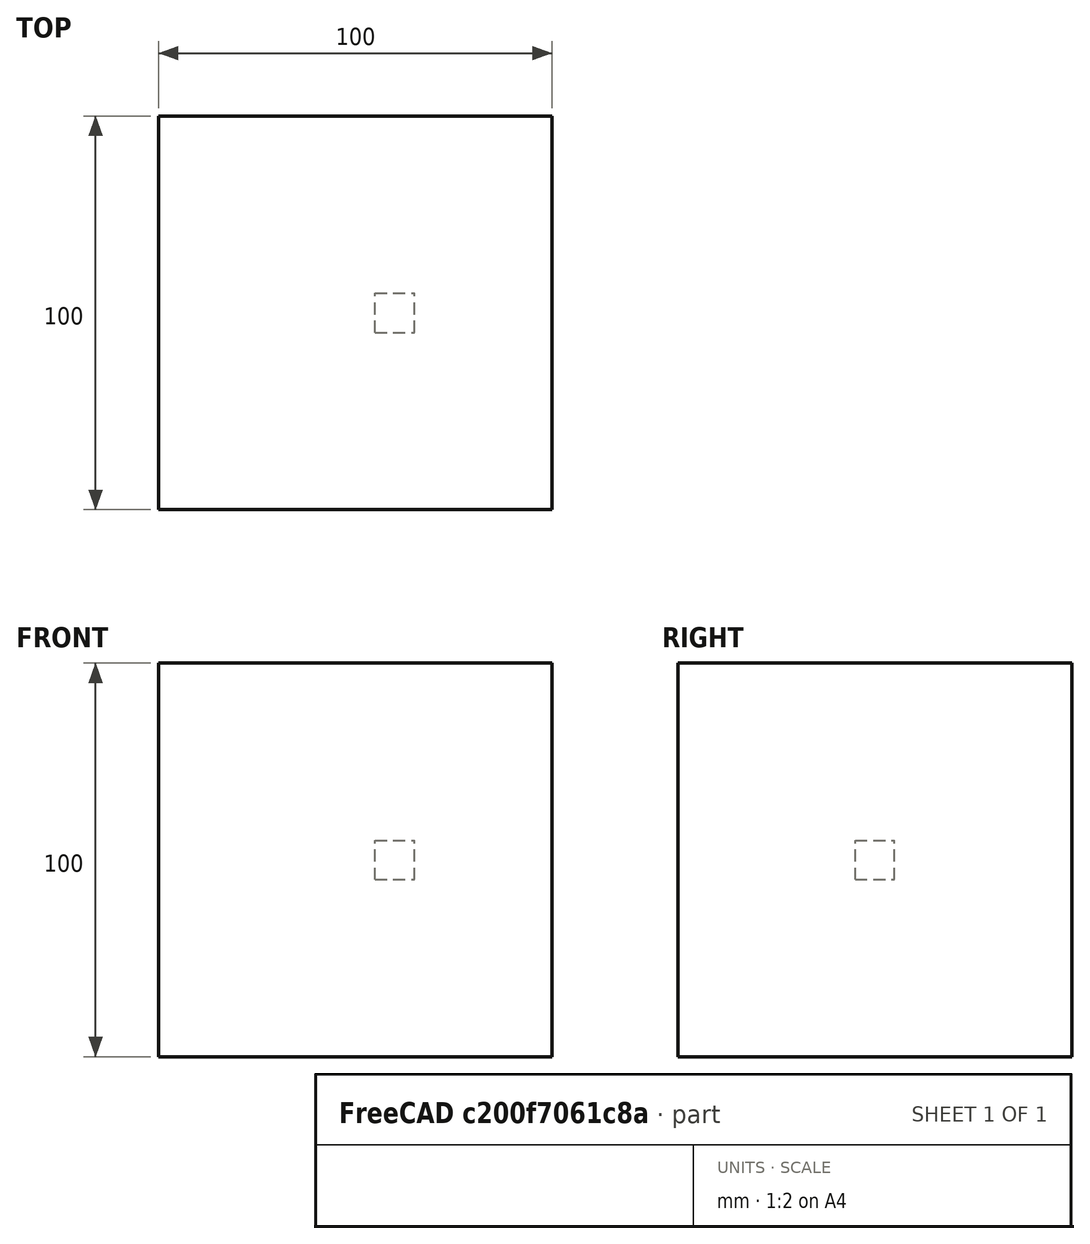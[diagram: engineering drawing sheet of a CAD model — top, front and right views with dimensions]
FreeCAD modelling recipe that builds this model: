
FCSTD DOCUMENT  (FreeCAD 0.20RUnknown)
Label: orthoArray-1
License: All rights reserved
objects: App::DocumentObjectGroupPython×1251, Part::FeaturePython×3, App::Part×3
note: 2 computed .brp shape members not serialized (recipe doc carries the construction recipe); baked Part::Feature solids carry a one-line shape summary decoded from their .brp

FEATURE [App::DocumentObjectGroupPython] HALFPI  # scripted group (container) (typed FeaturePython)
  name = HALFPI
  value = pi/2.
FEATURE [App::DocumentObjectGroupPython] PI  # scripted group (container) (typed FeaturePython)
  name = PI
  value = 1.*pi
FEATURE [App::DocumentObjectGroupPython] TWOPI  # scripted group (container) (typed FeaturePython)
  name = TWOPI
  value = 2.*pi
FEATURE [App::DocumentObjectGroupPython] Constants  # scripted group (container) (typed FeaturePython)
  Group = -> [HALFPI,PI,TWOPI]
FEATURE [App::DocumentObjectGroupPython] Variables  # scripted group (container) (typed FeaturePython)
FEATURE [App::DocumentObjectGroupPython] Quantities  # scripted group (container) (typed FeaturePython)
FEATURE [App::DocumentObjectGroupPython] Isotopes  # scripted group (container) (typed FeaturePython)
FEATURE [App::DocumentObjectGroupPython] Elements  # scripted group (container) (typed FeaturePython)
FEATURE [App::DocumentObjectGroupPython] Matrix  # scripted group (container) (typed FeaturePython)
FEATURE [App::DocumentObjectGroupPython] Surfaces  # scripted group (container) (typed FeaturePython)
FEATURE [App::DocumentObjectGroupPython] Opticals  # scripted group (container) (typed FeaturePython)
  Group = -> [Matrix,Surfaces]
FEATURE [App::DocumentObjectGroupPython] G4Isotopes  # scripted group (container) (typed FeaturePython)
FEATURE [App::DocumentObjectGroupPython] H_element  # scripted group (container) (typed FeaturePython)
  Z = 1
  atom_value = 1.008
  formula = H
  name = H_element
FEATURE [App::DocumentObjectGroupPython] He_element  # scripted group (container) (typed FeaturePython)
  Z = 2
  atom_value = 4.0026
  formula = He
  name = He_element
FEATURE [App::DocumentObjectGroupPython] Li_element  # scripted group (container) (typed FeaturePython)
  Z = 3
  atom_value = 6.94
  formula = Li
  name = Li_element
FEATURE [App::DocumentObjectGroupPython] Be_element  # scripted group (container) (typed FeaturePython)
  Z = 4
  atom_value = 9.01218
  formula = Be
  name = Be_element
FEATURE [App::DocumentObjectGroupPython] B_element  # scripted group (container) (typed FeaturePython)
  Z = 5
  atom_value = 10.81
  formula = B
  name = B_element
FEATURE [App::DocumentObjectGroupPython] C_element  # scripted group (container) (typed FeaturePython)
  Z = 6
  atom_value = 12.011
  formula = C
  name = C_element
FEATURE [App::DocumentObjectGroupPython] N_element  # scripted group (container) (typed FeaturePython)
  Z = 7
  atom_value = 14.007
  formula = N
  name = N_element
FEATURE [App::DocumentObjectGroupPython] O_element  # scripted group (container) (typed FeaturePython)
  Z = 8
  atom_value = 15.999
  formula = O
  name = O_element
FEATURE [App::DocumentObjectGroupPython] F_element  # scripted group (container) (typed FeaturePython)
  Z = 9
  atom_value = 18.9984
  formula = F
  name = F_element
FEATURE [App::DocumentObjectGroupPython] Ne_element  # scripted group (container) (typed FeaturePython)
  Z = 10
  atom_value = 20.1797
  formula = Ne
  name = Ne_element
FEATURE [App::DocumentObjectGroupPython] Na_element  # scripted group (container) (typed FeaturePython)
  Z = 11
  atom_value = 22.9898
  formula = Na
  name = Na_element
FEATURE [App::DocumentObjectGroupPython] Mg_element  # scripted group (container) (typed FeaturePython)
  Z = 12
  atom_value = 24.305
  formula = Mg
  name = Mg_element
FEATURE [App::DocumentObjectGroupPython] Al_element  # scripted group (container) (typed FeaturePython)
  Z = 13
  atom_value = 26.9815
  formula = Al
  name = Al_element
FEATURE [App::DocumentObjectGroupPython] Si_element  # scripted group (container) (typed FeaturePython)
  Z = 14
  atom_value = 28.085
  formula = Si
  name = Si_element
FEATURE [App::DocumentObjectGroupPython] P_element  # scripted group (container) (typed FeaturePython)
  Z = 15
  atom_value = 30.9738
  formula = P
  name = P_element
FEATURE [App::DocumentObjectGroupPython] S_element  # scripted group (container) (typed FeaturePython)
  Z = 16
  atom_value = 32.06
  formula = S
  name = S_element
FEATURE [App::DocumentObjectGroupPython] Cl_element  # scripted group (container) (typed FeaturePython)
  Z = 17
  atom_value = 35.45
  formula = Cl
  name = Cl_element
FEATURE [App::DocumentObjectGroupPython] Ar_element  # scripted group (container) (typed FeaturePython)
  Z = 18
  atom_value = 39.95
  formula = Ar
  name = Ar_element
FEATURE [App::DocumentObjectGroupPython] K_element  # scripted group (container) (typed FeaturePython)
  Z = 19
  atom_value = 39.0983
  formula = K
  name = K_element
FEATURE [App::DocumentObjectGroupPython] Ca_element  # scripted group (container) (typed FeaturePython)
  Z = 20
  atom_value = 40.078
  formula = Ca
  name = Ca_element
FEATURE [App::DocumentObjectGroupPython] Sc_element  # scripted group (container) (typed FeaturePython)
  Z = 21
  atom_value = 44.9559
  formula = Sc
  name = Sc_element
FEATURE [App::DocumentObjectGroupPython] Ti_element  # scripted group (container) (typed FeaturePython)
  Z = 22
  atom_value = 47.867
  formula = Ti
  name = Ti_element
FEATURE [App::DocumentObjectGroupPython] V_element  # scripted group (container) (typed FeaturePython)
  Z = 23
  atom_value = 50.9415
  formula = V
  name = V_element
FEATURE [App::DocumentObjectGroupPython] Cr_element  # scripted group (container) (typed FeaturePython)
  Z = 24
  atom_value = 51.9961
  formula = Cr
  name = Cr_element
FEATURE [App::DocumentObjectGroupPython] Mn_element  # scripted group (container) (typed FeaturePython)
  Z = 25
  atom_value = 54.938
  formula = Mn
  name = Mn_element
FEATURE [App::DocumentObjectGroupPython] Fe_element  # scripted group (container) (typed FeaturePython)
  Z = 26
  atom_value = 55.845
  formula = Fe
  name = Fe_element
FEATURE [App::DocumentObjectGroupPython] Co_element  # scripted group (container) (typed FeaturePython)
  Z = 27
  atom_value = 58.9332
  formula = Co
  name = Co_element
FEATURE [App::DocumentObjectGroupPython] Ni_element  # scripted group (container) (typed FeaturePython)
  Z = 28
  atom_value = 58.6934
  formula = Ni
  name = Ni_element
FEATURE [App::DocumentObjectGroupPython] Cu_element  # scripted group (container) (typed FeaturePython)
  Z = 29
  atom_value = 63.546
  formula = Cu
  name = Cu_element
FEATURE [App::DocumentObjectGroupPython] Zn_element  # scripted group (container) (typed FeaturePython)
  Z = 30
  atom_value = 65.38
  formula = Zn
  name = Zn_element
FEATURE [App::DocumentObjectGroupPython] Ga_element  # scripted group (container) (typed FeaturePython)
  Z = 31
  atom_value = 69.723
  formula = Ga
  name = Ga_element
FEATURE [App::DocumentObjectGroupPython] Ge_element  # scripted group (container) (typed FeaturePython)
  Z = 32
  atom_value = 72.63
  formula = Ge
  name = Ge_element
FEATURE [App::DocumentObjectGroupPython] As_element  # scripted group (container) (typed FeaturePython)
  Z = 33
  atom_value = 74.9216
  formula = As
  name = As_element
FEATURE [App::DocumentObjectGroupPython] Se_element  # scripted group (container) (typed FeaturePython)
  Z = 34
  atom_value = 78.971
  formula = Se
  name = Se_element
FEATURE [App::DocumentObjectGroupPython] Br_element  # scripted group (container) (typed FeaturePython)
  Z = 35
  atom_value = 79.904
  formula = Br
  name = Br_element
FEATURE [App::DocumentObjectGroupPython] Kr_element  # scripted group (container) (typed FeaturePython)
  Z = 36
  atom_value = 83.798
  formula = Kr
  name = Kr_element
FEATURE [App::DocumentObjectGroupPython] Rb_element  # scripted group (container) (typed FeaturePython)
  Z = 37
  atom_value = 85.4678
  formula = Rb
  name = Rb_element
FEATURE [App::DocumentObjectGroupPython] Sr_element  # scripted group (container) (typed FeaturePython)
  Z = 38
  atom_value = 87.62
  formula = Sr
  name = Sr_element
FEATURE [App::DocumentObjectGroupPython] Y_element  # scripted group (container) (typed FeaturePython)
  Z = 39
  atom_value = 88.9058
  formula = Y
  name = Y_element
FEATURE [App::DocumentObjectGroupPython] Zr_element  # scripted group (container) (typed FeaturePython)
  Z = 40
  atom_value = 91.224
  formula = Zr
  name = Zr_element
FEATURE [App::DocumentObjectGroupPython] Nb_element  # scripted group (container) (typed FeaturePython)
  Z = 41
  atom_value = 92.9064
  formula = Nb
  name = Nb_element
FEATURE [App::DocumentObjectGroupPython] Mo_element  # scripted group (container) (typed FeaturePython)
  Z = 42
  atom_value = 95.95
  formula = Mo
  name = Mo_element
FEATURE [App::DocumentObjectGroupPython] Tc_element  # scripted group (container) (typed FeaturePython)
  Z = 43
  atom_value = 97
  formula = Tc
  name = Tc_element
FEATURE [App::DocumentObjectGroupPython] Ru_element  # scripted group (container) (typed FeaturePython)
  Z = 44
  atom_value = 101.07
  formula = Ru
  name = Ru_element
FEATURE [App::DocumentObjectGroupPython] Rh_element  # scripted group (container) (typed FeaturePython)
  Z = 45
  atom_value = 102.905
  formula = Rh
  name = Rh_element
FEATURE [App::DocumentObjectGroupPython] Pd_element  # scripted group (container) (typed FeaturePython)
  Z = 46
  atom_value = 106.42
  formula = Pd
  name = Pd_element
FEATURE [App::DocumentObjectGroupPython] Ag_element  # scripted group (container) (typed FeaturePython)
  Z = 47
  atom_value = 107.868
  formula = Ag
  name = Ag_element
FEATURE [App::DocumentObjectGroupPython] Cd_element  # scripted group (container) (typed FeaturePython)
  Z = 48
  atom_value = 112.414
  formula = Cd
  name = Cd_element
FEATURE [App::DocumentObjectGroupPython] In_element  # scripted group (container) (typed FeaturePython)
  Z = 49
  atom_value = 114.818
  formula = In
  name = In_element
FEATURE [App::DocumentObjectGroupPython] Sn_element  # scripted group (container) (typed FeaturePython)
  Z = 50
  atom_value = 118.71
  formula = Sn
  name = Sn_element
FEATURE [App::DocumentObjectGroupPython] Sb_element  # scripted group (container) (typed FeaturePython)
  Z = 51
  atom_value = 121.76
  formula = Sb
  name = Sb_element
FEATURE [App::DocumentObjectGroupPython] Te_element  # scripted group (container) (typed FeaturePython)
  Z = 52
  atom_value = 127.6
  formula = Te
  name = Te_element
FEATURE [App::DocumentObjectGroupPython] I_element  # scripted group (container) (typed FeaturePython)
  Z = 53
  atom_value = 126.904
  formula = I
  name = I_element
FEATURE [App::DocumentObjectGroupPython] Xe_element  # scripted group (container) (typed FeaturePython)
  Z = 54
  atom_value = 131.293
  formula = Xe
  name = Xe_element
FEATURE [App::DocumentObjectGroupPython] Cs_element  # scripted group (container) (typed FeaturePython)
  Z = 55
  atom_value = 132.905
  formula = Cs
  name = Cs_element
FEATURE [App::DocumentObjectGroupPython] Ba_element  # scripted group (container) (typed FeaturePython)
  Z = 56
  atom_value = 137.327
  formula = Ba
  name = Ba_element
FEATURE [App::DocumentObjectGroupPython] La_element  # scripted group (container) (typed FeaturePython)
  Z = 57
  atom_value = 138.905
  formula = La
  name = La_element
FEATURE [App::DocumentObjectGroupPython] Ce_element  # scripted group (container) (typed FeaturePython)
  Z = 58
  atom_value = 140.116
  formula = Ce
  name = Ce_element
FEATURE [App::DocumentObjectGroupPython] Pr_element  # scripted group (container) (typed FeaturePython)
  Z = 59
  atom_value = 140.908
  formula = Pr
  name = Pr_element
FEATURE [App::DocumentObjectGroupPython] Nd_element  # scripted group (container) (typed FeaturePython)
  Z = 60
  atom_value = 144.242
  formula = Nd
  name = Nd_element
FEATURE [App::DocumentObjectGroupPython] Pm_element  # scripted group (container) (typed FeaturePython)
  Z = 61
  atom_value = 145
  formula = Pm
  name = Pm_element
FEATURE [App::DocumentObjectGroupPython] Sm_element  # scripted group (container) (typed FeaturePython)
  Z = 62
  atom_value = 150.36
  formula = Sm
  name = Sm_element
FEATURE [App::DocumentObjectGroupPython] Eu_element  # scripted group (container) (typed FeaturePython)
  Z = 63
  atom_value = 151.964
  formula = Eu
  name = Eu_element
FEATURE [App::DocumentObjectGroupPython] Gd_element  # scripted group (container) (typed FeaturePython)
  Z = 64
  atom_value = 157.25
  formula = Gd
  name = Gd_element
FEATURE [App::DocumentObjectGroupPython] Tb_element  # scripted group (container) (typed FeaturePython)
  Z = 65
  atom_value = 158.925
  formula = Tb
  name = Tb_element
FEATURE [App::DocumentObjectGroupPython] Dy_element  # scripted group (container) (typed FeaturePython)
  Z = 66
  atom_value = 162.5
  formula = Dy
  name = Dy_element
FEATURE [App::DocumentObjectGroupPython] Ho_element  # scripted group (container) (typed FeaturePython)
  Z = 67
  atom_value = 164.93
  formula = Ho
  name = Ho_element
FEATURE [App::DocumentObjectGroupPython] Er_element  # scripted group (container) (typed FeaturePython)
  Z = 68
  atom_value = 167.259
  formula = Er
  name = Er_element
FEATURE [App::DocumentObjectGroupPython] Tm_element  # scripted group (container) (typed FeaturePython)
  Z = 69
  atom_value = 168.934
  formula = Tm
  name = Tm_element
FEATURE [App::DocumentObjectGroupPython] Yb_element  # scripted group (container) (typed FeaturePython)
  Z = 70
  atom_value = 173.045
  formula = Yb
  name = Yb_element
FEATURE [App::DocumentObjectGroupPython] Lu_element  # scripted group (container) (typed FeaturePython)
  Z = 71
  atom_value = 174.967
  formula = Lu
  name = Lu_element
FEATURE [App::DocumentObjectGroupPython] Hf_element  # scripted group (container) (typed FeaturePython)
  Z = 72
  atom_value = 178.49
  formula = Hf
  name = Hf_element
FEATURE [App::DocumentObjectGroupPython] Ta_element  # scripted group (container) (typed FeaturePython)
  Z = 73
  atom_value = 180.948
  formula = Ta
  name = Ta_element
FEATURE [App::DocumentObjectGroupPython] W_element  # scripted group (container) (typed FeaturePython)
  Z = 74
  atom_value = 183.84
  formula = W
  name = W_element
FEATURE [App::DocumentObjectGroupPython] Re_element  # scripted group (container) (typed FeaturePython)
  Z = 75
  atom_value = 186.207
  formula = Re
  name = Re_element
FEATURE [App::DocumentObjectGroupPython] Os_element  # scripted group (container) (typed FeaturePython)
  Z = 76
  atom_value = 190.23
  formula = Os
  name = Os_element
FEATURE [App::DocumentObjectGroupPython] Ir_element  # scripted group (container) (typed FeaturePython)
  Z = 77
  atom_value = 192.217
  formula = Ir
  name = Ir_element
FEATURE [App::DocumentObjectGroupPython] Pt_element  # scripted group (container) (typed FeaturePython)
  Z = 78
  atom_value = 195.084
  formula = Pt
  name = Pt_element
FEATURE [App::DocumentObjectGroupPython] Au_element  # scripted group (container) (typed FeaturePython)
  Z = 79
  atom_value = 196.967
  formula = Au
  name = Au_element
FEATURE [App::DocumentObjectGroupPython] Hg_element  # scripted group (container) (typed FeaturePython)
  Z = 80
  atom_value = 200.592
  formula = Hg
  name = Hg_element
FEATURE [App::DocumentObjectGroupPython] Tl_element  # scripted group (container) (typed FeaturePython)
  Z = 81
  atom_value = 204.38
  formula = Tl
  name = Tl_element
FEATURE [App::DocumentObjectGroupPython] Pb_element  # scripted group (container) (typed FeaturePython)
  Z = 82
  atom_value = 207.2
  formula = Pb
  name = Pb_element
FEATURE [App::DocumentObjectGroupPython] Bi_element  # scripted group (container) (typed FeaturePython)
  Z = 83
  atom_value = 208.98
  formula = Bi
  name = Bi_element
FEATURE [App::DocumentObjectGroupPython] Po_element  # scripted group (container) (typed FeaturePython)
  Z = 84
  atom_value = 209
  formula = Po
  name = Po_element
FEATURE [App::DocumentObjectGroupPython] At_element  # scripted group (container) (typed FeaturePython)
  Z = 85
  atom_value = 210
  formula = At
  name = At_element
FEATURE [App::DocumentObjectGroupPython] Rn_element  # scripted group (container) (typed FeaturePython)
  Z = 86
  atom_value = 222
  formula = Rn
  name = Rn_element
FEATURE [App::DocumentObjectGroupPython] Fr_element  # scripted group (container) (typed FeaturePython)
  Z = 87
  atom_value = 223
  formula = Fr
  name = Fr_element
FEATURE [App::DocumentObjectGroupPython] Ra_element  # scripted group (container) (typed FeaturePython)
  Z = 88
  atom_value = 226
  formula = Ra
  name = Ra_element
FEATURE [App::DocumentObjectGroupPython] Ac_element  # scripted group (container) (typed FeaturePython)
  Z = 89
  atom_value = 227
  formula = Ac
  name = Ac_element
FEATURE [App::DocumentObjectGroupPython] Th_element  # scripted group (container) (typed FeaturePython)
  Z = 90
  atom_value = 232.038
  formula = Th
  name = Th_element
FEATURE [App::DocumentObjectGroupPython] Pa_element  # scripted group (container) (typed FeaturePython)
  Z = 91
  atom_value = 231.036
  formula = Pa
  name = Pa_element
FEATURE [App::DocumentObjectGroupPython] U_element  # scripted group (container) (typed FeaturePython)
  Z = 92
  atom_value = 238.029
  formula = U
  name = U_element
FEATURE [App::DocumentObjectGroupPython] Np_element  # scripted group (container) (typed FeaturePython)
  Z = 93
  atom_value = 237
  formula = Np
  name = Np_element
FEATURE [App::DocumentObjectGroupPython] Pu_element  # scripted group (container) (typed FeaturePython)
  Z = 94
  atom_value = 244
  formula = Pu
  name = Pu_element
FEATURE [App::DocumentObjectGroupPython] Am_element  # scripted group (container) (typed FeaturePython)
  Z = 95
  atom_value = 243
  formula = Am
  name = Am_element
FEATURE [App::DocumentObjectGroupPython] Cm_element  # scripted group (container) (typed FeaturePython)
  Z = 96
  atom_value = 247
  formula = Cm
  name = Cm_element
FEATURE [App::DocumentObjectGroupPython] Bk_element  # scripted group (container) (typed FeaturePython)
  Z = 97
  atom_value = 247
  formula = Bk
  name = Bk_element
FEATURE [App::DocumentObjectGroupPython] Cf_element  # scripted group (container) (typed FeaturePython)
  Z = 98
  atom_value = 251
  formula = Cf
  name = Cf_element
FEATURE [App::DocumentObjectGroupPython] G4Elements  # scripted group (container) (typed FeaturePython)
  Group = -> [H_element,He_element,Li_element,Be_element,B_element,C_element,N_element,O_element,F_element,Ne_element,Na_element,Mg_element,Al_element,Si_element,P_element,S_element,Cl_element,Ar_element,K_element,Ca_element,Sc_element,Ti_element,V_element,Cr_element,Mn_element,Fe_element,Co_element,Ni_element,Cu_element,Zn_element,Ga_element,Ge_element,As_element,Se_element,Br_element,Kr_element,Rb_element,+61 more]
FEATURE [App::DocumentObjectGroupPython] H_element001  label="H_element : 0.101"  # scripted group (container) (typed FeaturePython)
  n = 0.101327
FEATURE [App::DocumentObjectGroupPython] C_element001  label="C_element : 0.775"  # scripted group (container) (typed FeaturePython)
  n = 0.7755
FEATURE [App::DocumentObjectGroupPython] N_element001  label="N_element : 0.035"  # scripted group (container) (typed FeaturePython)
  n = 0.035057
FEATURE [App::DocumentObjectGroupPython] O_element001  label="O_element : 0.052"  # scripted group (container) (typed FeaturePython)
  n = 0.0523159
FEATURE [App::DocumentObjectGroupPython] F_element001  label="F_element : 0.017"  # scripted group (container) (typed FeaturePython)
  n = 0.017422
FEATURE [App::DocumentObjectGroupPython] Ca_element001  label="Ca_element : 0.018"  # scripted group (container) (typed FeaturePython)
  n = 0.018378
FEATURE [App::DocumentObjectGroupPython] G4_A_150_TISSUE  label="G4_A-150_TISSUE"  # scripted group (container) (typed FeaturePython)
  Dunit = g/cm3
  Dvalue = 1.127
  Group = -> [H_element001,C_element001,N_element001,O_element001,F_element001,Ca_element001]
  conduct = 2
  density = 1
  expand = 3
  formula = G4_A-150_TISSUE
  name = G4_A-150_TISSUE
  specific = 4
FEATURE [App::DocumentObjectGroupPython] C_element002  label="C_element : 3"  # scripted group (container) (typed FeaturePython)
  n = 3
  ref = C_element
FEATURE [App::DocumentObjectGroupPython] H_element002  label="H_element : 6"  # scripted group (container) (typed FeaturePython)
  n = 6
  ref = H_element
FEATURE [App::DocumentObjectGroupPython] O_element002  label="O_element : 1"  # scripted group (container) (typed FeaturePython)
  n = 1
  ref = O_element
FEATURE [App::DocumentObjectGroupPython] G4_ACETONE  # scripted group (container) (typed FeaturePython)
  Dunit = g/cm3
  Dvalue = 0.7899
  Group = -> [C_element002,H_element002,O_element002]
  conduct = 2
  density = 1
  expand = 3
  formula = G4_ACETONE
  name = G4_ACETONE
  specific = 4
FEATURE [App::DocumentObjectGroupPython] C_element003  label="C_element : 2"  # scripted group (container) (typed FeaturePython)
  n = 2
  ref = C_element
FEATURE [App::DocumentObjectGroupPython] H_element003  label="H_element : 2"  # scripted group (container) (typed FeaturePython)
  n = 2
  ref = H_element
FEATURE [App::DocumentObjectGroupPython] G4_ACETYLENE  # scripted group (container) (typed FeaturePython)
  Dunit = g/cm3
  Dvalue = 0.0010967
  Group = -> [C_element003,H_element003]
  conduct = 2
  density = 1
  expand = 3
  formula = G4_ACETYLENE
  name = G4_ACETYLENE
  specific = 4
FEATURE [App::DocumentObjectGroupPython] C_element004  label="C_element : 5"  # scripted group (container) (typed FeaturePython)
  n = 5
  ref = C_element
FEATURE [App::DocumentObjectGroupPython] H_element004  label="H_element : 5"  # scripted group (container) (typed FeaturePython)
  n = 5
  ref = H_element
FEATURE [App::DocumentObjectGroupPython] N_element002  label="N_element : 5"  # scripted group (container) (typed FeaturePython)
  n = 5
  ref = N_element
FEATURE [App::DocumentObjectGroupPython] G4_ADENINE  # scripted group (container) (typed FeaturePython)
  Dunit = g/cm3
  Dvalue = 1.6
  Group = -> [C_element004,H_element004,N_element002]
  conduct = 2
  density = 1
  expand = 3
  formula = G4_ADENINE
  name = G4_ADENINE
  specific = 4
FEATURE [App::DocumentObjectGroupPython] H_element005  label="H_element : 0.114"  # scripted group (container) (typed FeaturePython)
  n = 0.114
FEATURE [App::DocumentObjectGroupPython] C_element005  label="C_element : 0.598"  # scripted group (container) (typed FeaturePython)
  n = 0.598
FEATURE [App::DocumentObjectGroupPython] N_element003  label="N_element : 0.007"  # scripted group (container) (typed FeaturePython)
  n = 0.007
FEATURE [App::DocumentObjectGroupPython] O_element003  label="O_element : 0.278"  # scripted group (container) (typed FeaturePython)
  n = 0.278
FEATURE [App::DocumentObjectGroupPython] Na_element001  label="Na_element : 0.001"  # scripted group (container) (typed FeaturePython)
  n = 0.001
FEATURE [App::DocumentObjectGroupPython] S_element001  label="S_element : 0.001"  # scripted group (container) (typed FeaturePython)
  n = 0.001
FEATURE [App::DocumentObjectGroupPython] Cl_element001  label="Cl_element : 0.001"  # scripted group (container) (typed FeaturePython)
  n = 0.001
FEATURE [App::DocumentObjectGroupPython] G4_ADIPOSE_TISSUE_ICRP  # scripted group (container) (typed FeaturePython)
  Dunit = g/cm3
  Dvalue = 0.95
  Group = -> [H_element005,C_element005,N_element003,O_element003,Na_element001,S_element001,Cl_element001]
  conduct = 2
  density = 1
  expand = 3
  formula = G4_ADIPOSE_TISSUE_ICRP
  name = G4_ADIPOSE_TISSUE_ICRP
  specific = 4
FEATURE [App::DocumentObjectGroupPython] C_element006  label="C_element : 0.000"  # scripted group (container) (typed FeaturePython)
  n = 0.000124
FEATURE [App::DocumentObjectGroupPython] N_element004  label="N_element : 0.755"  # scripted group (container) (typed FeaturePython)
  n = 0.755268
FEATURE [App::DocumentObjectGroupPython] O_element004  label="O_element : 0.232"  # scripted group (container) (typed FeaturePython)
  n = 0.231781
FEATURE [App::DocumentObjectGroupPython] Ar_element001  label="Ar_element : 0.013"  # scripted group (container) (typed FeaturePython)
  n = 0.012827
FEATURE [App::DocumentObjectGroupPython] G4_AIR  # scripted group (container) (typed FeaturePython)
  Dunit = g/cm3
  Dvalue = 0.00120479
  Group = -> [C_element006,N_element004,O_element004,Ar_element001]
  conduct = 2
  density = 1
  expand = 3
  formula = G4_AIR
  name = G4_AIR
  specific = 4
FEATURE [App::DocumentObjectGroupPython] C_element007  label="C_element : 006"  # scripted group (container) (typed FeaturePython)
  n = 3
  ref = C_element
FEATURE [App::DocumentObjectGroupPython] H_element006  label="H_element : 7"  # scripted group (container) (typed FeaturePython)
  n = 7
  ref = H_element
FEATURE [App::DocumentObjectGroupPython] N_element005  label="N_element : 1"  # scripted group (container) (typed FeaturePython)
  n = 1
  ref = N_element
FEATURE [App::DocumentObjectGroupPython] O_element005  label="O_element : 2"  # scripted group (container) (typed FeaturePython)
  n = 2
  ref = O_element
FEATURE [App::DocumentObjectGroupPython] G4_ALANINE  # scripted group (container) (typed FeaturePython)
  Dunit = g/cm3
  Dvalue = 1.42
  Group = -> [C_element007,H_element006,N_element005,O_element005]
  conduct = 2
  density = 1
  expand = 3
  formula = G4_ALANINE
  name = G4_ALANINE
  specific = 4
FEATURE [App::DocumentObjectGroupPython] Al_element001  label="Al_element : 2"  # scripted group (container) (typed FeaturePython)
  n = 2
  ref = Al_element
FEATURE [App::DocumentObjectGroupPython] O_element006  label="O_element : 3"  # scripted group (container) (typed FeaturePython)
  n = 3
  ref = O_element
FEATURE [App::DocumentObjectGroupPython] G4_ALUMINUM_OXIDE  # scripted group (container) (typed FeaturePython)
  Dunit = g/cm3
  Dvalue = 3.97
  Group = -> [Al_element001,O_element006]
  conduct = 2
  density = 1
  expand = 3
  formula = G4_ALUMINUM_OXIDE
  name = G4_ALUMINUM_OXIDE
  specific = 4
FEATURE [App::DocumentObjectGroupPython] H_element007  label="H_element : 0.106"  # scripted group (container) (typed FeaturePython)
  n = 0.10593
FEATURE [App::DocumentObjectGroupPython] C_element008  label="C_element : 0.789"  # scripted group (container) (typed FeaturePython)
  n = 0.788974
FEATURE [App::DocumentObjectGroupPython] O_element007  label="O_element : 0.105"  # scripted group (container) (typed FeaturePython)
  n = 0.105096
FEATURE [App::DocumentObjectGroupPython] G4_AMBER  # scripted group (container) (typed FeaturePython)
  Dunit = g/cm3
  Dvalue = 1.1
  Group = -> [H_element007,C_element008,O_element007]
  conduct = 2
  density = 1
  expand = 3
  formula = G4_AMBER
  name = G4_AMBER
  specific = 4
FEATURE [App::DocumentObjectGroupPython] N_element006  label="N_element : 006"  # scripted group (container) (typed FeaturePython)
  n = 1
  ref = N_element
FEATURE [App::DocumentObjectGroupPython] H_element008  label="H_element : 3"  # scripted group (container) (typed FeaturePython)
  n = 3
  ref = H_element
FEATURE [App::DocumentObjectGroupPython] G4_AMMONIA  # scripted group (container) (typed FeaturePython)
  Dunit = g/cm3
  Dvalue = 0.000826019
  Group = -> [N_element006,H_element008]
  conduct = 2
  density = 1
  expand = 3
  formula = G4_AMMONIA
  name = G4_AMMONIA
  specific = 4
FEATURE [App::DocumentObjectGroupPython] C_element009  label="C_element : 6"  # scripted group (container) (typed FeaturePython)
  n = 6
  ref = C_element
FEATURE [App::DocumentObjectGroupPython] H_element009  label="H_element : 008"  # scripted group (container) (typed FeaturePython)
  n = 7
  ref = H_element
FEATURE [App::DocumentObjectGroupPython] N_element007  label="N_element : 007"  # scripted group (container) (typed FeaturePython)
  n = 1
  ref = N_element
FEATURE [App::DocumentObjectGroupPython] G4_ANILINE  # scripted group (container) (typed FeaturePython)
  Dunit = g/cm3
  Dvalue = 1.0235
  Group = -> [C_element009,H_element009,N_element007]
  conduct = 2
  density = 1
  expand = 3
  formula = G4_ANILINE
  name = G4_ANILINE
  specific = 4
FEATURE [App::DocumentObjectGroupPython] C_element010  label="C_element : 14"  # scripted group (container) (typed FeaturePython)
  n = 14
  ref = C_element
FEATURE [App::DocumentObjectGroupPython] H_element010  label="H_element : 10"  # scripted group (container) (typed FeaturePython)
  n = 10
  ref = H_element
FEATURE [App::DocumentObjectGroupPython] G4_ANTHRACENE  # scripted group (container) (typed FeaturePython)
  Dunit = g/cm3
  Dvalue = 1.283
  Group = -> [C_element010,H_element010]
  conduct = 2
  density = 1
  expand = 3
  formula = G4_ANTHRACENE
  name = G4_ANTHRACENE
  specific = 4
FEATURE [App::DocumentObjectGroupPython] H_element011  label="H_element : 0.065"  # scripted group (container) (typed FeaturePython)
  n = 0.0654709
FEATURE [App::DocumentObjectGroupPython] C_element011  label="C_element : 0.537"  # scripted group (container) (typed FeaturePython)
  n = 0.536944
FEATURE [App::DocumentObjectGroupPython] N_element008  label="N_element : 0.021"  # scripted group (container) (typed FeaturePython)
  n = 0.0215
FEATURE [App::DocumentObjectGroupPython] O_element008  label="O_element : 0.032"  # scripted group (container) (typed FeaturePython)
  n = 0.032085
FEATURE [App::DocumentObjectGroupPython] F_element002  label="F_element : 0.167"  # scripted group (container) (typed FeaturePython)
  n = 0.167411
FEATURE [App::DocumentObjectGroupPython] Ca_element002  label="Ca_element : 0.177"  # scripted group (container) (typed FeaturePython)
  n = 0.176589
FEATURE [App::DocumentObjectGroupPython] G4_B_100_BONE  label="G4_B-100_BONE"  # scripted group (container) (typed FeaturePython)
  Dunit = g/cm3
  Dvalue = 1.45
  Group = -> [H_element011,C_element011,N_element008,O_element008,F_element002,Ca_element002]
  conduct = 2
  density = 1
  expand = 3
  formula = G4_B-100_BONE
  name = G4_B-100_BONE
  specific = 4
FEATURE [App::DocumentObjectGroupPython] H_element012  label="H_element : 0.057"  # scripted group (container) (typed FeaturePython)
  n = 0.057441
FEATURE [App::DocumentObjectGroupPython] C_element012  label="C_element : 0.790"  # scripted group (container) (typed FeaturePython)
  n = 0.774591
FEATURE [App::DocumentObjectGroupPython] O_element009  label="O_element : 0.168"  # scripted group (container) (typed FeaturePython)
  n = 0.167968
FEATURE [App::DocumentObjectGroupPython] G4_BAKELITE  # scripted group (container) (typed FeaturePython)
  Dunit = g/cm3
  Dvalue = 1.25
  Group = -> [H_element012,C_element012,O_element009]
  conduct = 2
  density = 1
  expand = 3
  formula = G4_BAKELITE
  name = G4_BAKELITE
  specific = 4
FEATURE [App::DocumentObjectGroupPython] Ba_element001  label="Ba_element : 1"  # scripted group (container) (typed FeaturePython)
  n = 1
  ref = Ba_element
FEATURE [App::DocumentObjectGroupPython] F_element003  label="F_element : 2"  # scripted group (container) (typed FeaturePython)
  n = 2
  ref = F_element
FEATURE [App::DocumentObjectGroupPython] G4_BARIUM_FLUORIDE  # scripted group (container) (typed FeaturePython)
  Dunit = g/cm3
  Dvalue = 4.89
  Group = -> [Ba_element001,F_element003]
  conduct = 2
  density = 1
  expand = 3
  formula = G4_BARIUM_FLUORIDE
  name = G4_BARIUM_FLUORIDE
  specific = 4
FEATURE [App::DocumentObjectGroupPython] Ba_element002  label="Ba_element : 002"  # scripted group (container) (typed FeaturePython)
  n = 1
  ref = Ba_element
FEATURE [App::DocumentObjectGroupPython] S_element002  label="S_element : 1"  # scripted group (container) (typed FeaturePython)
  n = 1
  ref = S_element
FEATURE [App::DocumentObjectGroupPython] O_element010  label="O_element : 4"  # scripted group (container) (typed FeaturePython)
  n = 4
  ref = O_element
FEATURE [App::DocumentObjectGroupPython] G4_BARIUM_SULFATE  # scripted group (container) (typed FeaturePython)
  Dunit = g/cm3
  Dvalue = 4.5
  Group = -> [Ba_element002,S_element002,O_element010]
  conduct = 2
  density = 1
  expand = 3
  formula = G4_BARIUM_SULFATE
  name = G4_BARIUM_SULFATE
  specific = 4
FEATURE [App::DocumentObjectGroupPython] C_element013  label="C_element : 007"  # scripted group (container) (typed FeaturePython)
  n = 6
  ref = C_element
FEATURE [App::DocumentObjectGroupPython] H_element013  label="H_element : 009"  # scripted group (container) (typed FeaturePython)
  n = 6
  ref = H_element
FEATURE [App::DocumentObjectGroupPython] G4_BENZENE  # scripted group (container) (typed FeaturePython)
  Dunit = g/cm3
  Dvalue = 0.87865
  Group = -> [C_element013,H_element013]
  conduct = 2
  density = 1
  expand = 3
  formula = G4_BENZENE
  name = G4_BENZENE
  specific = 4
FEATURE [App::DocumentObjectGroupPython] Be_element001  label="Be_element : 1"  # scripted group (container) (typed FeaturePython)
  n = 1
  ref = Be_element
FEATURE [App::DocumentObjectGroupPython] O_element011  label="O_element : 005"  # scripted group (container) (typed FeaturePython)
  n = 1
  ref = O_element
FEATURE [App::DocumentObjectGroupPython] G4_BERYLLIUM_OXIDE  # scripted group (container) (typed FeaturePython)
  Dunit = g/cm3
  Dvalue = 3.01
  Group = -> [Be_element001,O_element011]
  conduct = 2
  density = 1
  expand = 3
  formula = G4_BERYLLIUM_OXIDE
  name = G4_BERYLLIUM_OXIDE
  specific = 4
FEATURE [App::DocumentObjectGroupPython] Bi_element001  label="Bi_element : 4"  # scripted group (container) (typed FeaturePython)
  n = 4
  ref = Bi_element
FEATURE [App::DocumentObjectGroupPython] Ge_element001  label="Ge_element : 3"  # scripted group (container) (typed FeaturePython)
  n = 3
  ref = Ge_element
FEATURE [App::DocumentObjectGroupPython] O_element012  label="O_element : 12"  # scripted group (container) (typed FeaturePython)
  n = 12
  ref = O_element
FEATURE [App::DocumentObjectGroupPython] G4_BGO  # scripted group (container) (typed FeaturePython)
  Dunit = g/cm3
  Dvalue = 7.13
  Group = -> [Bi_element001,Ge_element001,O_element012]
  conduct = 2
  density = 1
  expand = 3
  formula = G4_BGO
  name = G4_BGO
  specific = 4
FEATURE [App::DocumentObjectGroupPython] H_element014  label="H_element : 0.102"  # scripted group (container) (typed FeaturePython)
  n = 0.102
FEATURE [App::DocumentObjectGroupPython] C_element014  label="C_element : 0.110"  # scripted group (container) (typed FeaturePython)
  n = 0.11
FEATURE [App::DocumentObjectGroupPython] N_element009  label="N_element : 0.033"  # scripted group (container) (typed FeaturePython)
  n = 0.033
FEATURE [App::DocumentObjectGroupPython] O_element013  label="O_element : 0.745"  # scripted group (container) (typed FeaturePython)
  n = 0.745
FEATURE [App::DocumentObjectGroupPython] Na_element002  label="Na_element : 0.002"  # scripted group (container) (typed FeaturePython)
  n = 0.001
FEATURE [App::DocumentObjectGroupPython] P_element001  label="P_element : 0.001"  # scripted group (container) (typed FeaturePython)
  n = 0.001
FEATURE [App::DocumentObjectGroupPython] S_element003  label="S_element : 0.002"  # scripted group (container) (typed FeaturePython)
  n = 0.002
FEATURE [App::DocumentObjectGroupPython] Cl_element002  label="Cl_element : 0.003"  # scripted group (container) (typed FeaturePython)
  n = 0.003
FEATURE [App::DocumentObjectGroupPython] K_element001  label="K_element : 0.002"  # scripted group (container) (typed FeaturePython)
  n = 0.002
FEATURE [App::DocumentObjectGroupPython] Fe_element001  label="Fe_element : 0.001"  # scripted group (container) (typed FeaturePython)
  n = 0.001
FEATURE [App::DocumentObjectGroupPython] G4_BLOOD_ICRP  # scripted group (container) (typed FeaturePython)
  Dunit = g/cm3
  Dvalue = 1.06
  Group = -> [H_element014,C_element014,N_element009,O_element013,Na_element002,P_element001,S_element003,Cl_element002,K_element001,Fe_element001]
  conduct = 2
  density = 1
  expand = 3
  formula = G4_BLOOD_ICRP
  name = G4_BLOOD_ICRP
  specific = 4
FEATURE [App::DocumentObjectGroupPython] H_element015  label="H_element : 0.064"  # scripted group (container) (typed FeaturePython)
  n = 0.064
FEATURE [App::DocumentObjectGroupPython] C_element015  label="C_element : 0.278"  # scripted group (container) (typed FeaturePython)
  n = 0.278
FEATURE [App::DocumentObjectGroupPython] N_element010  label="N_element : 0.027"  # scripted group (container) (typed FeaturePython)
  n = 0.027
FEATURE [App::DocumentObjectGroupPython] O_element014  label="O_element : 0.410"  # scripted group (container) (typed FeaturePython)
  n = 0.41
FEATURE [App::DocumentObjectGroupPython] Mg_element001  label="Mg_element : 0.002"  # scripted group (container) (typed FeaturePython)
  n = 0.002
FEATURE [App::DocumentObjectGroupPython] P_element002  label="P_element : 0.070"  # scripted group (container) (typed FeaturePython)
  n = 0.07
FEATURE [App::DocumentObjectGroupPython] S_element004  label="S_element : 0.003"  # scripted group (container) (typed FeaturePython)
  n = 0.002
FEATURE [App::DocumentObjectGroupPython] Ca_element003  label="Ca_element : 0.147"  # scripted group (container) (typed FeaturePython)
  n = 0.147
FEATURE [App::DocumentObjectGroupPython] G4_BONE_COMPACT_ICRU  # scripted group (container) (typed FeaturePython)
  Dunit = g/cm3
  Dvalue = 1.85
  Group = -> [H_element015,C_element015,N_element010,O_element014,Mg_element001,P_element002,S_element004,Ca_element003]
  conduct = 2
  density = 1
  expand = 3
  formula = G4_BONE_COMPACT_ICRU
  name = G4_BONE_COMPACT_ICRU
  specific = 4
FEATURE [App::DocumentObjectGroupPython] H_element016  label="H_element : 0.034"  # scripted group (container) (typed FeaturePython)
  n = 0.034
FEATURE [App::DocumentObjectGroupPython] C_element016  label="C_element : 0.155"  # scripted group (container) (typed FeaturePython)
  n = 0.155
FEATURE [App::DocumentObjectGroupPython] N_element011  label="N_element : 0.042"  # scripted group (container) (typed FeaturePython)
  n = 0.042
FEATURE [App::DocumentObjectGroupPython] O_element015  label="O_element : 0.435"  # scripted group (container) (typed FeaturePython)
  n = 0.435
FEATURE [App::DocumentObjectGroupPython] Na_element003  label="Na_element : 0.003"  # scripted group (container) (typed FeaturePython)
  n = 0.001
FEATURE [App::DocumentObjectGroupPython] Mg_element002  label="Mg_element : 0.003"  # scripted group (container) (typed FeaturePython)
  n = 0.002
FEATURE [App::DocumentObjectGroupPython] P_element003  label="P_element : 0.103"  # scripted group (container) (typed FeaturePython)
  n = 0.103
FEATURE [App::DocumentObjectGroupPython] S_element005  label="S_element : 0.004"  # scripted group (container) (typed FeaturePython)
  n = 0.003
FEATURE [App::DocumentObjectGroupPython] Ca_element004  label="Ca_element : 0.225"  # scripted group (container) (typed FeaturePython)
  n = 0.225
FEATURE [App::DocumentObjectGroupPython] G4_BONE_CORTICAL_ICRP  # scripted group (container) (typed FeaturePython)
  Dunit = g/cm3
  Dvalue = 1.92
  Group = -> [H_element016,C_element016,N_element011,O_element015,Na_element003,Mg_element002,P_element003,S_element005,Ca_element004]
  conduct = 2
  density = 1
  expand = 3
  formula = G4_BONE_CORTICAL_ICRP
  name = G4_BONE_CORTICAL_ICRP
  specific = 4
FEATURE [App::DocumentObjectGroupPython] B_element001  label="B_element : 4"  # scripted group (container) (typed FeaturePython)
  n = 4
  ref = B_element
FEATURE [App::DocumentObjectGroupPython] C_element017  label="C_element : 1"  # scripted group (container) (typed FeaturePython)
  n = 1
  ref = C_element
FEATURE [App::DocumentObjectGroupPython] G4_BORON_CARBIDE  # scripted group (container) (typed FeaturePython)
  Dunit = g/cm3
  Dvalue = 2.52
  Group = -> [B_element001,C_element017]
  conduct = 2
  density = 1
  expand = 3
  formula = G4_BORON_CARBIDE
  name = G4_BORON_CARBIDE
  specific = 4
FEATURE [App::DocumentObjectGroupPython] B_element002  label="B_element : 2"  # scripted group (container) (typed FeaturePython)
  n = 2
  ref = B_element
FEATURE [App::DocumentObjectGroupPython] O_element016  label="O_element : 006"  # scripted group (container) (typed FeaturePython)
  n = 3
  ref = O_element
FEATURE [App::DocumentObjectGroupPython] G4_BORON_OXIDE  # scripted group (container) (typed FeaturePython)
  Dunit = g/cm3
  Dvalue = 1.812
  Group = -> [B_element002,O_element016]
  conduct = 2
  density = 1
  expand = 3
  formula = G4_BORON_OXIDE
  name = G4_BORON_OXIDE
  specific = 4
FEATURE [App::DocumentObjectGroupPython] H_element017  label="H_element : 0.107"  # scripted group (container) (typed FeaturePython)
  n = 0.107
FEATURE [App::DocumentObjectGroupPython] C_element018  label="C_element : 0.145"  # scripted group (container) (typed FeaturePython)
  n = 0.145
FEATURE [App::DocumentObjectGroupPython] N_element012  label="N_element : 0.022"  # scripted group (container) (typed FeaturePython)
  n = 0.022
FEATURE [App::DocumentObjectGroupPython] O_element017  label="O_element : 0.712"  # scripted group (container) (typed FeaturePython)
  n = 0.712
FEATURE [App::DocumentObjectGroupPython] Na_element004  label="Na_element : 0.004"  # scripted group (container) (typed FeaturePython)
  n = 0.002
FEATURE [App::DocumentObjectGroupPython] P_element004  label="P_element : 0.004"  # scripted group (container) (typed FeaturePython)
  n = 0.004
FEATURE [App::DocumentObjectGroupPython] S_element006  label="S_element : 0.005"  # scripted group (container) (typed FeaturePython)
  n = 0.002
FEATURE [App::DocumentObjectGroupPython] Cl_element003  label="Cl_element : 0.004"  # scripted group (container) (typed FeaturePython)
  n = 0.003
FEATURE [App::DocumentObjectGroupPython] K_element002  label="K_element : 0.003"  # scripted group (container) (typed FeaturePython)
  n = 0.003
FEATURE [App::DocumentObjectGroupPython] G4_BRAIN_ICRP  # scripted group (container) (typed FeaturePython)
  Dunit = g/cm3
  Dvalue = 1.04
  Group = -> [H_element017,C_element018,N_element012,O_element017,Na_element004,P_element004,S_element006,Cl_element003,K_element002]
  conduct = 2
  density = 1
  expand = 3
  formula = G4_BRAIN_ICRP
  name = G4_BRAIN_ICRP
  specific = 4
FEATURE [App::DocumentObjectGroupPython] C_element019  label="C_element : 4"  # scripted group (container) (typed FeaturePython)
  n = 4
  ref = C_element
FEATURE [App::DocumentObjectGroupPython] H_element018  label="H_element : 010"  # scripted group (container) (typed FeaturePython)
  n = 10
  ref = H_element
FEATURE [App::DocumentObjectGroupPython] G4_BUTANE  # scripted group (container) (typed FeaturePython)
  Dunit = g/cm3
  Dvalue = 0.00249343
  Group = -> [C_element019,H_element018]
  conduct = 2
  density = 1
  expand = 3
  formula = G4_BUTANE
  name = G4_BUTANE
  specific = 4
FEATURE [App::DocumentObjectGroupPython] C_element020  label="C_element : 008"  # scripted group (container) (typed FeaturePython)
  n = 4
  ref = C_element
FEATURE [App::DocumentObjectGroupPython] H_element019  label="H_element : 011"  # scripted group (container) (typed FeaturePython)
  n = 10
  ref = H_element
FEATURE [App::DocumentObjectGroupPython] O_element018  label="O_element : 007"  # scripted group (container) (typed FeaturePython)
  n = 1
  ref = O_element
FEATURE [App::DocumentObjectGroupPython] G4_N_BUTYL_ALCOHOL  label="G4_N-BUTYL_ALCOHOL"  # scripted group (container) (typed FeaturePython)
  Dunit = g/cm3
  Dvalue = 0.8098
  Group = -> [C_element020,H_element019,O_element018]
  conduct = 2
  density = 1
  expand = 3
  formula = G4_N-BUTYL_ALCOHOL
  name = G4_N-BUTYL_ALCOHOL
  specific = 4
FEATURE [App::DocumentObjectGroupPython] H_element020  label="H_element : 0.025"  # scripted group (container) (typed FeaturePython)
  n = 0.02468
FEATURE [App::DocumentObjectGroupPython] C_element021  label="C_element : 0.502"  # scripted group (container) (typed FeaturePython)
  n = 0.501611
FEATURE [App::DocumentObjectGroupPython] O_element019  label="O_element : 0.005"  # scripted group (container) (typed FeaturePython)
  n = 0.004527
FEATURE [App::DocumentObjectGroupPython] F_element004  label="F_element : 0.465"  # scripted group (container) (typed FeaturePython)
  n = 0.465209
FEATURE [App::DocumentObjectGroupPython] Si_element001  label="Si_element : 0.004"  # scripted group (container) (typed FeaturePython)
  n = 0.003973
FEATURE [App::DocumentObjectGroupPython] G4_C_552  label="G4_C-552"  # scripted group (container) (typed FeaturePython)
  Dunit = g/cm3
  Dvalue = 1.76
  Group = -> [H_element020,C_element021,O_element019,F_element004,Si_element001]
  conduct = 2
  density = 1
  expand = 3
  formula = G4_C-552
  name = G4_C-552
  specific = 4
FEATURE [App::DocumentObjectGroupPython] Cd_element001  label="Cd_element : 1"  # scripted group (container) (typed FeaturePython)
  n = 1
  ref = Cd_element
FEATURE [App::DocumentObjectGroupPython] Te_element001  label="Te_element : 1"  # scripted group (container) (typed FeaturePython)
  n = 1
  ref = Te_element
FEATURE [App::DocumentObjectGroupPython] G4_CADMIUM_TELLURIDE  # scripted group (container) (typed FeaturePython)
  Dunit = g/cm3
  Dvalue = 6.2
  Group = -> [Cd_element001,Te_element001]
  conduct = 2
  density = 1
  expand = 3
  formula = G4_CADMIUM_TELLURIDE
  name = G4_CADMIUM_TELLURIDE
  specific = 4
FEATURE [App::DocumentObjectGroupPython] Cd_element002  label="Cd_element : 002"  # scripted group (container) (typed FeaturePython)
  n = 1
  ref = Cd_element
FEATURE [App::DocumentObjectGroupPython] W_element001  label="W_element : 1"  # scripted group (container) (typed FeaturePython)
  n = 1
  ref = W_element
FEATURE [App::DocumentObjectGroupPython] O_element020  label="O_element : 008"  # scripted group (container) (typed FeaturePython)
  n = 4
  ref = O_element
FEATURE [App::DocumentObjectGroupPython] G4_CADMIUM_TUNGSTATE  # scripted group (container) (typed FeaturePython)
  Dunit = g/cm3
  Dvalue = 7.9
  Group = -> [Cd_element002,W_element001,O_element020]
  conduct = 2
  density = 1
  expand = 3
  formula = G4_CADMIUM_TUNGSTATE
  name = G4_CADMIUM_TUNGSTATE
  specific = 4
FEATURE [App::DocumentObjectGroupPython] Ca_element005  label="Ca_element : 1"  # scripted group (container) (typed FeaturePython)
  n = 1
  ref = Ca_element
FEATURE [App::DocumentObjectGroupPython] C_element022  label="C_element : 009"  # scripted group (container) (typed FeaturePython)
  n = 1
  ref = C_element
FEATURE [App::DocumentObjectGroupPython] O_element021  label="O_element : 009"  # scripted group (container) (typed FeaturePython)
  n = 3
  ref = O_element
FEATURE [App::DocumentObjectGroupPython] G4_CALCIUM_CARBONATE  # scripted group (container) (typed FeaturePython)
  Dunit = g/cm3
  Dvalue = 2.8
  Group = -> [Ca_element005,C_element022,O_element021]
  conduct = 2
  density = 1
  expand = 3
  formula = G4_CALCIUM_CARBONATE
  name = G4_CALCIUM_CARBONATE
  specific = 4
FEATURE [App::DocumentObjectGroupPython] Ca_element006  label="Ca_element : 002"  # scripted group (container) (typed FeaturePython)
  n = 1
  ref = Ca_element
FEATURE [App::DocumentObjectGroupPython] F_element005  label="F_element : 003"  # scripted group (container) (typed FeaturePython)
  n = 2
  ref = F_element
FEATURE [App::DocumentObjectGroupPython] G4_CALCIUM_FLUORIDE  # scripted group (container) (typed FeaturePython)
  Dunit = g/cm3
  Dvalue = 3.18
  Group = -> [Ca_element006,F_element005]
  conduct = 2
  density = 1
  expand = 3
  formula = G4_CALCIUM_FLUORIDE
  name = G4_CALCIUM_FLUORIDE
  specific = 4
FEATURE [App::DocumentObjectGroupPython] Ca_element007  label="Ca_element : 003"  # scripted group (container) (typed FeaturePython)
  n = 1
  ref = Ca_element
FEATURE [App::DocumentObjectGroupPython] O_element022  label="O_element : 010"  # scripted group (container) (typed FeaturePython)
  n = 1
  ref = O_element
FEATURE [App::DocumentObjectGroupPython] G4_CALCIUM_OXIDE  # scripted group (container) (typed FeaturePython)
  Dunit = g/cm3
  Dvalue = 3.3
  Group = -> [Ca_element007,O_element022]
  conduct = 2
  density = 1
  expand = 3
  formula = G4_CALCIUM_OXIDE
  name = G4_CALCIUM_OXIDE
  specific = 4
FEATURE [App::DocumentObjectGroupPython] Ca_element008  label="Ca_element : 004"  # scripted group (container) (typed FeaturePython)
  n = 1
  ref = Ca_element
FEATURE [App::DocumentObjectGroupPython] S_element007  label="S_element : 002"  # scripted group (container) (typed FeaturePython)
  n = 1
  ref = S_element
FEATURE [App::DocumentObjectGroupPython] O_element023  label="O_element : 011"  # scripted group (container) (typed FeaturePython)
  n = 4
  ref = O_element
FEATURE [App::DocumentObjectGroupPython] G4_CALCIUM_SULFATE  # scripted group (container) (typed FeaturePython)
  Dunit = g/cm3
  Dvalue = 2.96
  Group = -> [Ca_element008,S_element007,O_element023]
  conduct = 2
  density = 1
  expand = 3
  formula = G4_CALCIUM_SULFATE
  name = G4_CALCIUM_SULFATE
  specific = 4
FEATURE [App::DocumentObjectGroupPython] Ca_element009  label="Ca_element : 005"  # scripted group (container) (typed FeaturePython)
  n = 1
  ref = Ca_element
FEATURE [App::DocumentObjectGroupPython] W_element002  label="W_element : 002"  # scripted group (container) (typed FeaturePython)
  n = 1
  ref = W_element
FEATURE [App::DocumentObjectGroupPython] O_element024  label="O_element : 012"  # scripted group (container) (typed FeaturePython)
  n = 4
  ref = O_element
FEATURE [App::DocumentObjectGroupPython] G4_CALCIUM_TUNGSTATE  # scripted group (container) (typed FeaturePython)
  Dunit = g/cm3
  Dvalue = 6.062
  Group = -> [Ca_element009,W_element002,O_element024]
  conduct = 2
  density = 1
  expand = 3
  formula = G4_CALCIUM_TUNGSTATE
  name = G4_CALCIUM_TUNGSTATE
  specific = 4
FEATURE [App::DocumentObjectGroupPython] C_element023  label="C_element : 010"  # scripted group (container) (typed FeaturePython)
  n = 1
  ref = C_element
FEATURE [App::DocumentObjectGroupPython] O_element025  label="O_element : 013"  # scripted group (container) (typed FeaturePython)
  n = 2
  ref = O_element
FEATURE [App::DocumentObjectGroupPython] G4_CARBON_DIOXIDE  # scripted group (container) (typed FeaturePython)
  Dunit = g/cm3
  Dvalue = 0.00184212
  Group = -> [C_element023,O_element025]
  conduct = 2
  density = 1
  expand = 3
  formula = G4_CARBON_DIOXIDE
  name = G4_CARBON_DIOXIDE
  specific = 4
FEATURE [App::DocumentObjectGroupPython] C_element024  label="C_element : 011"  # scripted group (container) (typed FeaturePython)
  n = 1
  ref = C_element
FEATURE [App::DocumentObjectGroupPython] Cl_element004  label="Cl_element : 4"  # scripted group (container) (typed FeaturePython)
  n = 4
  ref = Cl_element
FEATURE [App::DocumentObjectGroupPython] G4_CARBON_TETRACHLORIDE  # scripted group (container) (typed FeaturePython)
  Dunit = g/cm3
  Dvalue = 1.594
  Group = -> [C_element024,Cl_element004]
  conduct = 2
  density = 1
  expand = 3
  formula = G4_CARBON_TETRACHLORIDE
  name = G4_CARBON_TETRACHLORIDE
  specific = 4
FEATURE [App::DocumentObjectGroupPython] C_element025  label="C_element : 012"  # scripted group (container) (typed FeaturePython)
  n = 6
  ref = C_element
FEATURE [App::DocumentObjectGroupPython] H_element021  label="H_element : 012"  # scripted group (container) (typed FeaturePython)
  n = 10
  ref = H_element
FEATURE [App::DocumentObjectGroupPython] O_element026  label="O_element : 5"  # scripted group (container) (typed FeaturePython)
  n = 5
  ref = O_element
FEATURE [App::DocumentObjectGroupPython] G4_CELLULOSE_CELLOPHANE  # scripted group (container) (typed FeaturePython)
  Dunit = g/cm3
  Dvalue = 1.42
  Group = -> [C_element025,H_element021,O_element026]
  conduct = 2
  density = 1
  expand = 3
  formula = G4_CELLULOSE_CELLOPHANE
  name = G4_CELLULOSE_CELLOPHANE
  specific = 4
FEATURE [App::DocumentObjectGroupPython] H_element022  label="H_element : 0.067"  # scripted group (container) (typed FeaturePython)
  n = 0.067125
FEATURE [App::DocumentObjectGroupPython] C_element026  label="C_element : 0.545"  # scripted group (container) (typed FeaturePython)
  n = 0.545403
FEATURE [App::DocumentObjectGroupPython] O_element027  label="O_element : 0.387"  # scripted group (container) (typed FeaturePython)
  n = 0.387472
FEATURE [App::DocumentObjectGroupPython] G4_CELLULOSE_BUTYRATE  # scripted group (container) (typed FeaturePython)
  Dunit = g/cm3
  Dvalue = 1.2
  Group = -> [H_element022,C_element026,O_element027]
  conduct = 2
  density = 1
  expand = 3
  formula = G4_CELLULOSE_BUTYRATE
  name = G4_CELLULOSE_BUTYRATE
  specific = 4
FEATURE [App::DocumentObjectGroupPython] H_element023  label="H_element : 0.029"  # scripted group (container) (typed FeaturePython)
  n = 0.029216
FEATURE [App::DocumentObjectGroupPython] C_element027  label="C_element : 0.271"  # scripted group (container) (typed FeaturePython)
  n = 0.271296
FEATURE [App::DocumentObjectGroupPython] N_element013  label="N_element : 0.121"  # scripted group (container) (typed FeaturePython)
  n = 0.121276
FEATURE [App::DocumentObjectGroupPython] O_element028  label="O_element : 0.578"  # scripted group (container) (typed FeaturePython)
  n = 0.578212
FEATURE [App::DocumentObjectGroupPython] G4_CELLULOSE_NITRATE  # scripted group (container) (typed FeaturePython)
  Dunit = g/cm3
  Dvalue = 1.49
  Group = -> [H_element023,C_element027,N_element013,O_element028]
  conduct = 2
  density = 1
  expand = 3
  formula = G4_CELLULOSE_NITRATE
  name = G4_CELLULOSE_NITRATE
  specific = 4
FEATURE [App::DocumentObjectGroupPython] H_element024  label="H_element : 0.108"  # scripted group (container) (typed FeaturePython)
  n = 0.107596
FEATURE [App::DocumentObjectGroupPython] N_element014  label="N_element : 0.001"  # scripted group (container) (typed FeaturePython)
  n = 0.0008
FEATURE [App::DocumentObjectGroupPython] O_element029  label="O_element : 0.875"  # scripted group (container) (typed FeaturePython)
  n = 0.874976
FEATURE [App::DocumentObjectGroupPython] S_element008  label="S_element : 0.015"  # scripted group (container) (typed FeaturePython)
  n = 0.014627
FEATURE [App::DocumentObjectGroupPython] Ce_element001  label="Ce_element : 0.002"  # scripted group (container) (typed FeaturePython)
  n = 0.002001
FEATURE [App::DocumentObjectGroupPython] G4_CERIC_SULFATE  # scripted group (container) (typed FeaturePython)
  Dunit = g/cm3
  Dvalue = 1.03
  Group = -> [H_element024,N_element014,O_element029,S_element008,Ce_element001]
  conduct = 2
  density = 1
  expand = 3
  formula = G4_CERIC_SULFATE
  name = G4_CERIC_SULFATE
  specific = 4
FEATURE [App::DocumentObjectGroupPython] Cs_element001  label="Cs_element : 1"  # scripted group (container) (typed FeaturePython)
  n = 1
  ref = Cs_element
FEATURE [App::DocumentObjectGroupPython] F_element006  label="F_element : 1"  # scripted group (container) (typed FeaturePython)
  n = 1
  ref = F_element
FEATURE [App::DocumentObjectGroupPython] G4_CESIUM_FLUORIDE  # scripted group (container) (typed FeaturePython)
  Dunit = g/cm3
  Dvalue = 4.115
  Group = -> [Cs_element001,F_element006]
  conduct = 2
  density = 1
  expand = 3
  formula = G4_CESIUM_FLUORIDE
  name = G4_CESIUM_FLUORIDE
  specific = 4
FEATURE [App::DocumentObjectGroupPython] Cs_element002  label="Cs_element : 002"  # scripted group (container) (typed FeaturePython)
  n = 1
  ref = Cs_element
FEATURE [App::DocumentObjectGroupPython] I_element001  label="I_element : 1"  # scripted group (container) (typed FeaturePython)
  n = 1
  ref = I_element
FEATURE [App::DocumentObjectGroupPython] G4_CESIUM_IODIDE  # scripted group (container) (typed FeaturePython)
  Dunit = g/cm3
  Dvalue = 4.51
  Group = -> [Cs_element002,I_element001]
  conduct = 2
  density = 1
  expand = 3
  formula = G4_CESIUM_IODIDE
  name = G4_CESIUM_IODIDE
  specific = 4
FEATURE [App::DocumentObjectGroupPython] C_element028  label="C_element : 013"  # scripted group (container) (typed FeaturePython)
  n = 6
  ref = C_element
FEATURE [App::DocumentObjectGroupPython] H_element025  label="H_element : 013"  # scripted group (container) (typed FeaturePython)
  n = 5
  ref = H_element
FEATURE [App::DocumentObjectGroupPython] Cl_element005  label="Cl_element : 1"  # scripted group (container) (typed FeaturePython)
  n = 1
  ref = Cl_element
FEATURE [App::DocumentObjectGroupPython] G4_CHLOROBENZENE  # scripted group (container) (typed FeaturePython)
  Dunit = g/cm3
  Dvalue = 1.1058
  Group = -> [C_element028,H_element025,Cl_element005]
  conduct = 2
  density = 1
  expand = 3
  formula = G4_CHLOROBENZENE
  name = G4_CHLOROBENZENE
  specific = 4
FEATURE [App::DocumentObjectGroupPython] C_element029  label="C_element : 014"  # scripted group (container) (typed FeaturePython)
  n = 1
  ref = C_element
FEATURE [App::DocumentObjectGroupPython] H_element026  label="H_element : 1"  # scripted group (container) (typed FeaturePython)
  n = 1
  ref = H_element
FEATURE [App::DocumentObjectGroupPython] Cl_element006  label="Cl_element : 3"  # scripted group (container) (typed FeaturePython)
  n = 3
  ref = Cl_element
FEATURE [App::DocumentObjectGroupPython] G4_CHLOROFORM  # scripted group (container) (typed FeaturePython)
  Dunit = g/cm3
  Dvalue = 1.4832
  Group = -> [C_element029,H_element026,Cl_element006]
  conduct = 2
  density = 1
  expand = 3
  formula = G4_CHLOROFORM
  name = G4_CHLOROFORM
  specific = 4
FEATURE [App::DocumentObjectGroupPython] H_element027  label="H_element : 0.010"  # scripted group (container) (typed FeaturePython)
  n = 0.01
FEATURE [App::DocumentObjectGroupPython] C_element030  label="C_element : 0.001"  # scripted group (container) (typed FeaturePython)
  n = 0.001
FEATURE [App::DocumentObjectGroupPython] O_element030  label="O_element : 0.529"  # scripted group (container) (typed FeaturePython)
  n = 0.529107
FEATURE [App::DocumentObjectGroupPython] Na_element005  label="Na_element : 0.016"  # scripted group (container) (typed FeaturePython)
  n = 0.016
FEATURE [App::DocumentObjectGroupPython] Mg_element003  label="Mg_element : 0.004"  # scripted group (container) (typed FeaturePython)
  n = 0.002
FEATURE [App::DocumentObjectGroupPython] Al_element002  label="Al_element : 0.034"  # scripted group (container) (typed FeaturePython)
  n = 0.033872
FEATURE [App::DocumentObjectGroupPython] Si_element002  label="Si_element : 0.337"  # scripted group (container) (typed FeaturePython)
  n = 0.337021
FEATURE [App::DocumentObjectGroupPython] K_element003  label="K_element : 0.013"  # scripted group (container) (typed FeaturePython)
  n = 0.013
FEATURE [App::DocumentObjectGroupPython] Ca_element010  label="Ca_element : 0.044"  # scripted group (container) (typed FeaturePython)
  n = 0.044
FEATURE [App::DocumentObjectGroupPython] Fe_element002  label="Fe_element : 0.014"  # scripted group (container) (typed FeaturePython)
  n = 0.014
FEATURE [App::DocumentObjectGroupPython] G4_CONCRETE  # scripted group (container) (typed FeaturePython)
  Dunit = g/cm3
  Dvalue = 2.3
  Group = -> [H_element027,C_element030,O_element030,Na_element005,Mg_element003,Al_element002,Si_element002,K_element003,Ca_element010,Fe_element002]
  conduct = 2
  density = 1
  expand = 3
  formula = G4_CONCRETE
  name = G4_CONCRETE
  specific = 4
FEATURE [App::DocumentObjectGroupPython] C_element031  label="C_element : 015"  # scripted group (container) (typed FeaturePython)
  n = 6
  ref = C_element
FEATURE [App::DocumentObjectGroupPython] H_element028  label="H_element : 12"  # scripted group (container) (typed FeaturePython)
  n = 12
  ref = H_element
FEATURE [App::DocumentObjectGroupPython] G4_CYCLOHEXANE  # scripted group (container) (typed FeaturePython)
  Dunit = g/cm3
  Dvalue = 0.779
  Group = -> [C_element031,H_element028]
  conduct = 2
  density = 1
  expand = 3
  formula = G4_CYCLOHEXANE
  name = G4_CYCLOHEXANE
  specific = 4
FEATURE [App::DocumentObjectGroupPython] C_element032  label="C_element : 016"  # scripted group (container) (typed FeaturePython)
  n = 6
  ref = C_element
FEATURE [App::DocumentObjectGroupPython] H_element029  label="H_element : 4"  # scripted group (container) (typed FeaturePython)
  n = 4
  ref = H_element
FEATURE [App::DocumentObjectGroupPython] Cl_element007  label="Cl_element : 2"  # scripted group (container) (typed FeaturePython)
  n = 2
  ref = Cl_element
FEATURE [App::DocumentObjectGroupPython] G4_1_2_DICHLOROBENZENE  label="G4_1.2-DICHLOROBENZENE"  # scripted group (container) (typed FeaturePython)
  Dunit = g/cm3
  Dvalue = 1.3048
  Group = -> [C_element032,H_element029,Cl_element007]
  conduct = 2
  density = 1
  expand = 3
  formula = G4_1.2-DICHLOROBENZENE
  name = G4_1.2-DICHLOROBENZENE
  specific = 4
FEATURE [App::DocumentObjectGroupPython] C_element033  label="C_element : 017"  # scripted group (container) (typed FeaturePython)
  n = 4
  ref = C_element
FEATURE [App::DocumentObjectGroupPython] H_element030  label="H_element : 8"  # scripted group (container) (typed FeaturePython)
  n = 8
  ref = H_element
FEATURE [App::DocumentObjectGroupPython] O_element031  label="O_element : 014"  # scripted group (container) (typed FeaturePython)
  n = 1
  ref = O_element
FEATURE [App::DocumentObjectGroupPython] Cl_element008  label="Cl_element : 005"  # scripted group (container) (typed FeaturePython)
  n = 2
  ref = Cl_element
FEATURE [App::DocumentObjectGroupPython] G4_DICHLORODIETHYL_ETHER  # scripted group (container) (typed FeaturePython)
  Dunit = g/cm3
  Dvalue = 1.2199
  Group = -> [C_element033,H_element030,O_element031,Cl_element008]
  conduct = 2
  density = 1
  expand = 3
  formula = G4_DICHLORODIETHYL_ETHER
  name = G4_DICHLORODIETHYL_ETHER
  specific = 4
FEATURE [App::DocumentObjectGroupPython] C_element034  label="C_element : 018"  # scripted group (container) (typed FeaturePython)
  n = 2
  ref = C_element
FEATURE [App::DocumentObjectGroupPython] H_element031  label="H_element : 014"  # scripted group (container) (typed FeaturePython)
  n = 4
  ref = H_element
FEATURE [App::DocumentObjectGroupPython] Cl_element009  label="Cl_element : 006"  # scripted group (container) (typed FeaturePython)
  n = 2
  ref = Cl_element
FEATURE [App::DocumentObjectGroupPython] G4_1_2_DICHLOROETHANE  label="G4_1.2-DICHLOROETHANE"  # scripted group (container) (typed FeaturePython)
  Dunit = g/cm3
  Dvalue = 1.2351
  Group = -> [C_element034,H_element031,Cl_element009]
  conduct = 2
  density = 1
  expand = 3
  formula = G4_1.2-DICHLOROETHANE
  name = G4_1.2-DICHLOROETHANE
  specific = 4
FEATURE [App::DocumentObjectGroupPython] C_element035  label="C_element : 019"  # scripted group (container) (typed FeaturePython)
  n = 4
  ref = C_element
FEATURE [App::DocumentObjectGroupPython] H_element032  label="H_element : 015"  # scripted group (container) (typed FeaturePython)
  n = 10
  ref = H_element
FEATURE [App::DocumentObjectGroupPython] O_element032  label="O_element : 015"  # scripted group (container) (typed FeaturePython)
  n = 1
  ref = O_element
FEATURE [App::DocumentObjectGroupPython] G4_DIETHYL_ETHER  # scripted group (container) (typed FeaturePython)
  Dunit = g/cm3
  Dvalue = 0.71378
  Group = -> [C_element035,H_element032,O_element032]
  conduct = 2
  density = 1
  expand = 3
  formula = G4_DIETHYL_ETHER
  name = G4_DIETHYL_ETHER
  specific = 4
FEATURE [App::DocumentObjectGroupPython] C_element036  label="C_element : 020"  # scripted group (container) (typed FeaturePython)
  n = 3
  ref = C_element
FEATURE [App::DocumentObjectGroupPython] H_element033  label="H_element : 016"  # scripted group (container) (typed FeaturePython)
  n = 7
  ref = H_element
FEATURE [App::DocumentObjectGroupPython] N_element015  label="N_element : 008"  # scripted group (container) (typed FeaturePython)
  n = 1
  ref = N_element
FEATURE [App::DocumentObjectGroupPython] O_element033  label="O_element : 016"  # scripted group (container) (typed FeaturePython)
  n = 1
  ref = O_element
FEATURE [App::DocumentObjectGroupPython] G4_N_N_DIMETHYL_FORMAMIDE  label="G4_N.N-DIMETHYL_FORMAMIDE"  # scripted group (container) (typed FeaturePython)
  Dunit = g/cm3
  Dvalue = 0.9487
  Group = -> [C_element036,H_element033,N_element015,O_element033]
  conduct = 2
  density = 1
  expand = 3
  formula = G4_N.N-DIMETHYL_FORMAMIDE
  name = G4_N.N-DIMETHYL_FORMAMIDE
  specific = 4
FEATURE [App::DocumentObjectGroupPython] C_element037  label="C_element : 021"  # scripted group (container) (typed FeaturePython)
  n = 2
  ref = C_element
FEATURE [App::DocumentObjectGroupPython] H_element034  label="H_element : 017"  # scripted group (container) (typed FeaturePython)
  n = 6
  ref = H_element
FEATURE [App::DocumentObjectGroupPython] O_element034  label="O_element : 017"  # scripted group (container) (typed FeaturePython)
  n = 1
  ref = O_element
FEATURE [App::DocumentObjectGroupPython] S_element009  label="S_element : 003"  # scripted group (container) (typed FeaturePython)
  n = 1
  ref = S_element
FEATURE [App::DocumentObjectGroupPython] G4_DIMETHYL_SULFOXIDE  # scripted group (container) (typed FeaturePython)
  Dunit = g/cm3
  Dvalue = 1.1014
  Group = -> [C_element037,H_element034,O_element034,S_element009]
  conduct = 2
  density = 1
  expand = 3
  formula = G4_DIMETHYL_SULFOXIDE
  name = G4_DIMETHYL_SULFOXIDE
  specific = 4
FEATURE [App::DocumentObjectGroupPython] C_element038  label="C_element : 022"  # scripted group (container) (typed FeaturePython)
  n = 2
  ref = C_element
FEATURE [App::DocumentObjectGroupPython] H_element035  label="H_element : 018"  # scripted group (container) (typed FeaturePython)
  n = 6
  ref = H_element
FEATURE [App::DocumentObjectGroupPython] G4_ETHANE  # scripted group (container) (typed FeaturePython)
  Dunit = g/cm3
  Dvalue = 0.00125324
  Group = -> [C_element038,H_element035]
  conduct = 2
  density = 1
  expand = 3
  formula = G4_ETHANE
  name = G4_ETHANE
  specific = 4
FEATURE [App::DocumentObjectGroupPython] C_element039  label="C_element : 023"  # scripted group (container) (typed FeaturePython)
  n = 2
  ref = C_element
FEATURE [App::DocumentObjectGroupPython] H_element036  label="H_element : 019"  # scripted group (container) (typed FeaturePython)
  n = 6
  ref = H_element
FEATURE [App::DocumentObjectGroupPython] O_element035  label="O_element : 018"  # scripted group (container) (typed FeaturePython)
  n = 1
  ref = O_element
FEATURE [App::DocumentObjectGroupPython] G4_ETHYL_ALCOHOL  # scripted group (container) (typed FeaturePython)
  Dunit = g/cm3
  Dvalue = 0.7893
  Group = -> [C_element039,H_element036,O_element035]
  conduct = 2
  density = 1
  expand = 3
  formula = G4_ETHYL_ALCOHOL
  name = G4_ETHYL_ALCOHOL
  specific = 4
FEATURE [App::DocumentObjectGroupPython] H_element037  label="H_element : 0.090"  # scripted group (container) (typed FeaturePython)
  n = 0.090027
FEATURE [App::DocumentObjectGroupPython] C_element040  label="C_element : 0.585"  # scripted group (container) (typed FeaturePython)
  n = 0.585182
FEATURE [App::DocumentObjectGroupPython] O_element036  label="O_element : 0.325"  # scripted group (container) (typed FeaturePython)
  n = 0.324791
FEATURE [App::DocumentObjectGroupPython] G4_ETHYL_CELLULOSE  # scripted group (container) (typed FeaturePython)
  Dunit = g/cm3
  Dvalue = 1.13
  Group = -> [H_element037,C_element040,O_element036]
  conduct = 2
  density = 1
  expand = 3
  formula = G4_ETHYL_CELLULOSE
  name = G4_ETHYL_CELLULOSE
  specific = 4
FEATURE [App::DocumentObjectGroupPython] C_element041  label="C_element : 024"  # scripted group (container) (typed FeaturePython)
  n = 2
  ref = C_element
FEATURE [App::DocumentObjectGroupPython] H_element038  label="H_element : 020"  # scripted group (container) (typed FeaturePython)
  n = 4
  ref = H_element
FEATURE [App::DocumentObjectGroupPython] G4_ETHYLENE  # scripted group (container) (typed FeaturePython)
  Dunit = g/cm3
  Dvalue = 0.00117497
  Group = -> [C_element041,H_element038]
  conduct = 2
  density = 1
  expand = 3
  formula = G4_ETHYLENE
  name = G4_ETHYLENE
  specific = 4
FEATURE [App::DocumentObjectGroupPython] H_element039  label="H_element : 0.096"  # scripted group (container) (typed FeaturePython)
  n = 0.096
FEATURE [App::DocumentObjectGroupPython] C_element042  label="C_element : 0.195"  # scripted group (container) (typed FeaturePython)
  n = 0.195
FEATURE [App::DocumentObjectGroupPython] N_element016  label="N_element : 0.057"  # scripted group (container) (typed FeaturePython)
  n = 0.057
FEATURE [App::DocumentObjectGroupPython] O_element037  label="O_element : 0.646"  # scripted group (container) (typed FeaturePython)
  n = 0.646
FEATURE [App::DocumentObjectGroupPython] Na_element006  label="Na_element : 0.017"  # scripted group (container) (typed FeaturePython)
  n = 0.001
FEATURE [App::DocumentObjectGroupPython] P_element005  label="P_element : 0.104"  # scripted group (container) (typed FeaturePython)
  n = 0.001
FEATURE [App::DocumentObjectGroupPython] S_element010  label="S_element : 0.016"  # scripted group (container) (typed FeaturePython)
  n = 0.003
FEATURE [App::DocumentObjectGroupPython] Cl_element010  label="Cl_element : 0.005"  # scripted group (container) (typed FeaturePython)
  n = 0.001
FEATURE [App::DocumentObjectGroupPython] G4_EYE_LENS_ICRP  # scripted group (container) (typed FeaturePython)
  Dunit = g/cm3
  Dvalue = 1.07
  Group = -> [H_element039,C_element042,N_element016,O_element037,Na_element006,P_element005,S_element010,Cl_element010]
  conduct = 2
  density = 1
  expand = 3
  formula = G4_EYE_LENS_ICRP
  name = G4_EYE_LENS_ICRP
  specific = 4
FEATURE [App::DocumentObjectGroupPython] Fe_element003  label="Fe_element : 2"  # scripted group (container) (typed FeaturePython)
  n = 2
  ref = Fe_element
FEATURE [App::DocumentObjectGroupPython] O_element038  label="O_element : 019"  # scripted group (container) (typed FeaturePython)
  n = 3
  ref = O_element
FEATURE [App::DocumentObjectGroupPython] G4_FERRIC_OXIDE  # scripted group (container) (typed FeaturePython)
  Dunit = g/cm3
  Dvalue = 5.2
  Group = -> [Fe_element003,O_element038]
  conduct = 2
  density = 1
  expand = 3
  formula = G4_FERRIC_OXIDE
  name = G4_FERRIC_OXIDE
  specific = 4
FEATURE [App::DocumentObjectGroupPython] Fe_element004  label="Fe_element : 1"  # scripted group (container) (typed FeaturePython)
  n = 1
  ref = Fe_element
FEATURE [App::DocumentObjectGroupPython] B_element003  label="B_element : 1"  # scripted group (container) (typed FeaturePython)
  n = 1
  ref = B_element
FEATURE [App::DocumentObjectGroupPython] G4_FERROBORIDE  # scripted group (container) (typed FeaturePython)
  Dunit = g/cm3
  Dvalue = 7.15
  Group = -> [Fe_element004,B_element003]
  conduct = 2
  density = 1
  expand = 3
  formula = G4_FERROBORIDE
  name = G4_FERROBORIDE
  specific = 4
FEATURE [App::DocumentObjectGroupPython] Fe_element005  label="Fe_element : 003"  # scripted group (container) (typed FeaturePython)
  n = 1
  ref = Fe_element
FEATURE [App::DocumentObjectGroupPython] O_element039  label="O_element : 020"  # scripted group (container) (typed FeaturePython)
  n = 1
  ref = O_element
FEATURE [App::DocumentObjectGroupPython] G4_FERROUS_OXIDE  # scripted group (container) (typed FeaturePython)
  Dunit = g/cm3
  Dvalue = 5.7
  Group = -> [Fe_element005,O_element039]
  conduct = 2
  density = 1
  expand = 3
  formula = G4_FERROUS_OXIDE
  name = G4_FERROUS_OXIDE
  specific = 4
FEATURE [App::DocumentObjectGroupPython] H_element040  label="H_element : 0.115"  # scripted group (container) (typed FeaturePython)
  n = 0.108259
FEATURE [App::DocumentObjectGroupPython] N_element017  label="N_element : 0.000"  # scripted group (container) (typed FeaturePython)
  n = 2.7e-05
FEATURE [App::DocumentObjectGroupPython] O_element040  label="O_element : 0.879"  # scripted group (container) (typed FeaturePython)
  n = 0.878636
FEATURE [App::DocumentObjectGroupPython] Na_element007  label="Na_element : 0.000"  # scripted group (container) (typed FeaturePython)
  n = 2.2e-05
FEATURE [App::DocumentObjectGroupPython] S_element011  label="S_element : 0.013"  # scripted group (container) (typed FeaturePython)
  n = 0.012968
FEATURE [App::DocumentObjectGroupPython] Cl_element011  label="Cl_element : 0.000"  # scripted group (container) (typed FeaturePython)
  n = 3.4e-05
FEATURE [App::DocumentObjectGroupPython] Fe_element006  label="Fe_element : 0.000"  # scripted group (container) (typed FeaturePython)
  n = 5.4e-05
FEATURE [App::DocumentObjectGroupPython] G4_FERROUS_SULFATE  # scripted group (container) (typed FeaturePython)
  Dunit = g/cm3
  Dvalue = 1.024
  Group = -> [H_element040,N_element017,O_element040,Na_element007,S_element011,Cl_element011,Fe_element006]
  conduct = 2
  density = 1
  expand = 3
  formula = G4_FERROUS_SULFATE
  name = G4_FERROUS_SULFATE
  specific = 4
FEATURE [App::DocumentObjectGroupPython] C_element043  label="C_element : 0.099"  # scripted group (container) (typed FeaturePython)
  n = 0.099335
FEATURE [App::DocumentObjectGroupPython] F_element007  label="F_element : 0.314"  # scripted group (container) (typed FeaturePython)
  n = 0.314247
FEATURE [App::DocumentObjectGroupPython] Cl_element012  label="Cl_element : 0.586"  # scripted group (container) (typed FeaturePython)
  n = 0.586418
FEATURE [App::DocumentObjectGroupPython] G4_FREON_12  label="G4_FREON-12"  # scripted group (container) (typed FeaturePython)
  Dunit = g/cm3
  Dvalue = 1.12
  Group = -> [C_element043,F_element007,Cl_element012]
  conduct = 2
  density = 1
  expand = 3
  formula = G4_FREON-12
  name = G4_FREON-12
  specific = 4
FEATURE [App::DocumentObjectGroupPython] C_element044  label="C_element : 0.057"  # scripted group (container) (typed FeaturePython)
  n = 0.057245
FEATURE [App::DocumentObjectGroupPython] F_element008  label="F_element : 0.181"  # scripted group (container) (typed FeaturePython)
  n = 0.181096
FEATURE [App::DocumentObjectGroupPython] Br_element001  label="Br_element : 0.762"  # scripted group (container) (typed FeaturePython)
  n = 0.761659
FEATURE [App::DocumentObjectGroupPython] G4_FREON_12B2  label="G4_FREON-12B2"  # scripted group (container) (typed FeaturePython)
  Dunit = g/cm3
  Dvalue = 1.8
  Group = -> [C_element044,F_element008,Br_element001]
  conduct = 2
  density = 1
  expand = 3
  formula = G4_FREON-12B2
  name = G4_FREON-12B2
  specific = 4
FEATURE [App::DocumentObjectGroupPython] C_element045  label="C_element : 0.115"  # scripted group (container) (typed FeaturePython)
  n = 0.114983
FEATURE [App::DocumentObjectGroupPython] F_element009  label="F_element : 0.546"  # scripted group (container) (typed FeaturePython)
  n = 0.545621
FEATURE [App::DocumentObjectGroupPython] Cl_element013  label="Cl_element : 0.339"  # scripted group (container) (typed FeaturePython)
  n = 0.339396
FEATURE [App::DocumentObjectGroupPython] G4_FREON_13  label="G4_FREON-13"  # scripted group (container) (typed FeaturePython)
  Dunit = g/cm3
  Dvalue = 0.95
  Group = -> [C_element045,F_element009,Cl_element013]
  conduct = 2
  density = 1
  expand = 3
  formula = G4_FREON-13
  name = G4_FREON-13
  specific = 4
FEATURE [App::DocumentObjectGroupPython] C_element046  label="C_element : 025"  # scripted group (container) (typed FeaturePython)
  n = 1
  ref = C_element
FEATURE [App::DocumentObjectGroupPython] F_element010  label="F_element : 3"  # scripted group (container) (typed FeaturePython)
  n = 3
  ref = F_element
FEATURE [App::DocumentObjectGroupPython] Br_element002  label="Br_element : 1"  # scripted group (container) (typed FeaturePython)
  n = 1
  ref = Br_element
FEATURE [App::DocumentObjectGroupPython] G4_FREON_13B1  label="G4_FREON-13B1"  # scripted group (container) (typed FeaturePython)
  Dunit = g/cm3
  Dvalue = 1.5
  Group = -> [C_element046,F_element010,Br_element002]
  conduct = 2
  density = 1
  expand = 3
  formula = G4_FREON-13B1
  name = G4_FREON-13B1
  specific = 4
FEATURE [App::DocumentObjectGroupPython] C_element047  label="C_element : 0.061"  # scripted group (container) (typed FeaturePython)
  n = 0.061309
FEATURE [App::DocumentObjectGroupPython] F_element011  label="F_element : 0.291"  # scripted group (container) (typed FeaturePython)
  n = 0.290924
FEATURE [App::DocumentObjectGroupPython] I_element002  label="I_element : 0.648"  # scripted group (container) (typed FeaturePython)
  n = 0.647767
FEATURE [App::DocumentObjectGroupPython] G4_FREON_13I1  label="G4_FREON-13I1"  # scripted group (container) (typed FeaturePython)
  Dunit = g/cm3
  Dvalue = 1.8
  Group = -> [C_element047,F_element011,I_element002]
  conduct = 2
  density = 1
  expand = 3
  formula = G4_FREON-13I1
  name = G4_FREON-13I1
  specific = 4
FEATURE [App::DocumentObjectGroupPython] Gd_element001  label="Gd_element : 2"  # scripted group (container) (typed FeaturePython)
  n = 2
  ref = Gd_element
FEATURE [App::DocumentObjectGroupPython] O_element041  label="O_element : 021"  # scripted group (container) (typed FeaturePython)
  n = 2
  ref = O_element
FEATURE [App::DocumentObjectGroupPython] S_element012  label="S_element : 004"  # scripted group (container) (typed FeaturePython)
  n = 1
  ref = S_element
FEATURE [App::DocumentObjectGroupPython] G4_GADOLINIUM_OXYSULFIDE  # scripted group (container) (typed FeaturePython)
  Dunit = g/cm3
  Dvalue = 7.44
  Group = -> [Gd_element001,O_element041,S_element012]
  conduct = 2
  density = 1
  expand = 3
  formula = G4_GADOLINIUM_OXYSULFIDE
  name = G4_GADOLINIUM_OXYSULFIDE
  specific = 4
FEATURE [App::DocumentObjectGroupPython] Ga_element001  label="Ga_element : 1"  # scripted group (container) (typed FeaturePython)
  n = 1
  ref = Ga_element
FEATURE [App::DocumentObjectGroupPython] As_element001  label="As_element : 1"  # scripted group (container) (typed FeaturePython)
  n = 1
  ref = As_element
FEATURE [App::DocumentObjectGroupPython] G4_GALLIUM_ARSENIDE  # scripted group (container) (typed FeaturePython)
  Dunit = g/cm3
  Dvalue = 5.31
  Group = -> [Ga_element001,As_element001]
  conduct = 2
  density = 1
  expand = 3
  formula = G4_GALLIUM_ARSENIDE
  name = G4_GALLIUM_ARSENIDE
  specific = 4
FEATURE [App::DocumentObjectGroupPython] H_element041  label="H_element : 0.081"  # scripted group (container) (typed FeaturePython)
  n = 0.08118
FEATURE [App::DocumentObjectGroupPython] C_element048  label="C_element : 0.416"  # scripted group (container) (typed FeaturePython)
  n = 0.41606
FEATURE [App::DocumentObjectGroupPython] N_element018  label="N_element : 0.111"  # scripted group (container) (typed FeaturePython)
  n = 0.11124
FEATURE [App::DocumentObjectGroupPython] O_element042  label="O_element : 0.381"  # scripted group (container) (typed FeaturePython)
  n = 0.38064
FEATURE [App::DocumentObjectGroupPython] S_element013  label="S_element : 0.011"  # scripted group (container) (typed FeaturePython)
  n = 0.01088
FEATURE [App::DocumentObjectGroupPython] G4_GEL_PHOTO_EMULSION  # scripted group (container) (typed FeaturePython)
  Dunit = g/cm3
  Dvalue = 1.2914
  Group = -> [H_element041,C_element048,N_element018,O_element042,S_element013]
  conduct = 2
  density = 1
  expand = 3
  formula = G4_GEL_PHOTO_EMULSION
  name = G4_GEL_PHOTO_EMULSION
  specific = 4
FEATURE [App::DocumentObjectGroupPython] B_element004  label="B_element : 0.040"  # scripted group (container) (typed FeaturePython)
  n = 0.0400639
FEATURE [App::DocumentObjectGroupPython] O_element043  label="O_element : 0.540"  # scripted group (container) (typed FeaturePython)
  n = 0.539561
FEATURE [App::DocumentObjectGroupPython] Na_element008  label="Na_element : 0.028"  # scripted group (container) (typed FeaturePython)
  n = 0.0281909
FEATURE [App::DocumentObjectGroupPython] Al_element003  label="Al_element : 0.012"  # scripted group (container) (typed FeaturePython)
  n = 0.011644
FEATURE [App::DocumentObjectGroupPython] Si_element003  label="Si_element : 0.377"  # scripted group (container) (typed FeaturePython)
  n = 0.377219
FEATURE [App::DocumentObjectGroupPython] K_element004  label="K_element : 0.014"  # scripted group (container) (typed FeaturePython)
  n = 0.00332099
FEATURE [App::DocumentObjectGroupPython] G4_Pyrex_Glass  # scripted group (container) (typed FeaturePython)
  Dunit = g/cm3
  Dvalue = 2.23
  Group = -> [B_element004,O_element043,Na_element008,Al_element003,Si_element003,K_element004]
  conduct = 2
  density = 1
  expand = 3
  formula = G4_Pyrex_Glass
  name = G4_Pyrex_Glass
  specific = 4
FEATURE [App::DocumentObjectGroupPython] O_element044  label="O_element : 0.156"  # scripted group (container) (typed FeaturePython)
  n = 0.156453
FEATURE [App::DocumentObjectGroupPython] Si_element004  label="Si_element : 0.081"  # scripted group (container) (typed FeaturePython)
  n = 0.080866
FEATURE [App::DocumentObjectGroupPython] Ti_element001  label="Ti_element : 0.008"  # scripted group (container) (typed FeaturePython)
  n = 0.008092
FEATURE [App::DocumentObjectGroupPython] As_element002  label="As_element : 0.003"  # scripted group (container) (typed FeaturePython)
  n = 0.002651
FEATURE [App::DocumentObjectGroupPython] Pb_element001  label="Pb_element : 0.752"  # scripted group (container) (typed FeaturePython)
  n = 0.751938
FEATURE [App::DocumentObjectGroupPython] G4_GLASS_LEAD  # scripted group (container) (typed FeaturePython)
  Dunit = g/cm3
  Dvalue = 6.22
  Group = -> [O_element044,Si_element004,Ti_element001,As_element002,Pb_element001]
  conduct = 2
  density = 1
  expand = 3
  formula = G4_GLASS_LEAD
  name = G4_GLASS_LEAD
  specific = 4
FEATURE [App::DocumentObjectGroupPython] O_element045  label="O_element : 0.460"  # scripted group (container) (typed FeaturePython)
  n = 0.4598
FEATURE [App::DocumentObjectGroupPython] Na_element009  label="Na_element : 0.096"  # scripted group (container) (typed FeaturePython)
  n = 0.0964411
FEATURE [App::DocumentObjectGroupPython] Si_element005  label="Si_element : 0.378"  # scripted group (container) (typed FeaturePython)
  n = 0.336553
FEATURE [App::DocumentObjectGroupPython] Ca_element011  label="Ca_element : 0.107"  # scripted group (container) (typed FeaturePython)
  n = 0.107205
FEATURE [App::DocumentObjectGroupPython] G4_GLASS_PLATE  # scripted group (container) (typed FeaturePython)
  Dunit = g/cm3
  Dvalue = 2.4
  Group = -> [O_element045,Na_element009,Si_element005,Ca_element011]
  conduct = 2
  density = 1
  expand = 3
  formula = G4_GLASS_PLATE
  name = G4_GLASS_PLATE
  specific = 4
FEATURE [App::DocumentObjectGroupPython] C_element049  label="C_element : 026"  # scripted group (container) (typed FeaturePython)
  n = 5
  ref = C_element
FEATURE [App::DocumentObjectGroupPython] H_element042  label="H_element : 021"  # scripted group (container) (typed FeaturePython)
  n = 10
  ref = H_element
FEATURE [App::DocumentObjectGroupPython] N_element019  label="N_element : 2"  # scripted group (container) (typed FeaturePython)
  n = 2
  ref = N_element
FEATURE [App::DocumentObjectGroupPython] O_element046  label="O_element : 022"  # scripted group (container) (typed FeaturePython)
  n = 3
  ref = O_element
FEATURE [App::DocumentObjectGroupPython] G4_GLUTAMINE  # scripted group (container) (typed FeaturePython)
  Dunit = g/cm3
  Dvalue = 1.46
  Group = -> [C_element049,H_element042,N_element019,O_element046]
  conduct = 2
  density = 1
  expand = 3
  formula = G4_GLUTAMINE
  name = G4_GLUTAMINE
  specific = 4
FEATURE [App::DocumentObjectGroupPython] C_element050  label="C_element : 027"  # scripted group (container) (typed FeaturePython)
  n = 3
  ref = C_element
FEATURE [App::DocumentObjectGroupPython] H_element043  label="H_element : 022"  # scripted group (container) (typed FeaturePython)
  n = 8
  ref = H_element
FEATURE [App::DocumentObjectGroupPython] O_element047  label="O_element : 023"  # scripted group (container) (typed FeaturePython)
  n = 3
  ref = O_element
FEATURE [App::DocumentObjectGroupPython] G4_GLYCEROL  # scripted group (container) (typed FeaturePython)
  Dunit = g/cm3
  Dvalue = 1.2613
  Group = -> [C_element050,H_element043,O_element047]
  conduct = 2
  density = 1
  expand = 3
  formula = G4_GLYCEROL
  name = G4_GLYCEROL
  specific = 4
FEATURE [App::DocumentObjectGroupPython] C_element051  label="C_element : 028"  # scripted group (container) (typed FeaturePython)
  n = 5
  ref = C_element
FEATURE [App::DocumentObjectGroupPython] H_element044  label="H_element : 023"  # scripted group (container) (typed FeaturePython)
  n = 5
  ref = H_element
FEATURE [App::DocumentObjectGroupPython] N_element020  label="N_element : 009"  # scripted group (container) (typed FeaturePython)
  n = 5
  ref = N_element
FEATURE [App::DocumentObjectGroupPython] O_element048  label="O_element : 024"  # scripted group (container) (typed FeaturePython)
  n = 1
  ref = O_element
FEATURE [App::DocumentObjectGroupPython] G4_GUANINE  # scripted group (container) (typed FeaturePython)
  Dunit = g/cm3
  Dvalue = 2.2
  Group = -> [C_element051,H_element044,N_element020,O_element048]
  conduct = 2
  density = 1
  expand = 3
  formula = G4_GUANINE
  name = G4_GUANINE
  specific = 4
FEATURE [App::DocumentObjectGroupPython] Ca_element012  label="Ca_element : 006"  # scripted group (container) (typed FeaturePython)
  n = 1
  ref = Ca_element
FEATURE [App::DocumentObjectGroupPython] S_element014  label="S_element : 005"  # scripted group (container) (typed FeaturePython)
  n = 1
  ref = S_element
FEATURE [App::DocumentObjectGroupPython] O_element049  label="O_element : 6"  # scripted group (container) (typed FeaturePython)
  n = 6
  ref = O_element
FEATURE [App::DocumentObjectGroupPython] H_element045  label="H_element : 024"  # scripted group (container) (typed FeaturePython)
  n = 4
  ref = H_element
FEATURE [App::DocumentObjectGroupPython] G4_GYPSUM  # scripted group (container) (typed FeaturePython)
  Dunit = g/cm3
  Dvalue = 2.32
  Group = -> [Ca_element012,S_element014,O_element049,H_element045]
  conduct = 2
  density = 1
  expand = 3
  formula = G4_GYPSUM
  name = G4_GYPSUM
  specific = 4
FEATURE [App::DocumentObjectGroupPython] C_element052  label="C_element : 7"  # scripted group (container) (typed FeaturePython)
  n = 7
  ref = C_element
FEATURE [App::DocumentObjectGroupPython] H_element046  label="H_element : 16"  # scripted group (container) (typed FeaturePython)
  n = 16
  ref = H_element
FEATURE [App::DocumentObjectGroupPython] G4_N_HEPTANE  label="G4_N-HEPTANE"  # scripted group (container) (typed FeaturePython)
  Dunit = g/cm3
  Dvalue = 0.68376
  Group = -> [C_element052,H_element046]
  conduct = 2
  density = 1
  expand = 3
  formula = G4_N-HEPTANE
  name = G4_N-HEPTANE
  specific = 4
FEATURE [App::DocumentObjectGroupPython] C_element053  label="C_element : 029"  # scripted group (container) (typed FeaturePython)
  n = 6
  ref = C_element
FEATURE [App::DocumentObjectGroupPython] H_element047  label="H_element : 14"  # scripted group (container) (typed FeaturePython)
  n = 14
  ref = H_element
FEATURE [App::DocumentObjectGroupPython] G4_N_HEXANE  label="G4_N-HEXANE"  # scripted group (container) (typed FeaturePython)
  Dunit = g/cm3
  Dvalue = 0.6603
  Group = -> [C_element053,H_element047]
  conduct = 2
  density = 1
  expand = 3
  formula = G4_N-HEXANE
  name = G4_N-HEXANE
  specific = 4
FEATURE [App::DocumentObjectGroupPython] C_element054  label="C_element : 22"  # scripted group (container) (typed FeaturePython)
  n = 22
  ref = C_element
FEATURE [App::DocumentObjectGroupPython] H_element048  label="H_element : 025"  # scripted group (container) (typed FeaturePython)
  n = 10
  ref = H_element
FEATURE [App::DocumentObjectGroupPython] N_element021  label="N_element : 010"  # scripted group (container) (typed FeaturePython)
  n = 2
  ref = N_element
FEATURE [App::DocumentObjectGroupPython] O_element050  label="O_element : 025"  # scripted group (container) (typed FeaturePython)
  n = 5
  ref = O_element
FEATURE [App::DocumentObjectGroupPython] G4_KAPTON  # scripted group (container) (typed FeaturePython)
  Dunit = g/cm3
  Dvalue = 1.42
  Group = -> [C_element054,H_element048,N_element021,O_element050]
  conduct = 2
  density = 1
  expand = 3
  formula = G4_KAPTON
  name = G4_KAPTON
  specific = 4
FEATURE [App::DocumentObjectGroupPython] La_element001  label="La_element : 1"  # scripted group (container) (typed FeaturePython)
  n = 1
  ref = La_element
FEATURE [App::DocumentObjectGroupPython] Br_element003  label="Br_element : 002"  # scripted group (container) (typed FeaturePython)
  n = 1
  ref = Br_element
FEATURE [App::DocumentObjectGroupPython] O_element051  label="O_element : 026"  # scripted group (container) (typed FeaturePython)
  n = 1
  ref = O_element
FEATURE [App::DocumentObjectGroupPython] G4_LANTHANUM_OXYBROMIDE  # scripted group (container) (typed FeaturePython)
  Dunit = g/cm3
  Dvalue = 6.28
  Group = -> [La_element001,Br_element003,O_element051]
  conduct = 2
  density = 1
  expand = 3
  formula = G4_LANTHANUM_OXYBROMIDE
  name = G4_LANTHANUM_OXYBROMIDE
  specific = 4
FEATURE [App::DocumentObjectGroupPython] La_element002  label="La_element : 2"  # scripted group (container) (typed FeaturePython)
  n = 2
  ref = La_element
FEATURE [App::DocumentObjectGroupPython] O_element052  label="O_element : 027"  # scripted group (container) (typed FeaturePython)
  n = 2
  ref = O_element
FEATURE [App::DocumentObjectGroupPython] S_element015  label="S_element : 006"  # scripted group (container) (typed FeaturePython)
  n = 1
  ref = S_element
FEATURE [App::DocumentObjectGroupPython] G4_LANTHANUM_OXYSULFIDE  # scripted group (container) (typed FeaturePython)
  Dunit = g/cm3
  Dvalue = 5.86
  Group = -> [La_element002,O_element052,S_element015]
  conduct = 2
  density = 1
  expand = 3
  formula = G4_LANTHANUM_OXYSULFIDE
  name = G4_LANTHANUM_OXYSULFIDE
  specific = 4
FEATURE [App::DocumentObjectGroupPython] O_element053  label="O_element : 0.072"  # scripted group (container) (typed FeaturePython)
  n = 0.071682
FEATURE [App::DocumentObjectGroupPython] Pb_element002  label="Pb_element : 0.928"  # scripted group (container) (typed FeaturePython)
  n = 0.928318
FEATURE [App::DocumentObjectGroupPython] G4_LEAD_OXIDE  # scripted group (container) (typed FeaturePython)
  Dunit = g/cm3
  Dvalue = 9.53
  Group = -> [O_element053,Pb_element002]
  conduct = 2
  density = 1
  expand = 3
  formula = G4_LEAD_OXIDE
  name = G4_LEAD_OXIDE
  specific = 4
FEATURE [App::DocumentObjectGroupPython] Li_element001  label="Li_element : 1"  # scripted group (container) (typed FeaturePython)
  n = 1
  ref = Li_element
FEATURE [App::DocumentObjectGroupPython] N_element022  label="N_element : 011"  # scripted group (container) (typed FeaturePython)
  n = 1
  ref = N_element
FEATURE [App::DocumentObjectGroupPython] H_element049  label="H_element : 026"  # scripted group (container) (typed FeaturePython)
  n = 2
  ref = H_element
FEATURE [App::DocumentObjectGroupPython] G4_LITHIUM_AMIDE  # scripted group (container) (typed FeaturePython)
  Dunit = g/cm3
  Dvalue = 1.178
  Group = -> [Li_element001,N_element022,H_element049]
  conduct = 2
  density = 1
  expand = 3
  formula = G4_LITHIUM_AMIDE
  name = G4_LITHIUM_AMIDE
  specific = 4
FEATURE [App::DocumentObjectGroupPython] Li_element002  label="Li_element : 2"  # scripted group (container) (typed FeaturePython)
  n = 2
  ref = Li_element
FEATURE [App::DocumentObjectGroupPython] C_element055  label="C_element : 030"  # scripted group (container) (typed FeaturePython)
  n = 1
  ref = C_element
FEATURE [App::DocumentObjectGroupPython] O_element054  label="O_element : 028"  # scripted group (container) (typed FeaturePython)
  n = 3
  ref = O_element
FEATURE [App::DocumentObjectGroupPython] G4_LITHIUM_CARBONATE  # scripted group (container) (typed FeaturePython)
  Dunit = g/cm3
  Dvalue = 2.11
  Group = -> [Li_element002,C_element055,O_element054]
  conduct = 2
  density = 1
  expand = 3
  formula = G4_LITHIUM_CARBONATE
  name = G4_LITHIUM_CARBONATE
  specific = 4
FEATURE [App::DocumentObjectGroupPython] Li_element003  label="Li_element : 003"  # scripted group (container) (typed FeaturePython)
  n = 1
  ref = Li_element
FEATURE [App::DocumentObjectGroupPython] F_element012  label="F_element : 004"  # scripted group (container) (typed FeaturePython)
  n = 1
  ref = F_element
FEATURE [App::DocumentObjectGroupPython] G4_LITHIUM_FLUORIDE  # scripted group (container) (typed FeaturePython)
  Dunit = g/cm3
  Dvalue = 2.635
  Group = -> [Li_element003,F_element012]
  conduct = 2
  density = 1
  expand = 3
  formula = G4_LITHIUM_FLUORIDE
  name = G4_LITHIUM_FLUORIDE
  specific = 4
FEATURE [App::DocumentObjectGroupPython] Li_element004  label="Li_element : 004"  # scripted group (container) (typed FeaturePython)
  n = 1
  ref = Li_element
FEATURE [App::DocumentObjectGroupPython] H_element050  label="H_element : 027"  # scripted group (container) (typed FeaturePython)
  n = 1
  ref = H_element
FEATURE [App::DocumentObjectGroupPython] G4_LITHIUM_HYDRIDE  # scripted group (container) (typed FeaturePython)
  Dunit = g/cm3
  Dvalue = 0.82
  Group = -> [Li_element004,H_element050]
  conduct = 2
  density = 1
  expand = 3
  formula = G4_LITHIUM_HYDRIDE
  name = G4_LITHIUM_HYDRIDE
  specific = 4
FEATURE [App::DocumentObjectGroupPython] Li_element005  label="Li_element : 005"  # scripted group (container) (typed FeaturePython)
  n = 1
  ref = Li_element
FEATURE [App::DocumentObjectGroupPython] I_element003  label="I_element : 002"  # scripted group (container) (typed FeaturePython)
  n = 1
  ref = I_element
FEATURE [App::DocumentObjectGroupPython] G4_LITHIUM_IODIDE  # scripted group (container) (typed FeaturePython)
  Dunit = g/cm3
  Dvalue = 3.494
  Group = -> [Li_element005,I_element003]
  conduct = 2
  density = 1
  expand = 3
  formula = G4_LITHIUM_IODIDE
  name = G4_LITHIUM_IODIDE
  specific = 4
FEATURE [App::DocumentObjectGroupPython] Li_element006  label="Li_element : 006"  # scripted group (container) (typed FeaturePython)
  n = 2
  ref = Li_element
FEATURE [App::DocumentObjectGroupPython] O_element055  label="O_element : 029"  # scripted group (container) (typed FeaturePython)
  n = 1
  ref = O_element
FEATURE [App::DocumentObjectGroupPython] G4_LITHIUM_OXIDE  # scripted group (container) (typed FeaturePython)
  Dunit = g/cm3
  Dvalue = 2.013
  Group = -> [Li_element006,O_element055]
  conduct = 2
  density = 1
  expand = 3
  formula = G4_LITHIUM_OXIDE
  name = G4_LITHIUM_OXIDE
  specific = 4
FEATURE [App::DocumentObjectGroupPython] Li_element007  label="Li_element : 007"  # scripted group (container) (typed FeaturePython)
  n = 2
  ref = Li_element
FEATURE [App::DocumentObjectGroupPython] B_element005  label="B_element : 005"  # scripted group (container) (typed FeaturePython)
  n = 4
  ref = B_element
FEATURE [App::DocumentObjectGroupPython] O_element056  label="O_element : 7"  # scripted group (container) (typed FeaturePython)
  n = 7
  ref = O_element
FEATURE [App::DocumentObjectGroupPython] G4_LITHIUM_TETRABORATE  # scripted group (container) (typed FeaturePython)
  Dunit = g/cm3
  Dvalue = 2.44
  Group = -> [Li_element007,B_element005,O_element056]
  conduct = 2
  density = 1
  expand = 3
  formula = G4_LITHIUM_TETRABORATE
  name = G4_LITHIUM_TETRABORATE
  specific = 4
FEATURE [App::DocumentObjectGroupPython] H_element051  label="H_element : 0.105"  # scripted group (container) (typed FeaturePython)
  n = 0.105
FEATURE [App::DocumentObjectGroupPython] C_element056  label="C_element : 0.083"  # scripted group (container) (typed FeaturePython)
  n = 0.083
FEATURE [App::DocumentObjectGroupPython] N_element023  label="N_element : 0.023"  # scripted group (container) (typed FeaturePython)
  n = 0.023
FEATURE [App::DocumentObjectGroupPython] O_element057  label="O_element : 0.779"  # scripted group (container) (typed FeaturePython)
  n = 0.779
FEATURE [App::DocumentObjectGroupPython] Na_element010  label="Na_element : 0.097"  # scripted group (container) (typed FeaturePython)
  n = 0.002
FEATURE [App::DocumentObjectGroupPython] P_element006  label="P_element : 0.105"  # scripted group (container) (typed FeaturePython)
  n = 0.001
FEATURE [App::DocumentObjectGroupPython] S_element016  label="S_element : 0.017"  # scripted group (container) (typed FeaturePython)
  n = 0.002
FEATURE [App::DocumentObjectGroupPython] Cl_element014  label="Cl_element : 0.587"  # scripted group (container) (typed FeaturePython)
  n = 0.003
FEATURE [App::DocumentObjectGroupPython] K_element005  label="K_element : 0.015"  # scripted group (container) (typed FeaturePython)
  n = 0.002
FEATURE [App::DocumentObjectGroupPython] G4_LUNG_ICRP  # scripted group (container) (typed FeaturePython)
  Dunit = g/cm3
  Dvalue = 1.04
  Group = -> [H_element051,C_element056,N_element023,O_element057,Na_element010,P_element006,S_element016,Cl_element014,K_element005]
  conduct = 2
  density = 1
  expand = 3
  formula = G4_LUNG_ICRP
  name = G4_LUNG_ICRP
  specific = 4
FEATURE [App::DocumentObjectGroupPython] H_element052  label="H_element : 0.116"  # scripted group (container) (typed FeaturePython)
  n = 0.114318
FEATURE [App::DocumentObjectGroupPython] C_element057  label="C_element : 0.656"  # scripted group (container) (typed FeaturePython)
  n = 0.655824
FEATURE [App::DocumentObjectGroupPython] O_element058  label="O_element : 0.092"  # scripted group (container) (typed FeaturePython)
  n = 0.0921831
FEATURE [App::DocumentObjectGroupPython] Mg_element004  label="Mg_element : 0.135"  # scripted group (container) (typed FeaturePython)
  n = 0.134792
FEATURE [App::DocumentObjectGroupPython] Ca_element013  label="Ca_element : 0.003"  # scripted group (container) (typed FeaturePython)
  n = 0.002883
FEATURE [App::DocumentObjectGroupPython] G4_M3_WAX  # scripted group (container) (typed FeaturePython)
  Dunit = g/cm3
  Dvalue = 1.05
  Group = -> [H_element052,C_element057,O_element058,Mg_element004,Ca_element013]
  conduct = 2
  density = 1
  expand = 3
  formula = G4_M3_WAX
  name = G4_M3_WAX
  specific = 4
FEATURE [App::DocumentObjectGroupPython] Mg_element005  label="Mg_element : 1"  # scripted group (container) (typed FeaturePython)
  n = 1
  ref = Mg_element
FEATURE [App::DocumentObjectGroupPython] C_element058  label="C_element : 031"  # scripted group (container) (typed FeaturePython)
  n = 1
  ref = C_element
FEATURE [App::DocumentObjectGroupPython] O_element059  label="O_element : 030"  # scripted group (container) (typed FeaturePython)
  n = 3
  ref = O_element
FEATURE [App::DocumentObjectGroupPython] G4_MAGNESIUM_CARBONATE  # scripted group (container) (typed FeaturePython)
  Dunit = g/cm3
  Dvalue = 2.958
  Group = -> [Mg_element005,C_element058,O_element059]
  conduct = 2
  density = 1
  expand = 3
  formula = G4_MAGNESIUM_CARBONATE
  name = G4_MAGNESIUM_CARBONATE
  specific = 4
FEATURE [App::DocumentObjectGroupPython] Mg_element006  label="Mg_element : 002"  # scripted group (container) (typed FeaturePython)
  n = 1
  ref = Mg_element
FEATURE [App::DocumentObjectGroupPython] F_element013  label="F_element : 005"  # scripted group (container) (typed FeaturePython)
  n = 2
  ref = F_element
FEATURE [App::DocumentObjectGroupPython] G4_MAGNESIUM_FLUORIDE  # scripted group (container) (typed FeaturePython)
  Dunit = g/cm3
  Dvalue = 3
  Group = -> [Mg_element006,F_element013]
  conduct = 2
  density = 1
  expand = 3
  formula = G4_MAGNESIUM_FLUORIDE
  name = G4_MAGNESIUM_FLUORIDE
  specific = 4
FEATURE [App::DocumentObjectGroupPython] Mg_element007  label="Mg_element : 003"  # scripted group (container) (typed FeaturePython)
  n = 1
  ref = Mg_element
FEATURE [App::DocumentObjectGroupPython] O_element060  label="O_element : 031"  # scripted group (container) (typed FeaturePython)
  n = 1
  ref = O_element
FEATURE [App::DocumentObjectGroupPython] G4_MAGNESIUM_OXIDE  # scripted group (container) (typed FeaturePython)
  Dunit = g/cm3
  Dvalue = 3.58
  Group = -> [Mg_element007,O_element060]
  conduct = 2
  density = 1
  expand = 3
  formula = G4_MAGNESIUM_OXIDE
  name = G4_MAGNESIUM_OXIDE
  specific = 4
FEATURE [App::DocumentObjectGroupPython] Mg_element008  label="Mg_element : 004"  # scripted group (container) (typed FeaturePython)
  n = 1
  ref = Mg_element
FEATURE [App::DocumentObjectGroupPython] B_element006  label="B_element : 006"  # scripted group (container) (typed FeaturePython)
  n = 4
  ref = B_element
FEATURE [App::DocumentObjectGroupPython] O_element061  label="O_element : 032"  # scripted group (container) (typed FeaturePython)
  n = 7
  ref = O_element
FEATURE [App::DocumentObjectGroupPython] G4_MAGNESIUM_TETRABORATE  # scripted group (container) (typed FeaturePython)
  Dunit = g/cm3
  Dvalue = 2.53
  Group = -> [Mg_element008,B_element006,O_element061]
  conduct = 2
  density = 1
  expand = 3
  formula = G4_MAGNESIUM_TETRABORATE
  name = G4_MAGNESIUM_TETRABORATE
  specific = 4
FEATURE [App::DocumentObjectGroupPython] Hg_element001  label="Hg_element : 1"  # scripted group (container) (typed FeaturePython)
  n = 1
  ref = Hg_element
FEATURE [App::DocumentObjectGroupPython] I_element004  label="I_element : 2"  # scripted group (container) (typed FeaturePython)
  n = 2
  ref = I_element
FEATURE [App::DocumentObjectGroupPython] G4_MERCURIC_IODIDE  # scripted group (container) (typed FeaturePython)
  Dunit = g/cm3
  Dvalue = 6.36
  Group = -> [Hg_element001,I_element004]
  conduct = 2
  density = 1
  expand = 3
  formula = G4_MERCURIC_IODIDE
  name = G4_MERCURIC_IODIDE
  specific = 4
FEATURE [App::DocumentObjectGroupPython] C_element059  label="C_element : 032"  # scripted group (container) (typed FeaturePython)
  n = 1
  ref = C_element
FEATURE [App::DocumentObjectGroupPython] H_element053  label="H_element : 028"  # scripted group (container) (typed FeaturePython)
  n = 4
  ref = H_element
FEATURE [App::DocumentObjectGroupPython] G4_METHANE  # scripted group (container) (typed FeaturePython)
  Dunit = g/cm3
  Dvalue = 0.000667151
  Group = -> [C_element059,H_element053]
  conduct = 2
  density = 1
  expand = 3
  formula = G4_METHANE
  name = G4_METHANE
  specific = 4
FEATURE [App::DocumentObjectGroupPython] C_element060  label="C_element : 033"  # scripted group (container) (typed FeaturePython)
  n = 1
  ref = C_element
FEATURE [App::DocumentObjectGroupPython] H_element054  label="H_element : 029"  # scripted group (container) (typed FeaturePython)
  n = 4
  ref = H_element
FEATURE [App::DocumentObjectGroupPython] O_element062  label="O_element : 033"  # scripted group (container) (typed FeaturePython)
  n = 1
  ref = O_element
FEATURE [App::DocumentObjectGroupPython] G4_METHANOL  # scripted group (container) (typed FeaturePython)
  Dunit = g/cm3
  Dvalue = 0.7914
  Group = -> [C_element060,H_element054,O_element062]
  conduct = 2
  density = 1
  expand = 3
  formula = G4_METHANOL
  name = G4_METHANOL
  specific = 4
FEATURE [App::DocumentObjectGroupPython] H_element055  label="H_element : 0.134"  # scripted group (container) (typed FeaturePython)
  n = 0.13404
FEATURE [App::DocumentObjectGroupPython] C_element061  label="C_element : 0.778"  # scripted group (container) (typed FeaturePython)
  n = 0.77796
FEATURE [App::DocumentObjectGroupPython] O_element063  label="O_element : 0.035"  # scripted group (container) (typed FeaturePython)
  n = 0.03502
FEATURE [App::DocumentObjectGroupPython] Mg_element009  label="Mg_element : 0.039"  # scripted group (container) (typed FeaturePython)
  n = 0.038594
FEATURE [App::DocumentObjectGroupPython] Ti_element002  label="Ti_element : 0.014"  # scripted group (container) (typed FeaturePython)
  n = 0.014386
FEATURE [App::DocumentObjectGroupPython] G4_MIX_D_WAX  # scripted group (container) (typed FeaturePython)
  Dunit = g/cm3
  Dvalue = 0.99
  Group = -> [H_element055,C_element061,O_element063,Mg_element009,Ti_element002]
  conduct = 2
  density = 1
  expand = 3
  formula = G4_MIX_D_WAX
  name = G4_MIX_D_WAX
  specific = 4
FEATURE [App::DocumentObjectGroupPython] H_element056  label="H_element : 0.135"  # scripted group (container) (typed FeaturePython)
  n = 0.081192
FEATURE [App::DocumentObjectGroupPython] C_element062  label="C_element : 0.583"  # scripted group (container) (typed FeaturePython)
  n = 0.583442
FEATURE [App::DocumentObjectGroupPython] N_element024  label="N_element : 0.018"  # scripted group (container) (typed FeaturePython)
  n = 0.017798
FEATURE [App::DocumentObjectGroupPython] O_element064  label="O_element : 0.186"  # scripted group (container) (typed FeaturePython)
  n = 0.186381
FEATURE [App::DocumentObjectGroupPython] Mg_element010  label="Mg_element : 0.130"  # scripted group (container) (typed FeaturePython)
  n = 0.130287
FEATURE [App::DocumentObjectGroupPython] Cl_element015  label="Cl_element : 0.588"  # scripted group (container) (typed FeaturePython)
  n = 0.0009
FEATURE [App::DocumentObjectGroupPython] G4_MS20_TISSUE  # scripted group (container) (typed FeaturePython)
  Dunit = g/cm3
  Dvalue = 1
  Group = -> [H_element056,C_element062,N_element024,O_element064,Mg_element010,Cl_element015]
  conduct = 2
  density = 1
  expand = 3
  formula = G4_MS20_TISSUE
  name = G4_MS20_TISSUE
  specific = 4
FEATURE [App::DocumentObjectGroupPython] H_element057  label="H_element : 0.136"  # scripted group (container) (typed FeaturePython)
  n = 0.102
FEATURE [App::DocumentObjectGroupPython] C_element063  label="C_element : 0.143"  # scripted group (container) (typed FeaturePython)
  n = 0.143
FEATURE [App::DocumentObjectGroupPython] N_element025  label="N_element : 0.034"  # scripted group (container) (typed FeaturePython)
  n = 0.034
FEATURE [App::DocumentObjectGroupPython] O_element065  label="O_element : 0.710"  # scripted group (container) (typed FeaturePython)
  n = 0.71
FEATURE [App::DocumentObjectGroupPython] Na_element011  label="Na_element : 0.098"  # scripted group (container) (typed FeaturePython)
  n = 0.001
FEATURE [App::DocumentObjectGroupPython] P_element007  label="P_element : 0.002"  # scripted group (container) (typed FeaturePython)
  n = 0.002
FEATURE [App::DocumentObjectGroupPython] S_element017  label="S_element : 0.018"  # scripted group (container) (typed FeaturePython)
  n = 0.003
FEATURE [App::DocumentObjectGroupPython] Cl_element016  label="Cl_element : 0.589"  # scripted group (container) (typed FeaturePython)
  n = 0.001
FEATURE [App::DocumentObjectGroupPython] K_element006  label="K_element : 0.004"  # scripted group (container) (typed FeaturePython)
  n = 0.004
FEATURE [App::DocumentObjectGroupPython] G4_MUSCLE_SKELETAL_ICRP  # scripted group (container) (typed FeaturePython)
  Dunit = g/cm3
  Dvalue = 1.05
  Group = -> [H_element057,C_element063,N_element025,O_element065,Na_element011,P_element007,S_element017,Cl_element016,K_element006]
  conduct = 2
  density = 1
  expand = 3
  formula = G4_MUSCLE_SKELETAL_ICRP
  name = G4_MUSCLE_SKELETAL_ICRP
  specific = 4
FEATURE [App::DocumentObjectGroupPython] H_element058  label="H_element : 0.137"  # scripted group (container) (typed FeaturePython)
  n = 0.102102
FEATURE [App::DocumentObjectGroupPython] C_element064  label="C_element : 0.123"  # scripted group (container) (typed FeaturePython)
  n = 0.123123
FEATURE [App::DocumentObjectGroupPython] N_element026  label="N_element : 0.756"  # scripted group (container) (typed FeaturePython)
  n = 0.035035
FEATURE [App::DocumentObjectGroupPython] O_element066  label="O_element : 0.730"  # scripted group (container) (typed FeaturePython)
  n = 0.72973
FEATURE [App::DocumentObjectGroupPython] Na_element012  label="Na_element : 0.099"  # scripted group (container) (typed FeaturePython)
  n = 0.001001
FEATURE [App::DocumentObjectGroupPython] P_element008  label="P_element : 0.106"  # scripted group (container) (typed FeaturePython)
  n = 0.002002
FEATURE [App::DocumentObjectGroupPython] S_element018  label="S_element : 0.019"  # scripted group (container) (typed FeaturePython)
  n = 0.004004
FEATURE [App::DocumentObjectGroupPython] K_element007  label="K_element : 0.016"  # scripted group (container) (typed FeaturePython)
  n = 0.003003
FEATURE [App::DocumentObjectGroupPython] G4_MUSCLE_STRIATED_ICRU  # scripted group (container) (typed FeaturePython)
  Dunit = g/cm3
  Dvalue = 1.04
  Group = -> [H_element058,C_element064,N_element026,O_element066,Na_element012,P_element008,S_element018,K_element007]
  conduct = 2
  density = 1
  expand = 3
  formula = G4_MUSCLE_STRIATED_ICRU
  name = G4_MUSCLE_STRIATED_ICRU
  specific = 4
FEATURE [App::DocumentObjectGroupPython] H_element059  label="H_element : 0.098"  # scripted group (container) (typed FeaturePython)
  n = 0.0982341
FEATURE [App::DocumentObjectGroupPython] C_element065  label="C_element : 0.156"  # scripted group (container) (typed FeaturePython)
  n = 0.156214
FEATURE [App::DocumentObjectGroupPython] N_element027  label="N_element : 0.757"  # scripted group (container) (typed FeaturePython)
  n = 0.035451
FEATURE [App::DocumentObjectGroupPython] O_element067  label="O_element : 0.880"  # scripted group (container) (typed FeaturePython)
  n = 0.710101
FEATURE [App::DocumentObjectGroupPython] G4_MUSCLE_WITH_SUCROSE  # scripted group (container) (typed FeaturePython)
  Dunit = g/cm3
  Dvalue = 1.11
  Group = -> [H_element059,C_element065,N_element027,O_element067]
  conduct = 2
  density = 1
  expand = 3
  formula = G4_MUSCLE_WITH_SUCROSE
  name = G4_MUSCLE_WITH_SUCROSE
  specific = 4
FEATURE [App::DocumentObjectGroupPython] H_element060  label="H_element : 0.138"  # scripted group (container) (typed FeaturePython)
  n = 0.101969
FEATURE [App::DocumentObjectGroupPython] C_element066  label="C_element : 0.120"  # scripted group (container) (typed FeaturePython)
  n = 0.120058
FEATURE [App::DocumentObjectGroupPython] N_element028  label="N_element : 0.758"  # scripted group (container) (typed FeaturePython)
  n = 0.035451
FEATURE [App::DocumentObjectGroupPython] O_element068  label="O_element : 0.743"  # scripted group (container) (typed FeaturePython)
  n = 0.742522
FEATURE [App::DocumentObjectGroupPython] G4_MUSCLE_WITHOUT_SUCROSE  # scripted group (container) (typed FeaturePython)
  Dunit = g/cm3
  Dvalue = 1.07
  Group = -> [H_element060,C_element066,N_element028,O_element068]
  conduct = 2
  density = 1
  expand = 3
  formula = G4_MUSCLE_WITHOUT_SUCROSE
  name = G4_MUSCLE_WITHOUT_SUCROSE
  specific = 4
FEATURE [App::DocumentObjectGroupPython] C_element067  label="C_element : 10"  # scripted group (container) (typed FeaturePython)
  n = 10
  ref = C_element
FEATURE [App::DocumentObjectGroupPython] H_element061  label="H_element : 030"  # scripted group (container) (typed FeaturePython)
  n = 8
  ref = H_element
FEATURE [App::DocumentObjectGroupPython] G4_NAPHTHALENE  # scripted group (container) (typed FeaturePython)
  Dunit = g/cm3
  Dvalue = 1.145
  Group = -> [C_element067,H_element061]
  conduct = 2
  density = 1
  expand = 3
  formula = G4_NAPHTHALENE
  name = G4_NAPHTHALENE
  specific = 4
FEATURE [App::DocumentObjectGroupPython] C_element068  label="C_element : 034"  # scripted group (container) (typed FeaturePython)
  n = 6
  ref = C_element
FEATURE [App::DocumentObjectGroupPython] H_element062  label="H_element : 031"  # scripted group (container) (typed FeaturePython)
  n = 5
  ref = H_element
FEATURE [App::DocumentObjectGroupPython] N_element029  label="N_element : 012"  # scripted group (container) (typed FeaturePython)
  n = 1
  ref = N_element
FEATURE [App::DocumentObjectGroupPython] O_element069  label="O_element : 034"  # scripted group (container) (typed FeaturePython)
  n = 2
  ref = O_element
FEATURE [App::DocumentObjectGroupPython] G4_NITROBENZENE  # scripted group (container) (typed FeaturePython)
  Dunit = g/cm3
  Dvalue = 1.19867
  Group = -> [C_element068,H_element062,N_element029,O_element069]
  conduct = 2
  density = 1
  expand = 3
  formula = G4_NITROBENZENE
  name = G4_NITROBENZENE
  specific = 4
FEATURE [App::DocumentObjectGroupPython] N_element030  label="N_element : 013"  # scripted group (container) (typed FeaturePython)
  n = 2
  ref = N_element
FEATURE [App::DocumentObjectGroupPython] O_element070  label="O_element : 035"  # scripted group (container) (typed FeaturePython)
  n = 1
  ref = O_element
FEATURE [App::DocumentObjectGroupPython] G4_NITROUS_OXIDE  # scripted group (container) (typed FeaturePython)
  Dunit = g/cm3
  Dvalue = 0.00183094
  Group = -> [N_element030,O_element070]
  conduct = 2
  density = 1
  expand = 3
  formula = G4_NITROUS_OXIDE
  name = G4_NITROUS_OXIDE
  specific = 4
FEATURE [App::DocumentObjectGroupPython] H_element063  label="H_element : 0.104"  # scripted group (container) (typed FeaturePython)
  n = 0.103509
FEATURE [App::DocumentObjectGroupPython] C_element069  label="C_element : 0.648"  # scripted group (container) (typed FeaturePython)
  n = 0.648416
FEATURE [App::DocumentObjectGroupPython] N_element031  label="N_element : 0.100"  # scripted group (container) (typed FeaturePython)
  n = 0.0995361
FEATURE [App::DocumentObjectGroupPython] O_element071  label="O_element : 0.149"  # scripted group (container) (typed FeaturePython)
  n = 0.148539
FEATURE [App::DocumentObjectGroupPython] G4_NYLON_8062  label="G4_NYLON-8062"  # scripted group (container) (typed FeaturePython)
  Dunit = g/cm3
  Dvalue = 1.08
  Group = -> [H_element063,C_element069,N_element031,O_element071]
  conduct = 2
  density = 1
  expand = 3
  formula = G4_NYLON-8062
  name = G4_NYLON-8062
  specific = 4
FEATURE [App::DocumentObjectGroupPython] C_element070  label="C_element : 035"  # scripted group (container) (typed FeaturePython)
  n = 6
  ref = C_element
FEATURE [App::DocumentObjectGroupPython] H_element064  label="H_element : 11"  # scripted group (container) (typed FeaturePython)
  n = 11
  ref = H_element
FEATURE [App::DocumentObjectGroupPython] N_element032  label="N_element : 014"  # scripted group (container) (typed FeaturePython)
  n = 1
  ref = N_element
FEATURE [App::DocumentObjectGroupPython] O_element072  label="O_element : 036"  # scripted group (container) (typed FeaturePython)
  n = 1
  ref = O_element
FEATURE [App::DocumentObjectGroupPython] G4_NYLON_6_6  label="G4_NYLON-6-6"  # scripted group (container) (typed FeaturePython)
  Dunit = g/cm3
  Dvalue = 1.14
  Group = -> [C_element070,H_element064,N_element032,O_element072]
  conduct = 2
  density = 1
  expand = 3
  formula = G4_NYLON-6-6
  name = G4_NYLON-6-6
  specific = 4
FEATURE [App::DocumentObjectGroupPython] H_element065  label="H_element : 0.139"  # scripted group (container) (typed FeaturePython)
  n = 0.107062
FEATURE [App::DocumentObjectGroupPython] C_element071  label="C_element : 0.680"  # scripted group (container) (typed FeaturePython)
  n = 0.680449
FEATURE [App::DocumentObjectGroupPython] N_element033  label="N_element : 0.099"  # scripted group (container) (typed FeaturePython)
  n = 0.099189
FEATURE [App::DocumentObjectGroupPython] O_element073  label="O_element : 0.113"  # scripted group (container) (typed FeaturePython)
  n = 0.1133
FEATURE [App::DocumentObjectGroupPython] G4_NYLON_6_10  label="G4_NYLON-6-10"  # scripted group (container) (typed FeaturePython)
  Dunit = g/cm3
  Dvalue = 1.14
  Group = -> [H_element065,C_element071,N_element033,O_element073]
  conduct = 2
  density = 1
  expand = 3
  formula = G4_NYLON-6-10
  name = G4_NYLON-6-10
  specific = 4
FEATURE [App::DocumentObjectGroupPython] H_element066  label="H_element : 0.140"  # scripted group (container) (typed FeaturePython)
  n = 0.115476
FEATURE [App::DocumentObjectGroupPython] C_element072  label="C_element : 0.721"  # scripted group (container) (typed FeaturePython)
  n = 0.720818
FEATURE [App::DocumentObjectGroupPython] N_element034  label="N_element : 0.076"  # scripted group (container) (typed FeaturePython)
  n = 0.0764169
FEATURE [App::DocumentObjectGroupPython] O_element074  label="O_element : 0.087"  # scripted group (container) (typed FeaturePython)
  n = 0.0872889
FEATURE [App::DocumentObjectGroupPython] G4_NYLON_11_RILSAN  label="G4_NYLON-11_RILSAN"  # scripted group (container) (typed FeaturePython)
  Dunit = g/cm3
  Dvalue = 1.425
  Group = -> [H_element066,C_element072,N_element034,O_element074]
  conduct = 2
  density = 1
  expand = 3
  formula = G4_NYLON-11_RILSAN
  name = G4_NYLON-11_RILSAN
  specific = 4
FEATURE [App::DocumentObjectGroupPython] C_element073  label="C_element : 8"  # scripted group (container) (typed FeaturePython)
  n = 8
  ref = C_element
FEATURE [App::DocumentObjectGroupPython] H_element067  label="H_element : 18"  # scripted group (container) (typed FeaturePython)
  n = 18
  ref = H_element
FEATURE [App::DocumentObjectGroupPython] G4_OCTANE  # scripted group (container) (typed FeaturePython)
  Dunit = g/cm3
  Dvalue = 0.7026
  Group = -> [C_element073,H_element067]
  conduct = 2
  density = 1
  expand = 3
  formula = G4_OCTANE
  name = G4_OCTANE
  specific = 4
FEATURE [App::DocumentObjectGroupPython] C_element074  label="C_element : 25"  # scripted group (container) (typed FeaturePython)
  n = 25
  ref = C_element
FEATURE [App::DocumentObjectGroupPython] H_element068  label="H_element : 52"  # scripted group (container) (typed FeaturePython)
  n = 52
  ref = H_element
FEATURE [App::DocumentObjectGroupPython] G4_PARAFFIN  # scripted group (container) (typed FeaturePython)
  Dunit = g/cm3
  Dvalue = 0.93
  Group = -> [C_element074,H_element068]
  conduct = 2
  density = 1
  expand = 3
  formula = G4_PARAFFIN
  name = G4_PARAFFIN
  specific = 4
FEATURE [App::DocumentObjectGroupPython] C_element075  label="C_element : 036"  # scripted group (container) (typed FeaturePython)
  n = 5
  ref = C_element
FEATURE [App::DocumentObjectGroupPython] H_element069  label="H_element : 032"  # scripted group (container) (typed FeaturePython)
  n = 12
  ref = H_element
FEATURE [App::DocumentObjectGroupPython] G4_N_PENTANE  label="G4_N-PENTANE"  # scripted group (container) (typed FeaturePython)
  Dunit = g/cm3
  Dvalue = 0.6262
  Group = -> [C_element075,H_element069]
  conduct = 2
  density = 1
  expand = 3
  formula = G4_N-PENTANE
  name = G4_N-PENTANE
  specific = 4
FEATURE [App::DocumentObjectGroupPython] H_element070  label="H_element : 0.014"  # scripted group (container) (typed FeaturePython)
  n = 0.0141
FEATURE [App::DocumentObjectGroupPython] C_element076  label="C_element : 0.072"  # scripted group (container) (typed FeaturePython)
  n = 0.072261
FEATURE [App::DocumentObjectGroupPython] N_element035  label="N_element : 0.019"  # scripted group (container) (typed FeaturePython)
  n = 0.01932
FEATURE [App::DocumentObjectGroupPython] O_element075  label="O_element : 0.066"  # scripted group (container) (typed FeaturePython)
  n = 0.066101
FEATURE [App::DocumentObjectGroupPython] S_element019  label="S_element : 0.020"  # scripted group (container) (typed FeaturePython)
  n = 0.00189
FEATURE [App::DocumentObjectGroupPython] Br_element004  label="Br_element : 0.349"  # scripted group (container) (typed FeaturePython)
  n = 0.349103
FEATURE [App::DocumentObjectGroupPython] Ag_element001  label="Ag_element : 0.474"  # scripted group (container) (typed FeaturePython)
  n = 0.474105
FEATURE [App::DocumentObjectGroupPython] I_element005  label="I_element : 0.003"  # scripted group (container) (typed FeaturePython)
  n = 0.00312
FEATURE [App::DocumentObjectGroupPython] G4_PHOTO_EMULSION  # scripted group (container) (typed FeaturePython)
  Dunit = g/cm3
  Dvalue = 3.815
  Group = -> [H_element070,C_element076,N_element035,O_element075,S_element019,Br_element004,Ag_element001,I_element005]
  conduct = 2
  density = 1
  expand = 3
  formula = G4_PHOTO_EMULSION
  name = G4_PHOTO_EMULSION
  specific = 4
FEATURE [App::DocumentObjectGroupPython] C_element077  label="C_element : 9"  # scripted group (container) (typed FeaturePython)
  n = 9
  ref = C_element
FEATURE [App::DocumentObjectGroupPython] H_element071  label="H_element : 033"  # scripted group (container) (typed FeaturePython)
  n = 10
  ref = H_element
FEATURE [App::DocumentObjectGroupPython] G4_PLASTIC_SC_VINYLTOLUENE  # scripted group (container) (typed FeaturePython)
  Dunit = g/cm3
  Dvalue = 1.032
  Group = -> [C_element077,H_element071]
  conduct = 2
  density = 1
  expand = 3
  formula = G4_PLASTIC_SC_VINYLTOLUENE
  name = G4_PLASTIC_SC_VINYLTOLUENE
  specific = 4
FEATURE [App::DocumentObjectGroupPython] Pu_element001  label="Pu_element : 1"  # scripted group (container) (typed FeaturePython)
  n = 1
  ref = Pu_element
FEATURE [App::DocumentObjectGroupPython] O_element076  label="O_element : 037"  # scripted group (container) (typed FeaturePython)
  n = 2
  ref = O_element
FEATURE [App::DocumentObjectGroupPython] G4_PLUTONIUM_DIOXIDE  # scripted group (container) (typed FeaturePython)
  Dunit = g/cm3
  Dvalue = 11.46
  Group = -> [Pu_element001,O_element076]
  conduct = 2
  density = 1
  expand = 3
  formula = G4_PLUTONIUM_DIOXIDE
  name = G4_PLUTONIUM_DIOXIDE
  specific = 4
FEATURE [App::DocumentObjectGroupPython] C_element078  label="C_element : 037"  # scripted group (container) (typed FeaturePython)
  n = 3
  ref = C_element
FEATURE [App::DocumentObjectGroupPython] H_element072  label="H_element : 034"  # scripted group (container) (typed FeaturePython)
  n = 3
  ref = H_element
FEATURE [App::DocumentObjectGroupPython] N_element036  label="N_element : 015"  # scripted group (container) (typed FeaturePython)
  n = 1
  ref = N_element
FEATURE [App::DocumentObjectGroupPython] G4_POLYACRYLONITRILE  # scripted group (container) (typed FeaturePython)
  Dunit = g/cm3
  Dvalue = 1.17
  Group = -> [C_element078,H_element072,N_element036]
  conduct = 2
  density = 1
  expand = 3
  formula = G4_POLYACRYLONITRILE
  name = G4_POLYACRYLONITRILE
  specific = 4
FEATURE [App::DocumentObjectGroupPython] C_element079  label="C_element : 16"  # scripted group (container) (typed FeaturePython)
  n = 16
  ref = C_element
FEATURE [App::DocumentObjectGroupPython] H_element073  label="H_element : 035"  # scripted group (container) (typed FeaturePython)
  n = 14
  ref = H_element
FEATURE [App::DocumentObjectGroupPython] O_element077  label="O_element : 038"  # scripted group (container) (typed FeaturePython)
  n = 3
  ref = O_element
FEATURE [App::DocumentObjectGroupPython] G4_POLYCARBONATE  # scripted group (container) (typed FeaturePython)
  Dunit = g/cm3
  Dvalue = 1.2
  Group = -> [C_element079,H_element073,O_element077]
  conduct = 2
  density = 1
  expand = 3
  formula = G4_POLYCARBONATE
  name = G4_POLYCARBONATE
  specific = 4
FEATURE [App::DocumentObjectGroupPython] C_element080  label="C_element : 038"  # scripted group (container) (typed FeaturePython)
  n = 8
  ref = C_element
FEATURE [App::DocumentObjectGroupPython] H_element074  label="H_element : 036"  # scripted group (container) (typed FeaturePython)
  n = 7
  ref = H_element
FEATURE [App::DocumentObjectGroupPython] Cl_element017  label="Cl_element : 007"  # scripted group (container) (typed FeaturePython)
  n = 1
  ref = Cl_element
FEATURE [App::DocumentObjectGroupPython] G4_POLYCHLOROSTYRENE  # scripted group (container) (typed FeaturePython)
  Dunit = g/cm3
  Dvalue = 1.3
  Group = -> [C_element080,H_element074,Cl_element017]
  conduct = 2
  density = 1
  expand = 3
  formula = G4_POLYCHLOROSTYRENE
  name = G4_POLYCHLOROSTYRENE
  specific = 4
FEATURE [App::DocumentObjectGroupPython] C_element081  label="C_element : 039"  # scripted group (container) (typed FeaturePython)
  n = 1
  ref = C_element
FEATURE [App::DocumentObjectGroupPython] H_element075  label="H_element : 037"  # scripted group (container) (typed FeaturePython)
  n = 2
  ref = H_element
FEATURE [App::DocumentObjectGroupPython] G4_POLYETHYLENE  # scripted group (container) (typed FeaturePython)
  Dunit = g/cm3
  Dvalue = 0.94
  Group = -> [C_element081,H_element075]
  conduct = 2
  density = 1
  expand = 3
  formula = G4_POLYETHYLENE
  name = G4_POLYETHYLENE
  specific = 4
FEATURE [App::DocumentObjectGroupPython] C_element082  label="C_element : 040"  # scripted group (container) (typed FeaturePython)
  n = 10
  ref = C_element
FEATURE [App::DocumentObjectGroupPython] H_element076  label="H_element : 038"  # scripted group (container) (typed FeaturePython)
  n = 8
  ref = H_element
FEATURE [App::DocumentObjectGroupPython] O_element078  label="O_element : 039"  # scripted group (container) (typed FeaturePython)
  n = 4
  ref = O_element
FEATURE [App::DocumentObjectGroupPython] G4_MYLAR  # scripted group (container) (typed FeaturePython)
  Dunit = g/cm3
  Dvalue = 1.4
  Group = -> [C_element082,H_element076,O_element078]
  conduct = 2
  density = 1
  expand = 3
  formula = G4_MYLAR
  name = G4_MYLAR
  specific = 4
FEATURE [App::DocumentObjectGroupPython] C_element083  label="C_element : 041"  # scripted group (container) (typed FeaturePython)
  n = 5
  ref = C_element
FEATURE [App::DocumentObjectGroupPython] H_element077  label="H_element : 039"  # scripted group (container) (typed FeaturePython)
  n = 8
  ref = H_element
FEATURE [App::DocumentObjectGroupPython] O_element079  label="O_element : 040"  # scripted group (container) (typed FeaturePython)
  n = 2
  ref = O_element
FEATURE [App::DocumentObjectGroupPython] G4_PLEXIGLASS  # scripted group (container) (typed FeaturePython)
  Dunit = g/cm3
  Dvalue = 1.19
  Group = -> [C_element083,H_element077,O_element079]
  conduct = 2
  density = 1
  expand = 3
  formula = G4_PLEXIGLASS
  name = G4_PLEXIGLASS
  specific = 4
FEATURE [App::DocumentObjectGroupPython] C_element084  label="C_element : 042"  # scripted group (container) (typed FeaturePython)
  n = 1
  ref = C_element
FEATURE [App::DocumentObjectGroupPython] H_element078  label="H_element : 040"  # scripted group (container) (typed FeaturePython)
  n = 2
  ref = H_element
FEATURE [App::DocumentObjectGroupPython] O_element080  label="O_element : 041"  # scripted group (container) (typed FeaturePython)
  n = 1
  ref = O_element
FEATURE [App::DocumentObjectGroupPython] G4_POLYOXYMETHYLENE  # scripted group (container) (typed FeaturePython)
  Dunit = g/cm3
  Dvalue = 1.425
  Group = -> [C_element084,H_element078,O_element080]
  conduct = 2
  density = 1
  expand = 3
  formula = G4_POLYOXYMETHYLENE
  name = G4_POLYOXYMETHYLENE
  specific = 4
FEATURE [App::DocumentObjectGroupPython] C_element085  label="C_element : 043"  # scripted group (container) (typed FeaturePython)
  n = 2
  ref = C_element
FEATURE [App::DocumentObjectGroupPython] H_element079  label="H_element : 041"  # scripted group (container) (typed FeaturePython)
  n = 4
  ref = H_element
FEATURE [App::DocumentObjectGroupPython] G4_POLYPROPYLENE  # scripted group (container) (typed FeaturePython)
  Dunit = g/cm3
  Dvalue = 0.9
  Group = -> [C_element085,H_element079]
  conduct = 2
  density = 1
  expand = 3
  formula = G4_POLYPROPYLENE
  name = G4_POLYPROPYLENE
  specific = 4
FEATURE [App::DocumentObjectGroupPython] C_element086  label="C_element : 044"  # scripted group (container) (typed FeaturePython)
  n = 8
  ref = C_element
FEATURE [App::DocumentObjectGroupPython] H_element080  label="H_element : 042"  # scripted group (container) (typed FeaturePython)
  n = 8
  ref = H_element
FEATURE [App::DocumentObjectGroupPython] G4_POLYSTYRENE  # scripted group (container) (typed FeaturePython)
  Dunit = g/cm3
  Dvalue = 1.06
  Group = -> [C_element086,H_element080]
  conduct = 2
  density = 1
  expand = 3
  formula = G4_POLYSTYRENE
  name = G4_POLYSTYRENE
  specific = 4
FEATURE [App::DocumentObjectGroupPython] C_element087  label="C_element : 045"  # scripted group (container) (typed FeaturePython)
  n = 2
  ref = C_element
FEATURE [App::DocumentObjectGroupPython] F_element014  label="F_element : 4"  # scripted group (container) (typed FeaturePython)
  n = 4
  ref = F_element
FEATURE [App::DocumentObjectGroupPython] G4_TEFLON  # scripted group (container) (typed FeaturePython)
  Dunit = g/cm3
  Dvalue = 2.2
  Group = -> [C_element087,F_element014]
  conduct = 2
  density = 1
  expand = 3
  formula = G4_TEFLON
  name = G4_TEFLON
  specific = 4
FEATURE [App::DocumentObjectGroupPython] C_element088  label="C_element : 046"  # scripted group (container) (typed FeaturePython)
  n = 2
  ref = C_element
FEATURE [App::DocumentObjectGroupPython] F_element015  label="F_element : 006"  # scripted group (container) (typed FeaturePython)
  n = 3
  ref = F_element
FEATURE [App::DocumentObjectGroupPython] Cl_element018  label="Cl_element : 008"  # scripted group (container) (typed FeaturePython)
  n = 1
  ref = Cl_element
FEATURE [App::DocumentObjectGroupPython] G4_POLYTRIFLUOROCHLOROETHYLENE  # scripted group (container) (typed FeaturePython)
  Dunit = g/cm3
  Dvalue = 2.1
  Group = -> [C_element088,F_element015,Cl_element018]
  conduct = 2
  density = 1
  expand = 3
  formula = G4_POLYTRIFLUOROCHLOROETHYLENE
  name = G4_POLYTRIFLUOROCHLOROETHYLENE
  specific = 4
FEATURE [App::DocumentObjectGroupPython] C_element089  label="C_element : 047"  # scripted group (container) (typed FeaturePython)
  n = 4
  ref = C_element
FEATURE [App::DocumentObjectGroupPython] H_element081  label="H_element : 043"  # scripted group (container) (typed FeaturePython)
  n = 6
  ref = H_element
FEATURE [App::DocumentObjectGroupPython] O_element081  label="O_element : 042"  # scripted group (container) (typed FeaturePython)
  n = 2
  ref = O_element
FEATURE [App::DocumentObjectGroupPython] G4_POLYVINYL_ACETATE  # scripted group (container) (typed FeaturePython)
  Dunit = g/cm3
  Dvalue = 1.19
  Group = -> [C_element089,H_element081,O_element081]
  conduct = 2
  density = 1
  expand = 3
  formula = G4_POLYVINYL_ACETATE
  name = G4_POLYVINYL_ACETATE
  specific = 4
FEATURE [App::DocumentObjectGroupPython] C_element090  label="C_element : 048"  # scripted group (container) (typed FeaturePython)
  n = 2
  ref = C_element
FEATURE [App::DocumentObjectGroupPython] H_element082  label="H_element : 044"  # scripted group (container) (typed FeaturePython)
  n = 4
  ref = H_element
FEATURE [App::DocumentObjectGroupPython] O_element082  label="O_element : 043"  # scripted group (container) (typed FeaturePython)
  n = 1
  ref = O_element
FEATURE [App::DocumentObjectGroupPython] G4_POLYVINYL_ALCOHOL  # scripted group (container) (typed FeaturePython)
  Dunit = g/cm3
  Dvalue = 1.3
  Group = -> [C_element090,H_element082,O_element082]
  conduct = 2
  density = 1
  expand = 3
  formula = G4_POLYVINYL_ALCOHOL
  name = G4_POLYVINYL_ALCOHOL
  specific = 4
FEATURE [App::DocumentObjectGroupPython] C_element091  label="C_element : 049"  # scripted group (container) (typed FeaturePython)
  n = 8
  ref = C_element
FEATURE [App::DocumentObjectGroupPython] H_element083  label="H_element : 045"  # scripted group (container) (typed FeaturePython)
  n = 14
  ref = H_element
FEATURE [App::DocumentObjectGroupPython] O_element083  label="O_element : 044"  # scripted group (container) (typed FeaturePython)
  n = 2
  ref = O_element
FEATURE [App::DocumentObjectGroupPython] G4_POLYVINYL_BUTYRAL  # scripted group (container) (typed FeaturePython)
  Dunit = g/cm3
  Dvalue = 1.12
  Group = -> [C_element091,H_element083,O_element083]
  conduct = 2
  density = 1
  expand = 3
  formula = G4_POLYVINYL_BUTYRAL
  name = G4_POLYVINYL_BUTYRAL
  specific = 4
FEATURE [App::DocumentObjectGroupPython] C_element092  label="C_element : 050"  # scripted group (container) (typed FeaturePython)
  n = 2
  ref = C_element
FEATURE [App::DocumentObjectGroupPython] H_element084  label="H_element : 046"  # scripted group (container) (typed FeaturePython)
  n = 3
  ref = H_element
FEATURE [App::DocumentObjectGroupPython] Cl_element019  label="Cl_element : 009"  # scripted group (container) (typed FeaturePython)
  n = 1
  ref = Cl_element
FEATURE [App::DocumentObjectGroupPython] G4_POLYVINYL_CHLORIDE  # scripted group (container) (typed FeaturePython)
  Dunit = g/cm3
  Dvalue = 1.3
  Group = -> [C_element092,H_element084,Cl_element019]
  conduct = 2
  density = 1
  expand = 3
  formula = G4_POLYVINYL_CHLORIDE
  name = G4_POLYVINYL_CHLORIDE
  specific = 4
FEATURE [App::DocumentObjectGroupPython] C_element093  label="C_element : 051"  # scripted group (container) (typed FeaturePython)
  n = 2
  ref = C_element
FEATURE [App::DocumentObjectGroupPython] H_element085  label="H_element : 047"  # scripted group (container) (typed FeaturePython)
  n = 2
  ref = H_element
FEATURE [App::DocumentObjectGroupPython] Cl_element020  label="Cl_element : 010"  # scripted group (container) (typed FeaturePython)
  n = 2
  ref = Cl_element
FEATURE [App::DocumentObjectGroupPython] G4_POLYVINYLIDENE_CHLORIDE  # scripted group (container) (typed FeaturePython)
  Dunit = g/cm3
  Dvalue = 1.7
  Group = -> [C_element093,H_element085,Cl_element020]
  conduct = 2
  density = 1
  expand = 3
  formula = G4_POLYVINYLIDENE_CHLORIDE
  name = G4_POLYVINYLIDENE_CHLORIDE
  specific = 4
FEATURE [App::DocumentObjectGroupPython] C_element094  label="C_element : 052"  # scripted group (container) (typed FeaturePython)
  n = 2
  ref = C_element
FEATURE [App::DocumentObjectGroupPython] H_element086  label="H_element : 048"  # scripted group (container) (typed FeaturePython)
  n = 2
  ref = H_element
FEATURE [App::DocumentObjectGroupPython] F_element016  label="F_element : 007"  # scripted group (container) (typed FeaturePython)
  n = 2
  ref = F_element
FEATURE [App::DocumentObjectGroupPython] G4_POLYVINYLIDENE_FLUORIDE  # scripted group (container) (typed FeaturePython)
  Dunit = g/cm3
  Dvalue = 1.76
  Group = -> [C_element094,H_element086,F_element016]
  conduct = 2
  density = 1
  expand = 3
  formula = G4_POLYVINYLIDENE_FLUORIDE
  name = G4_POLYVINYLIDENE_FLUORIDE
  specific = 4
FEATURE [App::DocumentObjectGroupPython] C_element095  label="C_element : 053"  # scripted group (container) (typed FeaturePython)
  n = 6
  ref = C_element
FEATURE [App::DocumentObjectGroupPython] H_element087  label="H_element : 9"  # scripted group (container) (typed FeaturePython)
  n = 9
  ref = H_element
FEATURE [App::DocumentObjectGroupPython] N_element037  label="N_element : 016"  # scripted group (container) (typed FeaturePython)
  n = 1
  ref = N_element
FEATURE [App::DocumentObjectGroupPython] O_element084  label="O_element : 045"  # scripted group (container) (typed FeaturePython)
  n = 1
  ref = O_element
FEATURE [App::DocumentObjectGroupPython] G4_POLYVINYL_PYRROLIDONE  # scripted group (container) (typed FeaturePython)
  Dunit = g/cm3
  Dvalue = 1.25
  Group = -> [C_element095,H_element087,N_element037,O_element084]
  conduct = 2
  density = 1
  expand = 3
  formula = G4_POLYVINYL_PYRROLIDONE
  name = G4_POLYVINYL_PYRROLIDONE
  specific = 4
FEATURE [App::DocumentObjectGroupPython] K_element008  label="K_element : 1"  # scripted group (container) (typed FeaturePython)
  n = 1
  ref = K_element
FEATURE [App::DocumentObjectGroupPython] I_element006  label="I_element : 003"  # scripted group (container) (typed FeaturePython)
  n = 1
  ref = I_element
FEATURE [App::DocumentObjectGroupPython] G4_POTASSIUM_IODIDE  # scripted group (container) (typed FeaturePython)
  Dunit = g/cm3
  Dvalue = 3.13
  Group = -> [K_element008,I_element006]
  conduct = 2
  density = 1
  expand = 3
  formula = G4_POTASSIUM_IODIDE
  name = G4_POTASSIUM_IODIDE
  specific = 4
FEATURE [App::DocumentObjectGroupPython] K_element009  label="K_element : 2"  # scripted group (container) (typed FeaturePython)
  n = 2
  ref = K_element
FEATURE [App::DocumentObjectGroupPython] O_element085  label="O_element : 046"  # scripted group (container) (typed FeaturePython)
  n = 1
  ref = O_element
FEATURE [App::DocumentObjectGroupPython] G4_POTASSIUM_OXIDE  # scripted group (container) (typed FeaturePython)
  Dunit = g/cm3
  Dvalue = 2.32
  Group = -> [K_element009,O_element085]
  conduct = 2
  density = 1
  expand = 3
  formula = G4_POTASSIUM_OXIDE
  name = G4_POTASSIUM_OXIDE
  specific = 4
FEATURE [App::DocumentObjectGroupPython] C_element096  label="C_element : 054"  # scripted group (container) (typed FeaturePython)
  n = 3
  ref = C_element
FEATURE [App::DocumentObjectGroupPython] H_element088  label="H_element : 049"  # scripted group (container) (typed FeaturePython)
  n = 8
  ref = H_element
FEATURE [App::DocumentObjectGroupPython] G4_PROPANE  # scripted group (container) (typed FeaturePython)
  Dunit = g/cm3
  Dvalue = 0.00187939
  Group = -> [C_element096,H_element088]
  conduct = 2
  density = 1
  expand = 3
  formula = G4_PROPANE
  name = G4_PROPANE
  specific = 4
FEATURE [App::DocumentObjectGroupPython] C_element097  label="C_element : 055"  # scripted group (container) (typed FeaturePython)
  n = 3
  ref = C_element
FEATURE [App::DocumentObjectGroupPython] H_element089  label="H_element : 050"  # scripted group (container) (typed FeaturePython)
  n = 8
  ref = H_element
FEATURE [App::DocumentObjectGroupPython] G4_lPROPANE  # scripted group (container) (typed FeaturePython)
  Dunit = g/cm3
  Dvalue = 0.43
  Group = -> [C_element097,H_element089]
  conduct = 2
  density = 1
  expand = 3
  formula = G4_lPROPANE
  name = G4_lPROPANE
  specific = 4
FEATURE [App::DocumentObjectGroupPython] C_element098  label="C_element : 056"  # scripted group (container) (typed FeaturePython)
  n = 3
  ref = C_element
FEATURE [App::DocumentObjectGroupPython] H_element090  label="H_element : 051"  # scripted group (container) (typed FeaturePython)
  n = 8
  ref = H_element
FEATURE [App::DocumentObjectGroupPython] O_element086  label="O_element : 047"  # scripted group (container) (typed FeaturePython)
  n = 1
  ref = O_element
FEATURE [App::DocumentObjectGroupPython] G4_N_PROPYL_ALCOHOL  label="G4_N-PROPYL_ALCOHOL"  # scripted group (container) (typed FeaturePython)
  Dunit = g/cm3
  Dvalue = 0.8035
  Group = -> [C_element098,H_element090,O_element086]
  conduct = 2
  density = 1
  expand = 3
  formula = G4_N-PROPYL_ALCOHOL
  name = G4_N-PROPYL_ALCOHOL
  specific = 4
FEATURE [App::DocumentObjectGroupPython] C_element099  label="C_element : 057"  # scripted group (container) (typed FeaturePython)
  n = 5
  ref = C_element
FEATURE [App::DocumentObjectGroupPython] H_element091  label="H_element : 052"  # scripted group (container) (typed FeaturePython)
  n = 5
  ref = H_element
FEATURE [App::DocumentObjectGroupPython] N_element038  label="N_element : 017"  # scripted group (container) (typed FeaturePython)
  n = 1
  ref = N_element
FEATURE [App::DocumentObjectGroupPython] G4_PYRIDINE  # scripted group (container) (typed FeaturePython)
  Dunit = g/cm3
  Dvalue = 0.9819
  Group = -> [C_element099,H_element091,N_element038]
  conduct = 2
  density = 1
  expand = 3
  formula = G4_PYRIDINE
  name = G4_PYRIDINE
  specific = 4
FEATURE [App::DocumentObjectGroupPython] H_element092  label="H_element : 0.144"  # scripted group (container) (typed FeaturePython)
  n = 0.143711
FEATURE [App::DocumentObjectGroupPython] C_element100  label="C_element : 0.856"  # scripted group (container) (typed FeaturePython)
  n = 0.856289
FEATURE [App::DocumentObjectGroupPython] G4_RUBBER_BUTYL  # scripted group (container) (typed FeaturePython)
  Dunit = g/cm3
  Dvalue = 0.92
  Group = -> [H_element092,C_element100]
  conduct = 2
  density = 1
  expand = 3
  formula = G4_RUBBER_BUTYL
  name = G4_RUBBER_BUTYL
  specific = 4
FEATURE [App::DocumentObjectGroupPython] H_element093  label="H_element : 0.118"  # scripted group (container) (typed FeaturePython)
  n = 0.118371
FEATURE [App::DocumentObjectGroupPython] C_element101  label="C_element : 0.882"  # scripted group (container) (typed FeaturePython)
  n = 0.881629
FEATURE [App::DocumentObjectGroupPython] G4_RUBBER_NATURAL  # scripted group (container) (typed FeaturePython)
  Dunit = g/cm3
  Dvalue = 0.92
  Group = -> [H_element093,C_element101]
  conduct = 2
  density = 1
  expand = 3
  formula = G4_RUBBER_NATURAL
  name = G4_RUBBER_NATURAL
  specific = 4
FEATURE [App::DocumentObjectGroupPython] H_element094  label="H_element : 0.145"  # scripted group (container) (typed FeaturePython)
  n = 0.05692
FEATURE [App::DocumentObjectGroupPython] C_element102  label="C_element : 0.543"  # scripted group (container) (typed FeaturePython)
  n = 0.542646
FEATURE [App::DocumentObjectGroupPython] Cl_element021  label="Cl_element : 0.400"  # scripted group (container) (typed FeaturePython)
  n = 0.400434
FEATURE [App::DocumentObjectGroupPython] G4_RUBBER_NEOPRENE  # scripted group (container) (typed FeaturePython)
  Dunit = g/cm3
  Dvalue = 1.23
  Group = -> [H_element094,C_element102,Cl_element021]
  conduct = 2
  density = 1
  expand = 3
  formula = G4_RUBBER_NEOPRENE
  name = G4_RUBBER_NEOPRENE
  specific = 4
FEATURE [App::DocumentObjectGroupPython] Si_element006  label="Si_element : 1"  # scripted group (container) (typed FeaturePython)
  n = 1
  ref = Si_element
FEATURE [App::DocumentObjectGroupPython] O_element087  label="O_element : 048"  # scripted group (container) (typed FeaturePython)
  n = 2
  ref = O_element
FEATURE [App::DocumentObjectGroupPython] G4_SILICON_DIOXIDE  # scripted group (container) (typed FeaturePython)
  Dunit = g/cm3
  Dvalue = 2.32
  Group = -> [Si_element006,O_element087]
  conduct = 2
  density = 1
  expand = 3
  formula = G4_SILICON_DIOXIDE
  name = G4_SILICON_DIOXIDE
  specific = 4
FEATURE [App::DocumentObjectGroupPython] Ag_element002  label="Ag_element : 1"  # scripted group (container) (typed FeaturePython)
  n = 1
  ref = Ag_element
FEATURE [App::DocumentObjectGroupPython] Br_element005  label="Br_element : 003"  # scripted group (container) (typed FeaturePython)
  n = 1
  ref = Br_element
FEATURE [App::DocumentObjectGroupPython] G4_SILVER_BROMIDE  # scripted group (container) (typed FeaturePython)
  Dunit = g/cm3
  Dvalue = 6.473
  Group = -> [Ag_element002,Br_element005]
  conduct = 2
  density = 1
  expand = 3
  formula = G4_SILVER_BROMIDE
  name = G4_SILVER_BROMIDE
  specific = 4
FEATURE [App::DocumentObjectGroupPython] Ag_element003  label="Ag_element : 002"  # scripted group (container) (typed FeaturePython)
  n = 1
  ref = Ag_element
FEATURE [App::DocumentObjectGroupPython] Cl_element022  label="Cl_element : 011"  # scripted group (container) (typed FeaturePython)
  n = 1
  ref = Cl_element
FEATURE [App::DocumentObjectGroupPython] G4_SILVER_CHLORIDE  # scripted group (container) (typed FeaturePython)
  Dunit = g/cm3
  Dvalue = 5.56
  Group = -> [Ag_element003,Cl_element022]
  conduct = 2
  density = 1
  expand = 3
  formula = G4_SILVER_CHLORIDE
  name = G4_SILVER_CHLORIDE
  specific = 4
FEATURE [App::DocumentObjectGroupPython] Br_element006  label="Br_element : 0.423"  # scripted group (container) (typed FeaturePython)
  n = 0.422895
FEATURE [App::DocumentObjectGroupPython] Ag_element004  label="Ag_element : 0.574"  # scripted group (container) (typed FeaturePython)
  n = 0.573748
FEATURE [App::DocumentObjectGroupPython] I_element007  label="I_element : 0.649"  # scripted group (container) (typed FeaturePython)
  n = 0.003357
FEATURE [App::DocumentObjectGroupPython] G4_SILVER_HALIDES  # scripted group (container) (typed FeaturePython)
  Dunit = g/cm3
  Dvalue = 6.47
  Group = -> [Br_element006,Ag_element004,I_element007]
  conduct = 2
  density = 1
  expand = 3
  formula = G4_SILVER_HALIDES
  name = G4_SILVER_HALIDES
  specific = 4
FEATURE [App::DocumentObjectGroupPython] Ag_element005  label="Ag_element : 003"  # scripted group (container) (typed FeaturePython)
  n = 1
  ref = Ag_element
FEATURE [App::DocumentObjectGroupPython] I_element008  label="I_element : 004"  # scripted group (container) (typed FeaturePython)
  n = 1
  ref = I_element
FEATURE [App::DocumentObjectGroupPython] G4_SILVER_IODIDE  # scripted group (container) (typed FeaturePython)
  Dunit = g/cm3
  Dvalue = 6.01
  Group = -> [Ag_element005,I_element008]
  conduct = 2
  density = 1
  expand = 3
  formula = G4_SILVER_IODIDE
  name = G4_SILVER_IODIDE
  specific = 4
FEATURE [App::DocumentObjectGroupPython] H_element095  label="H_element : 0.100"  # scripted group (container) (typed FeaturePython)
  n = 0.1
FEATURE [App::DocumentObjectGroupPython] C_element103  label="C_element : 0.204"  # scripted group (container) (typed FeaturePython)
  n = 0.204
FEATURE [App::DocumentObjectGroupPython] N_element039  label="N_element : 0.759"  # scripted group (container) (typed FeaturePython)
  n = 0.042
FEATURE [App::DocumentObjectGroupPython] O_element088  label="O_element : 0.645"  # scripted group (container) (typed FeaturePython)
  n = 0.645
FEATURE [App::DocumentObjectGroupPython] Na_element013  label="Na_element : 0.100"  # scripted group (container) (typed FeaturePython)
  n = 0.002
FEATURE [App::DocumentObjectGroupPython] P_element009  label="P_element : 0.107"  # scripted group (container) (typed FeaturePython)
  n = 0.001
FEATURE [App::DocumentObjectGroupPython] S_element020  label="S_element : 0.021"  # scripted group (container) (typed FeaturePython)
  n = 0.002
FEATURE [App::DocumentObjectGroupPython] Cl_element023  label="Cl_element : 0.590"  # scripted group (container) (typed FeaturePython)
  n = 0.003
FEATURE [App::DocumentObjectGroupPython] K_element010  label="K_element : 0.001"  # scripted group (container) (typed FeaturePython)
  n = 0.001
FEATURE [App::DocumentObjectGroupPython] G4_SKIN_ICRP  # scripted group (container) (typed FeaturePython)
  Dunit = g/cm3
  Dvalue = 1.09
  Group = -> [H_element095,C_element103,N_element039,O_element088,Na_element013,P_element009,S_element020,Cl_element023,K_element010]
  conduct = 2
  density = 1
  expand = 3
  formula = G4_SKIN_ICRP
  name = G4_SKIN_ICRP
  specific = 4
FEATURE [App::DocumentObjectGroupPython] Na_element014  label="Na_element : 2"  # scripted group (container) (typed FeaturePython)
  n = 2
  ref = Na_element
FEATURE [App::DocumentObjectGroupPython] C_element104  label="C_element : 058"  # scripted group (container) (typed FeaturePython)
  n = 1
  ref = C_element
FEATURE [App::DocumentObjectGroupPython] O_element089  label="O_element : 049"  # scripted group (container) (typed FeaturePython)
  n = 3
  ref = O_element
FEATURE [App::DocumentObjectGroupPython] G4_SODIUM_CARBONATE  # scripted group (container) (typed FeaturePython)
  Dunit = g/cm3
  Dvalue = 2.532
  Group = -> [Na_element014,C_element104,O_element089]
  conduct = 2
  density = 1
  expand = 3
  formula = G4_SODIUM_CARBONATE
  name = G4_SODIUM_CARBONATE
  specific = 4
FEATURE [App::DocumentObjectGroupPython] Na_element015  label="Na_element : 1"  # scripted group (container) (typed FeaturePython)
  n = 1
  ref = Na_element
FEATURE [App::DocumentObjectGroupPython] I_element009  label="I_element : 005"  # scripted group (container) (typed FeaturePython)
  n = 1
  ref = I_element
FEATURE [App::DocumentObjectGroupPython] G4_SODIUM_IODIDE  # scripted group (container) (typed FeaturePython)
  Dunit = g/cm3
  Dvalue = 3.667
  Group = -> [Na_element015,I_element009]
  conduct = 2
  density = 1
  expand = 3
  formula = G4_SODIUM_IODIDE
  name = G4_SODIUM_IODIDE
  specific = 4
FEATURE [App::DocumentObjectGroupPython] Na_element016  label="Na_element : 003"  # scripted group (container) (typed FeaturePython)
  n = 2
  ref = Na_element
FEATURE [App::DocumentObjectGroupPython] O_element090  label="O_element : 050"  # scripted group (container) (typed FeaturePython)
  n = 1
  ref = O_element
FEATURE [App::DocumentObjectGroupPython] G4_SODIUM_MONOXIDE  # scripted group (container) (typed FeaturePython)
  Dunit = g/cm3
  Dvalue = 2.27
  Group = -> [Na_element016,O_element090]
  conduct = 2
  density = 1
  expand = 3
  formula = G4_SODIUM_MONOXIDE
  name = G4_SODIUM_MONOXIDE
  specific = 4
FEATURE [App::DocumentObjectGroupPython] Na_element017  label="Na_element : 004"  # scripted group (container) (typed FeaturePython)
  n = 1
  ref = Na_element
FEATURE [App::DocumentObjectGroupPython] N_element040  label="N_element : 018"  # scripted group (container) (typed FeaturePython)
  n = 1
  ref = N_element
FEATURE [App::DocumentObjectGroupPython] O_element091  label="O_element : 051"  # scripted group (container) (typed FeaturePython)
  n = 3
  ref = O_element
FEATURE [App::DocumentObjectGroupPython] G4_SODIUM_NITRATE  # scripted group (container) (typed FeaturePython)
  Dunit = g/cm3
  Dvalue = 2.261
  Group = -> [Na_element017,N_element040,O_element091]
  conduct = 2
  density = 1
  expand = 3
  formula = G4_SODIUM_NITRATE
  name = G4_SODIUM_NITRATE
  specific = 4
FEATURE [App::DocumentObjectGroupPython] C_element105  label="C_element : 059"  # scripted group (container) (typed FeaturePython)
  n = 14
  ref = C_element
FEATURE [App::DocumentObjectGroupPython] H_element096  label="H_element : 053"  # scripted group (container) (typed FeaturePython)
  n = 12
  ref = H_element
FEATURE [App::DocumentObjectGroupPython] G4_STILBENE  # scripted group (container) (typed FeaturePython)
  Dunit = g/cm3
  Dvalue = 0.9707
  Group = -> [C_element105,H_element096]
  conduct = 2
  density = 1
  expand = 3
  formula = G4_STILBENE
  name = G4_STILBENE
  specific = 4
FEATURE [App::DocumentObjectGroupPython] C_element106  label="C_element : 12"  # scripted group (container) (typed FeaturePython)
  n = 12
  ref = C_element
FEATURE [App::DocumentObjectGroupPython] H_element097  label="H_element : 22"  # scripted group (container) (typed FeaturePython)
  n = 22
  ref = H_element
FEATURE [App::DocumentObjectGroupPython] O_element092  label="O_element : 11"  # scripted group (container) (typed FeaturePython)
  n = 11
  ref = O_element
FEATURE [App::DocumentObjectGroupPython] G4_SUCROSE  # scripted group (container) (typed FeaturePython)
  Dunit = g/cm3
  Dvalue = 1.5805
  Group = -> [C_element106,H_element097,O_element092]
  conduct = 2
  density = 1
  expand = 3
  formula = G4_SUCROSE
  name = G4_SUCROSE
  specific = 4
FEATURE [App::DocumentObjectGroupPython] C_element107  label="C_element : 18"  # scripted group (container) (typed FeaturePython)
  n = 18
  ref = C_element
FEATURE [App::DocumentObjectGroupPython] H_element098  label="H_element : 054"  # scripted group (container) (typed FeaturePython)
  n = 14
  ref = H_element
FEATURE [App::DocumentObjectGroupPython] G4_TERPHENYL  # scripted group (container) (typed FeaturePython)
  Dunit = g/cm3
  Dvalue = 1.24
  Group = -> [C_element107,H_element098]
  conduct = 2
  density = 1
  expand = 3
  formula = G4_TERPHENYL
  name = G4_TERPHENYL
  specific = 4
FEATURE [App::DocumentObjectGroupPython] H_element099  label="H_element : 0.146"  # scripted group (container) (typed FeaturePython)
  n = 0.106
FEATURE [App::DocumentObjectGroupPython] C_element108  label="C_element : 0.883"  # scripted group (container) (typed FeaturePython)
  n = 0.099
FEATURE [App::DocumentObjectGroupPython] N_element041  label="N_element : 0.020"  # scripted group (container) (typed FeaturePython)
  n = 0.02
FEATURE [App::DocumentObjectGroupPython] O_element093  label="O_element : 0.766"  # scripted group (container) (typed FeaturePython)
  n = 0.766
FEATURE [App::DocumentObjectGroupPython] Na_element018  label="Na_element : 0.101"  # scripted group (container) (typed FeaturePython)
  n = 0.002
FEATURE [App::DocumentObjectGroupPython] P_element010  label="P_element : 0.108"  # scripted group (container) (typed FeaturePython)
  n = 0.001
FEATURE [App::DocumentObjectGroupPython] S_element021  label="S_element : 0.022"  # scripted group (container) (typed FeaturePython)
  n = 0.002
FEATURE [App::DocumentObjectGroupPython] Cl_element024  label="Cl_element : 0.002"  # scripted group (container) (typed FeaturePython)
  n = 0.002
FEATURE [App::DocumentObjectGroupPython] K_element011  label="K_element : 0.017"  # scripted group (container) (typed FeaturePython)
  n = 0.002
FEATURE [App::DocumentObjectGroupPython] G4_TESTIS_ICRP  # scripted group (container) (typed FeaturePython)
  Dunit = g/cm3
  Dvalue = 1.04
  Group = -> [H_element099,C_element108,N_element041,O_element093,Na_element018,P_element010,S_element021,Cl_element024,K_element011]
  conduct = 2
  density = 1
  expand = 3
  formula = G4_TESTIS_ICRP
  name = G4_TESTIS_ICRP
  specific = 4
FEATURE [App::DocumentObjectGroupPython] C_element109  label="C_element : 060"  # scripted group (container) (typed FeaturePython)
  n = 2
  ref = C_element
FEATURE [App::DocumentObjectGroupPython] Cl_element025  label="Cl_element : 012"  # scripted group (container) (typed FeaturePython)
  n = 4
  ref = Cl_element
FEATURE [App::DocumentObjectGroupPython] G4_TETRACHLOROETHYLENE  # scripted group (container) (typed FeaturePython)
  Dunit = g/cm3
  Dvalue = 1.625
  Group = -> [C_element109,Cl_element025]
  conduct = 2
  density = 1
  expand = 3
  formula = G4_TETRACHLOROETHYLENE
  name = G4_TETRACHLOROETHYLENE
  specific = 4
FEATURE [App::DocumentObjectGroupPython] Tl_element001  label="Tl_element : 1"  # scripted group (container) (typed FeaturePython)
  n = 1
  ref = Tl_element
FEATURE [App::DocumentObjectGroupPython] Cl_element026  label="Cl_element : 013"  # scripted group (container) (typed FeaturePython)
  n = 1
  ref = Cl_element
FEATURE [App::DocumentObjectGroupPython] G4_THALLIUM_CHLORIDE  # scripted group (container) (typed FeaturePython)
  Dunit = g/cm3
  Dvalue = 7.004
  Group = -> [Tl_element001,Cl_element026]
  conduct = 2
  density = 1
  expand = 3
  formula = G4_THALLIUM_CHLORIDE
  name = G4_THALLIUM_CHLORIDE
  specific = 4
FEATURE [App::DocumentObjectGroupPython] H_element100  label="H_element : 0.147"  # scripted group (container) (typed FeaturePython)
  n = 0.105
FEATURE [App::DocumentObjectGroupPython] C_element110  label="C_element : 0.256"  # scripted group (container) (typed FeaturePython)
  n = 0.256
FEATURE [App::DocumentObjectGroupPython] N_element042  label="N_element : 0.760"  # scripted group (container) (typed FeaturePython)
  n = 0.027
FEATURE [App::DocumentObjectGroupPython] O_element094  label="O_element : 0.602"  # scripted group (container) (typed FeaturePython)
  n = 0.602
FEATURE [App::DocumentObjectGroupPython] Na_element019  label="Na_element : 0.102"  # scripted group (container) (typed FeaturePython)
  n = 0.001
FEATURE [App::DocumentObjectGroupPython] P_element011  label="P_element : 0.109"  # scripted group (container) (typed FeaturePython)
  n = 0.002
FEATURE [App::DocumentObjectGroupPython] S_element022  label="S_element : 0.023"  # scripted group (container) (typed FeaturePython)
  n = 0.003
FEATURE [App::DocumentObjectGroupPython] Cl_element027  label="Cl_element : 0.591"  # scripted group (container) (typed FeaturePython)
  n = 0.002
FEATURE [App::DocumentObjectGroupPython] K_element012  label="K_element : 0.018"  # scripted group (container) (typed FeaturePython)
  n = 0.002
FEATURE [App::DocumentObjectGroupPython] G4_TISSUE_SOFT_ICRP  # scripted group (container) (typed FeaturePython)
  Dunit = g/cm3
  Dvalue = 1.03
  Group = -> [H_element100,C_element110,N_element042,O_element094,Na_element019,P_element011,S_element022,Cl_element027,K_element012]
  conduct = 2
  density = 1
  expand = 3
  formula = G4_TISSUE_SOFT_ICRP
  name = G4_TISSUE_SOFT_ICRP
  specific = 4
FEATURE [App::DocumentObjectGroupPython] H_element101  label="H_element : 0.148"  # scripted group (container) (typed FeaturePython)
  n = 0.101
FEATURE [App::DocumentObjectGroupPython] C_element111  label="C_element : 0.111"  # scripted group (container) (typed FeaturePython)
  n = 0.111
FEATURE [App::DocumentObjectGroupPython] N_element043  label="N_element : 0.026"  # scripted group (container) (typed FeaturePython)
  n = 0.026
FEATURE [App::DocumentObjectGroupPython] O_element095  label="O_element : 0.762"  # scripted group (container) (typed FeaturePython)
  n = 0.762
FEATURE [App::DocumentObjectGroupPython] G4_TISSUE_SOFT_ICRU_4  label="G4_TISSUE_SOFT_ICRU-4"  # scripted group (container) (typed FeaturePython)
  Dunit = g/cm3
  Dvalue = 1
  Group = -> [H_element101,C_element111,N_element043,O_element095]
  conduct = 2
  density = 1
  expand = 3
  formula = G4_TISSUE_SOFT_ICRU-4
  name = G4_TISSUE_SOFT_ICRU-4
  specific = 4
FEATURE [App::DocumentObjectGroupPython] H_element102  label="H_element : 0.149"  # scripted group (container) (typed FeaturePython)
  n = 0.101869
FEATURE [App::DocumentObjectGroupPython] C_element112  label="C_element : 0.456"  # scripted group (container) (typed FeaturePython)
  n = 0.456179
FEATURE [App::DocumentObjectGroupPython] N_element044  label="N_element : 0.761"  # scripted group (container) (typed FeaturePython)
  n = 0.035172
FEATURE [App::DocumentObjectGroupPython] O_element096  label="O_element : 0.407"  # scripted group (container) (typed FeaturePython)
  n = 0.40678
FEATURE [App::DocumentObjectGroupPython] G4_TISSUE_METHANE  label="G4_TISSUE-METHANE"  # scripted group (container) (typed FeaturePython)
  Dunit = g/cm3
  Dvalue = 0.00106409
  Group = -> [H_element102,C_element112,N_element044,O_element096]
  conduct = 2
  density = 1
  expand = 3
  formula = G4_TISSUE-METHANE
  name = G4_TISSUE-METHANE
  specific = 4
FEATURE [App::DocumentObjectGroupPython] H_element103  label="H_element : 0.103"  # scripted group (container) (typed FeaturePython)
  n = 0.102672
FEATURE [App::DocumentObjectGroupPython] C_element113  label="C_element : 0.569"  # scripted group (container) (typed FeaturePython)
  n = 0.56894
FEATURE [App::DocumentObjectGroupPython] N_element045  label="N_element : 0.762"  # scripted group (container) (typed FeaturePython)
  n = 0.035022
FEATURE [App::DocumentObjectGroupPython] O_element097  label="O_element : 0.293"  # scripted group (container) (typed FeaturePython)
  n = 0.293366
FEATURE [App::DocumentObjectGroupPython] G4_TISSUE_PROPANE  label="G4_TISSUE-PROPANE"  # scripted group (container) (typed FeaturePython)
  Dunit = g/cm3
  Dvalue = 0.00182628
  Group = -> [H_element103,C_element113,N_element045,O_element097]
  conduct = 2
  density = 1
  expand = 3
  formula = G4_TISSUE-PROPANE
  name = G4_TISSUE-PROPANE
  specific = 4
FEATURE [App::DocumentObjectGroupPython] Ti_element003  label="Ti_element : 1"  # scripted group (container) (typed FeaturePython)
  n = 1
  ref = Ti_element
FEATURE [App::DocumentObjectGroupPython] O_element098  label="O_element : 052"  # scripted group (container) (typed FeaturePython)
  n = 2
  ref = O_element
FEATURE [App::DocumentObjectGroupPython] G4_TITANIUM_DIOXIDE  # scripted group (container) (typed FeaturePython)
  Dunit = g/cm3
  Dvalue = 4.26
  Group = -> [Ti_element003,O_element098]
  conduct = 2
  density = 1
  expand = 3
  formula = G4_TITANIUM_DIOXIDE
  name = G4_TITANIUM_DIOXIDE
  specific = 4
FEATURE [App::DocumentObjectGroupPython] C_element114  label="C_element : 061"  # scripted group (container) (typed FeaturePython)
  n = 7
  ref = C_element
FEATURE [App::DocumentObjectGroupPython] H_element104  label="H_element : 055"  # scripted group (container) (typed FeaturePython)
  n = 8
  ref = H_element
FEATURE [App::DocumentObjectGroupPython] G4_TOLUENE  # scripted group (container) (typed FeaturePython)
  Dunit = g/cm3
  Dvalue = 0.8669
  Group = -> [C_element114,H_element104]
  conduct = 2
  density = 1
  expand = 3
  formula = G4_TOLUENE
  name = G4_TOLUENE
  specific = 4
FEATURE [App::DocumentObjectGroupPython] C_element115  label="C_element : 062"  # scripted group (container) (typed FeaturePython)
  n = 2
  ref = C_element
FEATURE [App::DocumentObjectGroupPython] H_element105  label="H_element : 056"  # scripted group (container) (typed FeaturePython)
  n = 1
  ref = H_element
FEATURE [App::DocumentObjectGroupPython] Cl_element028  label="Cl_element : 014"  # scripted group (container) (typed FeaturePython)
  n = 3
  ref = Cl_element
FEATURE [App::DocumentObjectGroupPython] G4_TRICHLOROETHYLENE  # scripted group (container) (typed FeaturePython)
  Dunit = g/cm3
  Dvalue = 1.46
  Group = -> [C_element115,H_element105,Cl_element028]
  conduct = 2
  density = 1
  expand = 3
  formula = G4_TRICHLOROETHYLENE
  name = G4_TRICHLOROETHYLENE
  specific = 4
FEATURE [App::DocumentObjectGroupPython] C_element116  label="C_element : 063"  # scripted group (container) (typed FeaturePython)
  n = 6
  ref = C_element
FEATURE [App::DocumentObjectGroupPython] H_element106  label="H_element : 15"  # scripted group (container) (typed FeaturePython)
  n = 15
  ref = H_element
FEATURE [App::DocumentObjectGroupPython] O_element099  label="O_element : 053"  # scripted group (container) (typed FeaturePython)
  n = 4
  ref = O_element
FEATURE [App::DocumentObjectGroupPython] P_element012  label="P_element : 1"  # scripted group (container) (typed FeaturePython)
  n = 1
  ref = P_element
FEATURE [App::DocumentObjectGroupPython] G4_TRIETHYL_PHOSPHATE  # scripted group (container) (typed FeaturePython)
  Dunit = g/cm3
  Dvalue = 1.07
  Group = -> [C_element116,H_element106,O_element099,P_element012]
  conduct = 2
  density = 1
  expand = 3
  formula = G4_TRIETHYL_PHOSPHATE
  name = G4_TRIETHYL_PHOSPHATE
  specific = 4
FEATURE [App::DocumentObjectGroupPython] W_element003  label="W_element : 003"  # scripted group (container) (typed FeaturePython)
  n = 1
  ref = W_element
FEATURE [App::DocumentObjectGroupPython] F_element017  label="F_element : 6"  # scripted group (container) (typed FeaturePython)
  n = 6
  ref = F_element
FEATURE [App::DocumentObjectGroupPython] G4_TUNGSTEN_HEXAFLUORIDE  # scripted group (container) (typed FeaturePython)
  Dunit = g/cm3
  Dvalue = 2.4
  Group = -> [W_element003,F_element017]
  conduct = 2
  density = 1
  expand = 3
  formula = G4_TUNGSTEN_HEXAFLUORIDE
  name = G4_TUNGSTEN_HEXAFLUORIDE
  specific = 4
FEATURE [App::DocumentObjectGroupPython] U_element001  label="U_element : 1"  # scripted group (container) (typed FeaturePython)
  n = 1
  ref = U_element
FEATURE [App::DocumentObjectGroupPython] C_element117  label="C_element : 064"  # scripted group (container) (typed FeaturePython)
  n = 2
  ref = C_element
FEATURE [App::DocumentObjectGroupPython] G4_URANIUM_DICARBIDE  # scripted group (container) (typed FeaturePython)
  Dunit = g/cm3
  Dvalue = 11.28
  Group = -> [U_element001,C_element117]
  conduct = 2
  density = 1
  expand = 3
  formula = G4_URANIUM_DICARBIDE
  name = G4_URANIUM_DICARBIDE
  specific = 4
FEATURE [App::DocumentObjectGroupPython] U_element002  label="U_element : 002"  # scripted group (container) (typed FeaturePython)
  n = 1
  ref = U_element
FEATURE [App::DocumentObjectGroupPython] C_element118  label="C_element : 065"  # scripted group (container) (typed FeaturePython)
  n = 1
  ref = C_element
FEATURE [App::DocumentObjectGroupPython] G4_URANIUM_MONOCARBIDE  # scripted group (container) (typed FeaturePython)
  Dunit = g/cm3
  Dvalue = 13.63
  Group = -> [U_element002,C_element118]
  conduct = 2
  density = 1
  expand = 3
  formula = G4_URANIUM_MONOCARBIDE
  name = G4_URANIUM_MONOCARBIDE
  specific = 4
FEATURE [App::DocumentObjectGroupPython] U_element003  label="U_element : 003"  # scripted group (container) (typed FeaturePython)
  n = 1
  ref = U_element
FEATURE [App::DocumentObjectGroupPython] O_element100  label="O_element : 054"  # scripted group (container) (typed FeaturePython)
  n = 2
  ref = O_element
FEATURE [App::DocumentObjectGroupPython] G4_URANIUM_OXIDE  # scripted group (container) (typed FeaturePython)
  Dunit = g/cm3
  Dvalue = 10.96
  Group = -> [U_element003,O_element100]
  conduct = 2
  density = 1
  expand = 3
  formula = G4_URANIUM_OXIDE
  name = G4_URANIUM_OXIDE
  specific = 4
FEATURE [App::DocumentObjectGroupPython] C_element119  label="C_element : 066"  # scripted group (container) (typed FeaturePython)
  n = 1
  ref = C_element
FEATURE [App::DocumentObjectGroupPython] H_element107  label="H_element : 057"  # scripted group (container) (typed FeaturePython)
  n = 4
  ref = H_element
FEATURE [App::DocumentObjectGroupPython] N_element046  label="N_element : 019"  # scripted group (container) (typed FeaturePython)
  n = 2
  ref = N_element
FEATURE [App::DocumentObjectGroupPython] O_element101  label="O_element : 055"  # scripted group (container) (typed FeaturePython)
  n = 1
  ref = O_element
FEATURE [App::DocumentObjectGroupPython] G4_UREA  # scripted group (container) (typed FeaturePython)
  Dunit = g/cm3
  Dvalue = 1.323
  Group = -> [C_element119,H_element107,N_element046,O_element101]
  conduct = 2
  density = 1
  expand = 3
  formula = G4_UREA
  name = G4_UREA
  specific = 4
FEATURE [App::DocumentObjectGroupPython] C_element120  label="C_element : 067"  # scripted group (container) (typed FeaturePython)
  n = 5
  ref = C_element
FEATURE [App::DocumentObjectGroupPython] H_element108  label="H_element : 058"  # scripted group (container) (typed FeaturePython)
  n = 11
  ref = H_element
FEATURE [App::DocumentObjectGroupPython] N_element047  label="N_element : 020"  # scripted group (container) (typed FeaturePython)
  n = 1
  ref = N_element
FEATURE [App::DocumentObjectGroupPython] O_element102  label="O_element : 056"  # scripted group (container) (typed FeaturePython)
  n = 2
  ref = O_element
FEATURE [App::DocumentObjectGroupPython] G4_VALINE  # scripted group (container) (typed FeaturePython)
  Dunit = g/cm3
  Dvalue = 1.23
  Group = -> [C_element120,H_element108,N_element047,O_element102]
  conduct = 2
  density = 1
  expand = 3
  formula = G4_VALINE
  name = G4_VALINE
  specific = 4
FEATURE [App::DocumentObjectGroupPython] H_element109  label="H_element : 0.009"  # scripted group (container) (typed FeaturePython)
  n = 0.009417
FEATURE [App::DocumentObjectGroupPython] C_element121  label="C_element : 0.281"  # scripted group (container) (typed FeaturePython)
  n = 0.280555
FEATURE [App::DocumentObjectGroupPython] F_element018  label="F_element : 0.710"  # scripted group (container) (typed FeaturePython)
  n = 0.710028
FEATURE [App::DocumentObjectGroupPython] G4_VITON  # scripted group (container) (typed FeaturePython)
  Dunit = g/cm3
  Dvalue = 1.8
  Group = -> [H_element109,C_element121,F_element018]
  conduct = 2
  density = 1
  expand = 3
  formula = G4_VITON
  name = G4_VITON
  specific = 4
FEATURE [App::DocumentObjectGroupPython] H_element110  label="H_element : 059"  # scripted group (container) (typed FeaturePython)
  n = 2
  ref = H_element
FEATURE [App::DocumentObjectGroupPython] O_element103  label="O_element : 057"  # scripted group (container) (typed FeaturePython)
  n = 1
  ref = O_element
FEATURE [App::DocumentObjectGroupPython] G4_WATER  # scripted group (container) (typed FeaturePython)
  Dunit = g/cm3
  Dvalue = 1
  Group = -> [H_element110,O_element103]
  conduct = 2
  density = 1
  expand = 3
  formula = G4_WATER
  name = G4_WATER
  specific = 4
FEATURE [App::DocumentObjectGroupPython] H_element111  label="H_element : 060"  # scripted group (container) (typed FeaturePython)
  n = 2
  ref = H_element
FEATURE [App::DocumentObjectGroupPython] O_element104  label="O_element : 058"  # scripted group (container) (typed FeaturePython)
  n = 1
  ref = O_element
FEATURE [App::DocumentObjectGroupPython] G4_WATER_VAPOR  # scripted group (container) (typed FeaturePython)
  Dunit = g/cm3
  Dvalue = 0.000756182
  Group = -> [H_element111,O_element104]
  conduct = 2
  density = 1
  expand = 3
  formula = G4_WATER_VAPOR
  name = G4_WATER_VAPOR
  specific = 4
FEATURE [App::DocumentObjectGroupPython] C_element122  label="C_element : 068"  # scripted group (container) (typed FeaturePython)
  n = 8
  ref = C_element
FEATURE [App::DocumentObjectGroupPython] H_element112  label="H_element : 061"  # scripted group (container) (typed FeaturePython)
  n = 10
  ref = H_element
FEATURE [App::DocumentObjectGroupPython] G4_XYLENE  # scripted group (container) (typed FeaturePython)
  Dunit = g/cm3
  Dvalue = 0.87
  Group = -> [C_element122,H_element112]
  conduct = 2
  density = 1
  expand = 3
  formula = G4_XYLENE
  name = G4_XYLENE
  specific = 4
FEATURE [App::DocumentObjectGroupPython] C_element123  label="C_element : 069"  # scripted group (container) (typed FeaturePython)
  n = 1
  ref = C_element
FEATURE [App::DocumentObjectGroupPython] G4_GRAPHITE  # scripted group (container) (typed FeaturePython)
  Dunit = g/cm3
  Dvalue = 2.21
  Group = -> [C_element123]
  conduct = 2
  density = 1
  expand = 3
  formula = G4_GRAPHITE
  name = G4_GRAPHITE
  specific = 4
FEATURE [App::DocumentObjectGroupPython] NIST  # scripted group (container) (typed FeaturePython)
  Group = -> [G4_A_150_TISSUE,G4_ACETONE,G4_ACETYLENE,G4_ADENINE,G4_ADIPOSE_TISSUE_ICRP,G4_AIR,G4_ALANINE,G4_ALUMINUM_OXIDE,G4_AMBER,G4_AMMONIA,G4_ANILINE,G4_ANTHRACENE,G4_B_100_BONE,G4_BAKELITE,G4_BARIUM_FLUORIDE,G4_BARIUM_SULFATE,G4_BENZENE,G4_BERYLLIUM_OXIDE,G4_BGO,G4_BLOOD_ICRP,G4_BONE_COMPACT_ICRU,G4_BONE_CORTICAL_ICRP,G4_BORON_CARBIDE,G4_BORON_OXIDE,G4_BRAIN_ICRP,G4_BUTANE,G4_N_BUTYL_ALCOHOL,G4_C_552,+152 more]
FEATURE [App::DocumentObjectGroupPython] H_element113  label="H_element : 062"  # scripted group (container) (typed FeaturePython)
  n = 1
  ref = H_element
FEATURE [App::DocumentObjectGroupPython] G4_H  # scripted group (container) (typed FeaturePython)
  Dunit = g/cm3
  Dvalue = 8.3748e-05
  Group = -> [H_element113]
  conduct = 2
  density = 1
  expand = 3
  formula = H
  name = G4_H
  specific = 4
FEATURE [App::DocumentObjectGroupPython] He_element001  label="He_element : 1"  # scripted group (container) (typed FeaturePython)
  n = 1
  ref = He_element
FEATURE [App::DocumentObjectGroupPython] G4_He  # scripted group (container) (typed FeaturePython)
  Dunit = g/cm3
  Dvalue = 0.000166322
  Group = -> [He_element001]
  conduct = 2
  density = 1
  expand = 3
  formula = He
  name = G4_He
  specific = 4
FEATURE [App::DocumentObjectGroupPython] Li_element008  label="Li_element : 008"  # scripted group (container) (typed FeaturePython)
  n = 1
  ref = Li_element
FEATURE [App::DocumentObjectGroupPython] G4_Li  # scripted group (container) (typed FeaturePython)
  Dunit = g/cm3
  Dvalue = 0.534
  Group = -> [Li_element008]
  conduct = 2
  density = 1
  expand = 3
  formula = Li
  name = G4_Li
  specific = 4
FEATURE [App::DocumentObjectGroupPython] Be_element002  label="Be_element : 002"  # scripted group (container) (typed FeaturePython)
  n = 1
  ref = Be_element
FEATURE [App::DocumentObjectGroupPython] G4_Be  # scripted group (container) (typed FeaturePython)
  Dunit = g/cm3
  Dvalue = 1.848
  Group = -> [Be_element002]
  conduct = 2
  density = 1
  expand = 3
  formula = Be
  name = G4_Be
  specific = 4
FEATURE [App::DocumentObjectGroupPython] B_element007  label="B_element : 007"  # scripted group (container) (typed FeaturePython)
  n = 1
  ref = B_element
FEATURE [App::DocumentObjectGroupPython] G4_B  # scripted group (container) (typed FeaturePython)
  Dunit = g/cm3
  Dvalue = 2.37
  Group = -> [B_element007]
  conduct = 2
  density = 1
  expand = 3
  formula = B
  name = G4_B
  specific = 4
FEATURE [App::DocumentObjectGroupPython] C_element124  label="C_element : 070"  # scripted group (container) (typed FeaturePython)
  n = 1
  ref = C_element
FEATURE [App::DocumentObjectGroupPython] G4_C  # scripted group (container) (typed FeaturePython)
  Dunit = g/cm3
  Dvalue = 2
  Group = -> [C_element124]
  conduct = 2
  density = 1
  expand = 3
  formula = C
  name = G4_C
  specific = 4
FEATURE [App::DocumentObjectGroupPython] N_element048  label="N_element : 021"  # scripted group (container) (typed FeaturePython)
  n = 1
  ref = N_element
FEATURE [App::DocumentObjectGroupPython] G4_N  # scripted group (container) (typed FeaturePython)
  Dunit = g/cm3
  Dvalue = 0.0011652
  Group = -> [N_element048]
  conduct = 2
  density = 1
  expand = 3
  formula = N
  name = G4_N
  specific = 4
FEATURE [App::DocumentObjectGroupPython] O_element105  label="O_element : 059"  # scripted group (container) (typed FeaturePython)
  n = 1
  ref = O_element
FEATURE [App::DocumentObjectGroupPython] G4_O  # scripted group (container) (typed FeaturePython)
  Dunit = g/cm3
  Dvalue = 0.00133151
  Group = -> [O_element105]
  conduct = 2
  density = 1
  expand = 3
  formula = O
  name = G4_O
  specific = 4
FEATURE [App::DocumentObjectGroupPython] F_element019  label="F_element : 008"  # scripted group (container) (typed FeaturePython)
  n = 1
  ref = F_element
FEATURE [App::DocumentObjectGroupPython] G4_F  # scripted group (container) (typed FeaturePython)
  Dunit = g/cm3
  Dvalue = 0.00158029
  Group = -> [F_element019]
  conduct = 2
  density = 1
  expand = 3
  formula = F
  name = G4_F
  specific = 4
FEATURE [App::DocumentObjectGroupPython] Ne_element001  label="Ne_element : 1"  # scripted group (container) (typed FeaturePython)
  n = 1
  ref = Ne_element
FEATURE [App::DocumentObjectGroupPython] G4_Ne  # scripted group (container) (typed FeaturePython)
  Dunit = g/cm3
  Dvalue = 0.000838505
  Group = -> [Ne_element001]
  conduct = 2
  density = 1
  expand = 3
  formula = Ne
  name = G4_Ne
  specific = 4
FEATURE [App::DocumentObjectGroupPython] Na_element020  label="Na_element : 005"  # scripted group (container) (typed FeaturePython)
  n = 1
  ref = Na_element
FEATURE [App::DocumentObjectGroupPython] G4_Na  # scripted group (container) (typed FeaturePython)
  Dunit = g/cm3
  Dvalue = 0.971
  Group = -> [Na_element020]
  conduct = 2
  density = 1
  expand = 3
  formula = Na
  name = G4_Na
  specific = 4
FEATURE [App::DocumentObjectGroupPython] Mg_element011  label="Mg_element : 005"  # scripted group (container) (typed FeaturePython)
  n = 1
  ref = Mg_element
FEATURE [App::DocumentObjectGroupPython] G4_Mg  # scripted group (container) (typed FeaturePython)
  Dunit = g/cm3
  Dvalue = 1.74
  Group = -> [Mg_element011]
  conduct = 2
  density = 1
  expand = 3
  formula = Mg
  name = G4_Mg
  specific = 4
FEATURE [App::DocumentObjectGroupPython] Al_element004  label="Al_element : 1"  # scripted group (container) (typed FeaturePython)
  n = 1
  ref = Al_element
FEATURE [App::DocumentObjectGroupPython] G4_Al  # scripted group (container) (typed FeaturePython)
  Dunit = g/cm3
  Dvalue = 2.699
  Group = -> [Al_element004]
  conduct = 2
  density = 1
  expand = 3
  formula = Al
  name = G4_Al
  specific = 4
FEATURE [App::DocumentObjectGroupPython] Si_element007  label="Si_element : 002"  # scripted group (container) (typed FeaturePython)
  n = 1
  ref = Si_element
FEATURE [App::DocumentObjectGroupPython] G4_Si  # scripted group (container) (typed FeaturePython)
  Dunit = g/cm3
  Dvalue = 2.33
  Group = -> [Si_element007]
  conduct = 2
  density = 1
  expand = 3
  formula = Si
  name = G4_Si
  specific = 4
FEATURE [App::DocumentObjectGroupPython] P_element013  label="P_element : 002"  # scripted group (container) (typed FeaturePython)
  n = 1
  ref = P_element
FEATURE [App::DocumentObjectGroupPython] G4_P  # scripted group (container) (typed FeaturePython)
  Dunit = g/cm3
  Dvalue = 2.2
  Group = -> [P_element013]
  conduct = 2
  density = 1
  expand = 3
  formula = P
  name = G4_P
  specific = 4
FEATURE [App::DocumentObjectGroupPython] S_element023  label="S_element : 007"  # scripted group (container) (typed FeaturePython)
  n = 1
  ref = S_element
FEATURE [App::DocumentObjectGroupPython] G4_S  # scripted group (container) (typed FeaturePython)
  Dunit = g/cm3
  Dvalue = 2
  Group = -> [S_element023]
  conduct = 2
  density = 1
  expand = 3
  formula = S
  name = G4_S
  specific = 4
FEATURE [App::DocumentObjectGroupPython] Cl_element029  label="Cl_element : 015"  # scripted group (container) (typed FeaturePython)
  n = 1
  ref = Cl_element
FEATURE [App::DocumentObjectGroupPython] G4_Cl  # scripted group (container) (typed FeaturePython)
  Dunit = g/cm3
  Dvalue = 0.00299473
  Group = -> [Cl_element029]
  conduct = 2
  density = 1
  expand = 3
  formula = Cl
  name = G4_Cl
  specific = 4
FEATURE [App::DocumentObjectGroupPython] Ar_element002  label="Ar_element : 1"  # scripted group (container) (typed FeaturePython)
  n = 1
  ref = Ar_element
FEATURE [App::DocumentObjectGroupPython] G4_Ar  # scripted group (container) (typed FeaturePython)
  Dunit = g/cm3
  Dvalue = 0.00166201
  Group = -> [Ar_element002]
  conduct = 2
  density = 1
  expand = 3
  formula = Ar
  name = G4_Ar
  specific = 4
FEATURE [App::DocumentObjectGroupPython] K_element013  label="K_element : 003"  # scripted group (container) (typed FeaturePython)
  n = 1
  ref = K_element
FEATURE [App::DocumentObjectGroupPython] G4_K  # scripted group (container) (typed FeaturePython)
  Dunit = g/cm3
  Dvalue = 0.862
  Group = -> [K_element013]
  conduct = 2
  density = 1
  expand = 3
  formula = K
  name = G4_K
  specific = 4
FEATURE [App::DocumentObjectGroupPython] Ca_element014  label="Ca_element : 007"  # scripted group (container) (typed FeaturePython)
  n = 1
  ref = Ca_element
FEATURE [App::DocumentObjectGroupPython] G4_Ca  # scripted group (container) (typed FeaturePython)
  Dunit = g/cm3
  Dvalue = 1.55
  Group = -> [Ca_element014]
  conduct = 2
  density = 1
  expand = 3
  formula = Ca
  name = G4_Ca
  specific = 4
FEATURE [App::DocumentObjectGroupPython] Sc_element001  label="Sc_element : 1"  # scripted group (container) (typed FeaturePython)
  n = 1
  ref = Sc_element
FEATURE [App::DocumentObjectGroupPython] G4_Sc  # scripted group (container) (typed FeaturePython)
  Dunit = g/cm3
  Dvalue = 2.989
  Group = -> [Sc_element001]
  conduct = 2
  density = 1
  expand = 3
  formula = Sc
  name = G4_Sc
  specific = 4
FEATURE [App::DocumentObjectGroupPython] Ti_element004  label="Ti_element : 002"  # scripted group (container) (typed FeaturePython)
  n = 1
  ref = Ti_element
FEATURE [App::DocumentObjectGroupPython] G4_Ti  # scripted group (container) (typed FeaturePython)
  Dunit = g/cm3
  Dvalue = 4.54
  Group = -> [Ti_element004]
  conduct = 2
  density = 1
  expand = 3
  formula = Ti
  name = G4_Ti
  specific = 4
FEATURE [App::DocumentObjectGroupPython] V_element001  label="V_element : 1"  # scripted group (container) (typed FeaturePython)
  n = 1
  ref = V_element
FEATURE [App::DocumentObjectGroupPython] G4_V  # scripted group (container) (typed FeaturePython)
  Dunit = g/cm3
  Dvalue = 6.11
  Group = -> [V_element001]
  conduct = 2
  density = 1
  expand = 3
  formula = V
  name = G4_V
  specific = 4
FEATURE [App::DocumentObjectGroupPython] Cr_element001  label="Cr_element : 1"  # scripted group (container) (typed FeaturePython)
  n = 1
  ref = Cr_element
FEATURE [App::DocumentObjectGroupPython] G4_Cr  # scripted group (container) (typed FeaturePython)
  Dunit = g/cm3
  Dvalue = 7.18
  Group = -> [Cr_element001]
  conduct = 2
  density = 1
  expand = 3
  formula = Cr
  name = G4_Cr
  specific = 4
FEATURE [App::DocumentObjectGroupPython] Mn_element001  label="Mn_element : 1"  # scripted group (container) (typed FeaturePython)
  n = 1
  ref = Mn_element
FEATURE [App::DocumentObjectGroupPython] G4_Mn  # scripted group (container) (typed FeaturePython)
  Dunit = g/cm3
  Dvalue = 7.44
  Group = -> [Mn_element001]
  conduct = 2
  density = 1
  expand = 3
  formula = Mn
  name = G4_Mn
  specific = 4
FEATURE [App::DocumentObjectGroupPython] Fe_element007  label="Fe_element : 004"  # scripted group (container) (typed FeaturePython)
  n = 1
  ref = Fe_element
FEATURE [App::DocumentObjectGroupPython] G4_Fe  # scripted group (container) (typed FeaturePython)
  Dunit = g/cm3
  Dvalue = 7.874
  Group = -> [Fe_element007]
  conduct = 2
  density = 1
  expand = 3
  formula = Fe
  name = G4_Fe
  specific = 4
FEATURE [App::DocumentObjectGroupPython] Co_element001  label="Co_element : 1"  # scripted group (container) (typed FeaturePython)
  n = 1
  ref = Co_element
FEATURE [App::DocumentObjectGroupPython] G4_Co  # scripted group (container) (typed FeaturePython)
  Dunit = g/cm3
  Dvalue = 8.9
  Group = -> [Co_element001]
  conduct = 2
  density = 1
  expand = 3
  formula = Co
  name = G4_Co
  specific = 4
FEATURE [App::DocumentObjectGroupPython] Ni_element001  label="Ni_element : 1"  # scripted group (container) (typed FeaturePython)
  n = 1
  ref = Ni_element
FEATURE [App::DocumentObjectGroupPython] G4_Ni  # scripted group (container) (typed FeaturePython)
  Dunit = g/cm3
  Dvalue = 8.902
  Group = -> [Ni_element001]
  conduct = 2
  density = 1
  expand = 3
  formula = Ni
  name = G4_Ni
  specific = 4
FEATURE [App::DocumentObjectGroupPython] Cu_element001  label="Cu_element : 1"  # scripted group (container) (typed FeaturePython)
  n = 1
  ref = Cu_element
FEATURE [App::DocumentObjectGroupPython] G4_Cu  # scripted group (container) (typed FeaturePython)
  Dunit = g/cm3
  Dvalue = 8.96
  Group = -> [Cu_element001]
  conduct = 2
  density = 1
  expand = 3
  formula = Cu
  name = G4_Cu
  specific = 4
FEATURE [App::DocumentObjectGroupPython] Zn_element001  label="Zn_element : 1"  # scripted group (container) (typed FeaturePython)
  n = 1
  ref = Zn_element
FEATURE [App::DocumentObjectGroupPython] G4_Zn  # scripted group (container) (typed FeaturePython)
  Dunit = g/cm3
  Dvalue = 7.133
  Group = -> [Zn_element001]
  conduct = 2
  density = 1
  expand = 3
  formula = Zn
  name = G4_Zn
  specific = 4
FEATURE [App::DocumentObjectGroupPython] Ga_element002  label="Ga_element : 002"  # scripted group (container) (typed FeaturePython)
  n = 1
  ref = Ga_element
FEATURE [App::DocumentObjectGroupPython] G4_Ga  # scripted group (container) (typed FeaturePython)
  Dunit = g/cm3
  Dvalue = 5.904
  Group = -> [Ga_element002]
  conduct = 2
  density = 1
  expand = 3
  formula = Ga
  name = G4_Ga
  specific = 4
FEATURE [App::DocumentObjectGroupPython] Ge_element002  label="Ge_element : 1"  # scripted group (container) (typed FeaturePython)
  n = 1
  ref = Ge_element
FEATURE [App::DocumentObjectGroupPython] G4_Ge  # scripted group (container) (typed FeaturePython)
  Dunit = g/cm3
  Dvalue = 5.323
  Group = -> [Ge_element002]
  conduct = 2
  density = 1
  expand = 3
  formula = Ge
  name = G4_Ge
  specific = 4
FEATURE [App::DocumentObjectGroupPython] As_element003  label="As_element : 002"  # scripted group (container) (typed FeaturePython)
  n = 1
  ref = As_element
FEATURE [App::DocumentObjectGroupPython] G4_As  # scripted group (container) (typed FeaturePython)
  Dunit = g/cm3
  Dvalue = 5.73
  Group = -> [As_element003]
  conduct = 2
  density = 1
  expand = 3
  formula = As
  name = G4_As
  specific = 4
FEATURE [App::DocumentObjectGroupPython] Se_element001  label="Se_element : 1"  # scripted group (container) (typed FeaturePython)
  n = 1
  ref = Se_element
FEATURE [App::DocumentObjectGroupPython] G4_Se  # scripted group (container) (typed FeaturePython)
  Dunit = g/cm3
  Dvalue = 4.5
  Group = -> [Se_element001]
  conduct = 2
  density = 1
  expand = 3
  formula = Se
  name = G4_Se
  specific = 4
FEATURE [App::DocumentObjectGroupPython] Br_element007  label="Br_element : 004"  # scripted group (container) (typed FeaturePython)
  n = 1
  ref = Br_element
FEATURE [App::DocumentObjectGroupPython] G4_Br  # scripted group (container) (typed FeaturePython)
  Dunit = g/cm3
  Dvalue = 0.0070721
  Group = -> [Br_element007]
  conduct = 2
  density = 1
  expand = 3
  formula = Br
  name = G4_Br
  specific = 4
FEATURE [App::DocumentObjectGroupPython] Kr_element001  label="Kr_element : 1"  # scripted group (container) (typed FeaturePython)
  n = 1
  ref = Kr_element
FEATURE [App::DocumentObjectGroupPython] G4_Kr  # scripted group (container) (typed FeaturePython)
  Dunit = g/cm3
  Dvalue = 0.00347832
  Group = -> [Kr_element001]
  conduct = 2
  density = 1
  expand = 3
  formula = Kr
  name = G4_Kr
  specific = 4
FEATURE [App::DocumentObjectGroupPython] Rb_element001  label="Rb_element : 1"  # scripted group (container) (typed FeaturePython)
  n = 1
  ref = Rb_element
FEATURE [App::DocumentObjectGroupPython] G4_Rb  # scripted group (container) (typed FeaturePython)
  Dunit = g/cm3
  Dvalue = 1.532
  Group = -> [Rb_element001]
  conduct = 2
  density = 1
  expand = 3
  formula = Rb
  name = G4_Rb
  specific = 4
FEATURE [App::DocumentObjectGroupPython] Sr_element001  label="Sr_element : 1"  # scripted group (container) (typed FeaturePython)
  n = 1
  ref = Sr_element
FEATURE [App::DocumentObjectGroupPython] G4_Sr  # scripted group (container) (typed FeaturePython)
  Dunit = g/cm3
  Dvalue = 2.54
  Group = -> [Sr_element001]
  conduct = 2
  density = 1
  expand = 3
  formula = Sr
  name = G4_Sr
  specific = 4
FEATURE [App::DocumentObjectGroupPython] Y_element001  label="Y_element : 1"  # scripted group (container) (typed FeaturePython)
  n = 1
  ref = Y_element
FEATURE [App::DocumentObjectGroupPython] G4_Y  # scripted group (container) (typed FeaturePython)
  Dunit = g/cm3
  Dvalue = 4.469
  Group = -> [Y_element001]
  conduct = 2
  density = 1
  expand = 3
  formula = Y
  name = G4_Y
  specific = 4
FEATURE [App::DocumentObjectGroupPython] Zr_element001  label="Zr_element : 1"  # scripted group (container) (typed FeaturePython)
  n = 1
  ref = Zr_element
FEATURE [App::DocumentObjectGroupPython] G4_Zr  # scripted group (container) (typed FeaturePython)
  Dunit = g/cm3
  Dvalue = 6.506
  Group = -> [Zr_element001]
  conduct = 2
  density = 1
  expand = 3
  formula = Zr
  name = G4_Zr
  specific = 4
FEATURE [App::DocumentObjectGroupPython] Nb_element001  label="Nb_element : 1"  # scripted group (container) (typed FeaturePython)
  n = 1
  ref = Nb_element
FEATURE [App::DocumentObjectGroupPython] G4_Nb  # scripted group (container) (typed FeaturePython)
  Dunit = g/cm3
  Dvalue = 8.57
  Group = -> [Nb_element001]
  conduct = 2
  density = 1
  expand = 3
  formula = Nb
  name = G4_Nb
  specific = 4
FEATURE [App::DocumentObjectGroupPython] Mo_element001  label="Mo_element : 1"  # scripted group (container) (typed FeaturePython)
  n = 1
  ref = Mo_element
FEATURE [App::DocumentObjectGroupPython] G4_Mo  # scripted group (container) (typed FeaturePython)
  Dunit = g/cm3
  Dvalue = 10.22
  Group = -> [Mo_element001]
  conduct = 2
  density = 1
  expand = 3
  formula = Mo
  name = G4_Mo
  specific = 4
FEATURE [App::DocumentObjectGroupPython] Tc_element001  label="Tc_element : 1"  # scripted group (container) (typed FeaturePython)
  n = 1
  ref = Tc_element
FEATURE [App::DocumentObjectGroupPython] G4_Tc  # scripted group (container) (typed FeaturePython)
  Dunit = g/cm3
  Dvalue = 11.5
  Group = -> [Tc_element001]
  conduct = 2
  density = 1
  expand = 3
  formula = Tc
  name = G4_Tc
  specific = 4
FEATURE [App::DocumentObjectGroupPython] Ru_element001  label="Ru_element : 1"  # scripted group (container) (typed FeaturePython)
  n = 1
  ref = Ru_element
FEATURE [App::DocumentObjectGroupPython] G4_Ru  # scripted group (container) (typed FeaturePython)
  Dunit = g/cm3
  Dvalue = 12.41
  Group = -> [Ru_element001]
  conduct = 2
  density = 1
  expand = 3
  formula = Ru
  name = G4_Ru
  specific = 4
FEATURE [App::DocumentObjectGroupPython] Rh_element001  label="Rh_element : 1"  # scripted group (container) (typed FeaturePython)
  n = 1
  ref = Rh_element
FEATURE [App::DocumentObjectGroupPython] G4_Rh  # scripted group (container) (typed FeaturePython)
  Dunit = g/cm3
  Dvalue = 12.41
  Group = -> [Rh_element001]
  conduct = 2
  density = 1
  expand = 3
  formula = Rh
  name = G4_Rh
  specific = 4
FEATURE [App::DocumentObjectGroupPython] Pd_element001  label="Pd_element : 1"  # scripted group (container) (typed FeaturePython)
  n = 1
  ref = Pd_element
FEATURE [App::DocumentObjectGroupPython] G4_Pd  # scripted group (container) (typed FeaturePython)
  Dunit = g/cm3
  Dvalue = 12.02
  Group = -> [Pd_element001]
  conduct = 2
  density = 1
  expand = 3
  formula = Pd
  name = G4_Pd
  specific = 4
FEATURE [App::DocumentObjectGroupPython] Ag_element006  label="Ag_element : 004"  # scripted group (container) (typed FeaturePython)
  n = 1
  ref = Ag_element
FEATURE [App::DocumentObjectGroupPython] G4_Ag  # scripted group (container) (typed FeaturePython)
  Dunit = g/cm3
  Dvalue = 10.5
  Group = -> [Ag_element006]
  conduct = 2
  density = 1
  expand = 3
  formula = Ag
  name = G4_Ag
  specific = 4
FEATURE [App::DocumentObjectGroupPython] Cd_element003  label="Cd_element : 003"  # scripted group (container) (typed FeaturePython)
  n = 1
  ref = Cd_element
FEATURE [App::DocumentObjectGroupPython] G4_Cd  # scripted group (container) (typed FeaturePython)
  Dunit = g/cm3
  Dvalue = 8.65
  Group = -> [Cd_element003]
  conduct = 2
  density = 1
  expand = 3
  formula = Cd
  name = G4_Cd
  specific = 4
FEATURE [App::DocumentObjectGroupPython] In_element001  label="In_element : 1"  # scripted group (container) (typed FeaturePython)
  n = 1
  ref = In_element
FEATURE [App::DocumentObjectGroupPython] G4_In  # scripted group (container) (typed FeaturePython)
  Dunit = g/cm3
  Dvalue = 7.31
  Group = -> [In_element001]
  conduct = 2
  density = 1
  expand = 3
  formula = In
  name = G4_In
  specific = 4
FEATURE [App::DocumentObjectGroupPython] Sn_element001  label="Sn_element : 1"  # scripted group (container) (typed FeaturePython)
  n = 1
  ref = Sn_element
FEATURE [App::DocumentObjectGroupPython] G4_Sn  # scripted group (container) (typed FeaturePython)
  Dunit = g/cm3
  Dvalue = 7.31
  Group = -> [Sn_element001]
  conduct = 2
  density = 1
  expand = 3
  formula = Sn
  name = G4_Sn
  specific = 4
FEATURE [App::DocumentObjectGroupPython] Sb_element001  label="Sb_element : 1"  # scripted group (container) (typed FeaturePython)
  n = 1
  ref = Sb_element
FEATURE [App::DocumentObjectGroupPython] G4_Sb  # scripted group (container) (typed FeaturePython)
  Dunit = g/cm3
  Dvalue = 6.691
  Group = -> [Sb_element001]
  conduct = 2
  density = 1
  expand = 3
  formula = Sb
  name = G4_Sb
  specific = 4
FEATURE [App::DocumentObjectGroupPython] Te_element002  label="Te_element : 002"  # scripted group (container) (typed FeaturePython)
  n = 1
  ref = Te_element
FEATURE [App::DocumentObjectGroupPython] G4_Te  # scripted group (container) (typed FeaturePython)
  Dunit = g/cm3
  Dvalue = 6.24
  Group = -> [Te_element002]
  conduct = 2
  density = 1
  expand = 3
  formula = Te
  name = G4_Te
  specific = 4
FEATURE [App::DocumentObjectGroupPython] I_element010  label="I_element : 006"  # scripted group (container) (typed FeaturePython)
  n = 1
  ref = I_element
FEATURE [App::DocumentObjectGroupPython] G4_I  # scripted group (container) (typed FeaturePython)
  Dunit = g/cm3
  Dvalue = 4.93
  Group = -> [I_element010]
  conduct = 2
  density = 1
  expand = 3
  formula = I
  name = G4_I
  specific = 4
FEATURE [App::DocumentObjectGroupPython] Xe_element001  label="Xe_element : 1"  # scripted group (container) (typed FeaturePython)
  n = 1
  ref = Xe_element
FEATURE [App::DocumentObjectGroupPython] G4_Xe  # scripted group (container) (typed FeaturePython)
  Dunit = g/cm3
  Dvalue = 0.00548536
  Group = -> [Xe_element001]
  conduct = 2
  density = 1
  expand = 3
  formula = Xe
  name = G4_Xe
  specific = 4
FEATURE [App::DocumentObjectGroupPython] Cs_element003  label="Cs_element : 003"  # scripted group (container) (typed FeaturePython)
  n = 1
  ref = Cs_element
FEATURE [App::DocumentObjectGroupPython] G4_Cs  # scripted group (container) (typed FeaturePython)
  Dunit = g/cm3
  Dvalue = 1.873
  Group = -> [Cs_element003]
  conduct = 2
  density = 1
  expand = 3
  formula = Cs
  name = G4_Cs
  specific = 4
FEATURE [App::DocumentObjectGroupPython] Ba_element003  label="Ba_element : 003"  # scripted group (container) (typed FeaturePython)
  n = 1
  ref = Ba_element
FEATURE [App::DocumentObjectGroupPython] G4_Ba  # scripted group (container) (typed FeaturePython)
  Dunit = g/cm3
  Dvalue = 3.5
  Group = -> [Ba_element003]
  conduct = 2
  density = 1
  expand = 3
  formula = Ba
  name = G4_Ba
  specific = 4
FEATURE [App::DocumentObjectGroupPython] La_element003  label="La_element : 003"  # scripted group (container) (typed FeaturePython)
  n = 1
  ref = La_element
FEATURE [App::DocumentObjectGroupPython] G4_La  # scripted group (container) (typed FeaturePython)
  Dunit = g/cm3
  Dvalue = 6.154
  Group = -> [La_element003]
  conduct = 2
  density = 1
  expand = 3
  formula = La
  name = G4_La
  specific = 4
FEATURE [App::DocumentObjectGroupPython] Ce_element002  label="Ce_element : 1"  # scripted group (container) (typed FeaturePython)
  n = 1
  ref = Ce_element
FEATURE [App::DocumentObjectGroupPython] G4_Ce  # scripted group (container) (typed FeaturePython)
  Dunit = g/cm3
  Dvalue = 6.657
  Group = -> [Ce_element002]
  conduct = 2
  density = 1
  expand = 3
  formula = Ce
  name = G4_Ce
  specific = 4
FEATURE [App::DocumentObjectGroupPython] Pr_element001  label="Pr_element : 1"  # scripted group (container) (typed FeaturePython)
  n = 1
  ref = Pr_element
FEATURE [App::DocumentObjectGroupPython] G4_Pr  # scripted group (container) (typed FeaturePython)
  Dunit = g/cm3
  Dvalue = 6.71
  Group = -> [Pr_element001]
  conduct = 2
  density = 1
  expand = 3
  formula = Pr
  name = G4_Pr
  specific = 4
FEATURE [App::DocumentObjectGroupPython] Nd_element001  label="Nd_element : 1"  # scripted group (container) (typed FeaturePython)
  n = 1
  ref = Nd_element
FEATURE [App::DocumentObjectGroupPython] G4_Nd  # scripted group (container) (typed FeaturePython)
  Dunit = g/cm3
  Dvalue = 6.9
  Group = -> [Nd_element001]
  conduct = 2
  density = 1
  expand = 3
  formula = Nd
  name = G4_Nd
  specific = 4
FEATURE [App::DocumentObjectGroupPython] Pm_element001  label="Pm_element : 1"  # scripted group (container) (typed FeaturePython)
  n = 1
  ref = Pm_element
FEATURE [App::DocumentObjectGroupPython] G4_Pm  # scripted group (container) (typed FeaturePython)
  Dunit = g/cm3
  Dvalue = 7.22
  Group = -> [Pm_element001]
  conduct = 2
  density = 1
  expand = 3
  formula = Pm
  name = G4_Pm
  specific = 4
FEATURE [App::DocumentObjectGroupPython] Sm_element001  label="Sm_element : 1"  # scripted group (container) (typed FeaturePython)
  n = 1
  ref = Sm_element
FEATURE [App::DocumentObjectGroupPython] G4_Sm  # scripted group (container) (typed FeaturePython)
  Dunit = g/cm3
  Dvalue = 7.46
  Group = -> [Sm_element001]
  conduct = 2
  density = 1
  expand = 3
  formula = Sm
  name = G4_Sm
  specific = 4
FEATURE [App::DocumentObjectGroupPython] Eu_element001  label="Eu_element : 1"  # scripted group (container) (typed FeaturePython)
  n = 1
  ref = Eu_element
FEATURE [App::DocumentObjectGroupPython] G4_Eu  # scripted group (container) (typed FeaturePython)
  Dunit = g/cm3
  Dvalue = 5.243
  Group = -> [Eu_element001]
  conduct = 2
  density = 1
  expand = 3
  formula = Eu
  name = G4_Eu
  specific = 4
FEATURE [App::DocumentObjectGroupPython] Gd_element002  label="Gd_element : 1"  # scripted group (container) (typed FeaturePython)
  n = 1
  ref = Gd_element
FEATURE [App::DocumentObjectGroupPython] G4_Gd  # scripted group (container) (typed FeaturePython)
  Dunit = g/cm3
  Dvalue = 7.9004
  Group = -> [Gd_element002]
  conduct = 2
  density = 1
  expand = 3
  formula = Gd
  name = G4_Gd
  specific = 4
FEATURE [App::DocumentObjectGroupPython] Tb_element001  label="Tb_element : 1"  # scripted group (container) (typed FeaturePython)
  n = 1
  ref = Tb_element
FEATURE [App::DocumentObjectGroupPython] G4_Tb  # scripted group (container) (typed FeaturePython)
  Dunit = g/cm3
  Dvalue = 8.229
  Group = -> [Tb_element001]
  conduct = 2
  density = 1
  expand = 3
  formula = Tb
  name = G4_Tb
  specific = 4
FEATURE [App::DocumentObjectGroupPython] Dy_element001  label="Dy_element : 1"  # scripted group (container) (typed FeaturePython)
  n = 1
  ref = Dy_element
FEATURE [App::DocumentObjectGroupPython] G4_Dy  # scripted group (container) (typed FeaturePython)
  Dunit = g/cm3
  Dvalue = 8.55
  Group = -> [Dy_element001]
  conduct = 2
  density = 1
  expand = 3
  formula = Dy
  name = G4_Dy
  specific = 4
FEATURE [App::DocumentObjectGroupPython] Ho_element001  label="Ho_element : 1"  # scripted group (container) (typed FeaturePython)
  n = 1
  ref = Ho_element
FEATURE [App::DocumentObjectGroupPython] G4_Ho  # scripted group (container) (typed FeaturePython)
  Dunit = g/cm3
  Dvalue = 8.795
  Group = -> [Ho_element001]
  conduct = 2
  density = 1
  expand = 3
  formula = Ho
  name = G4_Ho
  specific = 4
FEATURE [App::DocumentObjectGroupPython] Er_element001  label="Er_element : 1"  # scripted group (container) (typed FeaturePython)
  n = 1
  ref = Er_element
FEATURE [App::DocumentObjectGroupPython] G4_Er  # scripted group (container) (typed FeaturePython)
  Dunit = g/cm3
  Dvalue = 9.066
  Group = -> [Er_element001]
  conduct = 2
  density = 1
  expand = 3
  formula = Er
  name = G4_Er
  specific = 4
FEATURE [App::DocumentObjectGroupPython] Tm_element001  label="Tm_element : 1"  # scripted group (container) (typed FeaturePython)
  n = 1
  ref = Tm_element
FEATURE [App::DocumentObjectGroupPython] G4_Tm  # scripted group (container) (typed FeaturePython)
  Dunit = g/cm3
  Dvalue = 9.321
  Group = -> [Tm_element001]
  conduct = 2
  density = 1
  expand = 3
  formula = Tm
  name = G4_Tm
  specific = 4
FEATURE [App::DocumentObjectGroupPython] Yb_element001  label="Yb_element : 1"  # scripted group (container) (typed FeaturePython)
  n = 1
  ref = Yb_element
FEATURE [App::DocumentObjectGroupPython] G4_Yb  # scripted group (container) (typed FeaturePython)
  Dunit = g/cm3
  Dvalue = 6.73
  Group = -> [Yb_element001]
  conduct = 2
  density = 1
  expand = 3
  formula = Yb
  name = G4_Yb
  specific = 4
FEATURE [App::DocumentObjectGroupPython] Lu_element001  label="Lu_element : 1"  # scripted group (container) (typed FeaturePython)
  n = 1
  ref = Lu_element
FEATURE [App::DocumentObjectGroupPython] G4_Lu  # scripted group (container) (typed FeaturePython)
  Dunit = g/cm3
  Dvalue = 9.84
  Group = -> [Lu_element001]
  conduct = 2
  density = 1
  expand = 3
  formula = Lu
  name = G4_Lu
  specific = 4
FEATURE [App::DocumentObjectGroupPython] Hf_element001  label="Hf_element : 1"  # scripted group (container) (typed FeaturePython)
  n = 1
  ref = Hf_element
FEATURE [App::DocumentObjectGroupPython] G4_Hf  # scripted group (container) (typed FeaturePython)
  Dunit = g/cm3
  Dvalue = 13.31
  Group = -> [Hf_element001]
  conduct = 2
  density = 1
  expand = 3
  formula = Hf
  name = G4_Hf
  specific = 4
FEATURE [App::DocumentObjectGroupPython] Ta_element001  label="Ta_element : 1"  # scripted group (container) (typed FeaturePython)
  n = 1
  ref = Ta_element
FEATURE [App::DocumentObjectGroupPython] G4_Ta  # scripted group (container) (typed FeaturePython)
  Dunit = g/cm3
  Dvalue = 16.654
  Group = -> [Ta_element001]
  conduct = 2
  density = 1
  expand = 3
  formula = Ta
  name = G4_Ta
  specific = 4
FEATURE [App::DocumentObjectGroupPython] W_element004  label="W_element : 004"  # scripted group (container) (typed FeaturePython)
  n = 1
  ref = W_element
FEATURE [App::DocumentObjectGroupPython] G4_W  # scripted group (container) (typed FeaturePython)
  Dunit = g/cm3
  Dvalue = 19.3
  Group = -> [W_element004]
  conduct = 2
  density = 1
  expand = 3
  formula = W
  name = G4_W
  specific = 4
FEATURE [App::DocumentObjectGroupPython] Re_element001  label="Re_element : 1"  # scripted group (container) (typed FeaturePython)
  n = 1
  ref = Re_element
FEATURE [App::DocumentObjectGroupPython] G4_Re  # scripted group (container) (typed FeaturePython)
  Dunit = g/cm3
  Dvalue = 21.02
  Group = -> [Re_element001]
  conduct = 2
  density = 1
  expand = 3
  formula = Re
  name = G4_Re
  specific = 4
FEATURE [App::DocumentObjectGroupPython] Os_element001  label="Os_element : 1"  # scripted group (container) (typed FeaturePython)
  n = 1
  ref = Os_element
FEATURE [App::DocumentObjectGroupPython] G4_Os  # scripted group (container) (typed FeaturePython)
  Dunit = g/cm3
  Dvalue = 22.57
  Group = -> [Os_element001]
  conduct = 2
  density = 1
  expand = 3
  formula = Os
  name = G4_Os
  specific = 4
FEATURE [App::DocumentObjectGroupPython] Ir_element001  label="Ir_element : 1"  # scripted group (container) (typed FeaturePython)
  n = 1
  ref = Ir_element
FEATURE [App::DocumentObjectGroupPython] G4_Ir  # scripted group (container) (typed FeaturePython)
  Dunit = g/cm3
  Dvalue = 22.42
  Group = -> [Ir_element001]
  conduct = 2
  density = 1
  expand = 3
  formula = Ir
  name = G4_Ir
  specific = 4
FEATURE [App::DocumentObjectGroupPython] Pt_element001  label="Pt_element : 1"  # scripted group (container) (typed FeaturePython)
  n = 1
  ref = Pt_element
FEATURE [App::DocumentObjectGroupPython] G4_Pt  # scripted group (container) (typed FeaturePython)
  Dunit = g/cm3
  Dvalue = 21.45
  Group = -> [Pt_element001]
  conduct = 2
  density = 1
  expand = 3
  formula = Pt
  name = G4_Pt
  specific = 4
FEATURE [App::DocumentObjectGroupPython] Au_element001  label="Au_element : 1"  # scripted group (container) (typed FeaturePython)
  n = 1
  ref = Au_element
FEATURE [App::DocumentObjectGroupPython] G4_Au  # scripted group (container) (typed FeaturePython)
  Dunit = g/cm3
  Dvalue = 19.32
  Group = -> [Au_element001]
  conduct = 2
  density = 1
  expand = 3
  formula = Au
  name = G4_Au
  specific = 4
FEATURE [App::DocumentObjectGroupPython] Hg_element002  label="Hg_element : 002"  # scripted group (container) (typed FeaturePython)
  n = 1
  ref = Hg_element
FEATURE [App::DocumentObjectGroupPython] G4_Hg  # scripted group (container) (typed FeaturePython)
  Dunit = g/cm3
  Dvalue = 13.546
  Group = -> [Hg_element002]
  conduct = 2
  density = 1
  expand = 3
  formula = Hg
  name = G4_Hg
  specific = 4
FEATURE [App::DocumentObjectGroupPython] Tl_element002  label="Tl_element : 002"  # scripted group (container) (typed FeaturePython)
  n = 1
  ref = Tl_element
FEATURE [App::DocumentObjectGroupPython] G4_Tl  # scripted group (container) (typed FeaturePython)
  Dunit = g/cm3
  Dvalue = 11.72
  Group = -> [Tl_element002]
  conduct = 2
  density = 1
  expand = 3
  formula = Tl
  name = G4_Tl
  specific = 4
FEATURE [App::DocumentObjectGroupPython] Pb_element003  label="Pb_element : 1"  # scripted group (container) (typed FeaturePython)
  n = 1
  ref = Pb_element
FEATURE [App::DocumentObjectGroupPython] G4_Pb  # scripted group (container) (typed FeaturePython)
  Dunit = g/cm3
  Dvalue = 11.35
  Group = -> [Pb_element003]
  conduct = 2
  density = 1
  expand = 3
  formula = Pb
  name = G4_Pb
  specific = 4
FEATURE [App::DocumentObjectGroupPython] Bi_element002  label="Bi_element : 1"  # scripted group (container) (typed FeaturePython)
  n = 1
  ref = Bi_element
FEATURE [App::DocumentObjectGroupPython] G4_Bi  # scripted group (container) (typed FeaturePython)
  Dunit = g/cm3
  Dvalue = 9.747
  Group = -> [Bi_element002]
  conduct = 2
  density = 1
  expand = 3
  formula = Bi
  name = G4_Bi
  specific = 4
FEATURE [App::DocumentObjectGroupPython] Po_element001  label="Po_element : 1"  # scripted group (container) (typed FeaturePython)
  n = 1
  ref = Po_element
FEATURE [App::DocumentObjectGroupPython] G4_Po  # scripted group (container) (typed FeaturePython)
  Dunit = g/cm3
  Dvalue = 9.32
  Group = -> [Po_element001]
  conduct = 2
  density = 1
  expand = 3
  formula = Po
  name = G4_Po
  specific = 4
FEATURE [App::DocumentObjectGroupPython] At_element001  label="At_element : 1"  # scripted group (container) (typed FeaturePython)
  n = 1
  ref = At_element
FEATURE [App::DocumentObjectGroupPython] G4_At  # scripted group (container) (typed FeaturePython)
  Dunit = g/cm3
  Dvalue = 9.32
  Group = -> [At_element001]
  conduct = 2
  density = 1
  expand = 3
  formula = At
  name = G4_At
  specific = 4
FEATURE [App::DocumentObjectGroupPython] Rn_element001  label="Rn_element : 1"  # scripted group (container) (typed FeaturePython)
  n = 1
  ref = Rn_element
FEATURE [App::DocumentObjectGroupPython] G4_Rn  # scripted group (container) (typed FeaturePython)
  Dunit = g/cm3
  Dvalue = 0.00900662
  Group = -> [Rn_element001]
  conduct = 2
  density = 1
  expand = 3
  formula = Rn
  name = G4_Rn
  specific = 4
FEATURE [App::DocumentObjectGroupPython] Fr_element001  label="Fr_element : 1"  # scripted group (container) (typed FeaturePython)
  n = 1
  ref = Fr_element
FEATURE [App::DocumentObjectGroupPython] G4_Fr  # scripted group (container) (typed FeaturePython)
  Dunit = g/cm3
  Dvalue = 1
  Group = -> [Fr_element001]
  conduct = 2
  density = 1
  expand = 3
  formula = Fr
  name = G4_Fr
  specific = 4
FEATURE [App::DocumentObjectGroupPython] Ra_element001  label="Ra_element : 1"  # scripted group (container) (typed FeaturePython)
  n = 1
  ref = Ra_element
FEATURE [App::DocumentObjectGroupPython] G4_Ra  # scripted group (container) (typed FeaturePython)
  Dunit = g/cm3
  Dvalue = 5
  Group = -> [Ra_element001]
  conduct = 2
  density = 1
  expand = 3
  formula = Ra
  name = G4_Ra
  specific = 4
FEATURE [App::DocumentObjectGroupPython] Ac_element001  label="Ac_element : 1"  # scripted group (container) (typed FeaturePython)
  n = 1
  ref = Ac_element
FEATURE [App::DocumentObjectGroupPython] G4_Ac  # scripted group (container) (typed FeaturePython)
  Dunit = g/cm3
  Dvalue = 10.07
  Group = -> [Ac_element001]
  conduct = 2
  density = 1
  expand = 3
  formula = Ac
  name = G4_Ac
  specific = 4
FEATURE [App::DocumentObjectGroupPython] Th_element001  label="Th_element : 1"  # scripted group (container) (typed FeaturePython)
  n = 1
  ref = Th_element
FEATURE [App::DocumentObjectGroupPython] G4_Th  # scripted group (container) (typed FeaturePython)
  Dunit = g/cm3
  Dvalue = 11.72
  Group = -> [Th_element001]
  conduct = 2
  density = 1
  expand = 3
  formula = Th
  name = G4_Th
  specific = 4
FEATURE [App::DocumentObjectGroupPython] Pa_element001  label="Pa_element : 1"  # scripted group (container) (typed FeaturePython)
  n = 1
  ref = Pa_element
FEATURE [App::DocumentObjectGroupPython] G4_Pa  # scripted group (container) (typed FeaturePython)
  Dunit = g/cm3
  Dvalue = 15.37
  Group = -> [Pa_element001]
  conduct = 2
  density = 1
  expand = 3
  formula = Pa
  name = G4_Pa
  specific = 4
FEATURE [App::DocumentObjectGroupPython] U_element004  label="U_element : 004"  # scripted group (container) (typed FeaturePython)
  n = 1
  ref = U_element
FEATURE [App::DocumentObjectGroupPython] G4_U  # scripted group (container) (typed FeaturePython)
  Dunit = g/cm3
  Dvalue = 18.95
  Group = -> [U_element004]
  conduct = 2
  density = 1
  expand = 3
  formula = U
  name = G4_U
  specific = 4
FEATURE [App::DocumentObjectGroupPython] Np_element001  label="Np_element : 1"  # scripted group (container) (typed FeaturePython)
  n = 1
  ref = Np_element
FEATURE [App::DocumentObjectGroupPython] G4_Np  # scripted group (container) (typed FeaturePython)
  Dunit = g/cm3
  Dvalue = 20.25
  Group = -> [Np_element001]
  conduct = 2
  density = 1
  expand = 3
  formula = Np
  name = G4_Np
  specific = 4
FEATURE [App::DocumentObjectGroupPython] Pu_element002  label="Pu_element : 002"  # scripted group (container) (typed FeaturePython)
  n = 1
  ref = Pu_element
FEATURE [App::DocumentObjectGroupPython] G4_Pu  # scripted group (container) (typed FeaturePython)
  Dunit = g/cm3
  Dvalue = 19.84
  Group = -> [Pu_element002]
  conduct = 2
  density = 1
  expand = 3
  formula = Pu
  name = G4_Pu
  specific = 4
FEATURE [App::DocumentObjectGroupPython] Am_element001  label="Am_element : 1"  # scripted group (container) (typed FeaturePython)
  n = 1
  ref = Am_element
FEATURE [App::DocumentObjectGroupPython] G4_Am  # scripted group (container) (typed FeaturePython)
  Dunit = g/cm3
  Dvalue = 13.67
  Group = -> [Am_element001]
  conduct = 2
  density = 1
  expand = 3
  formula = Am
  name = G4_Am
  specific = 4
FEATURE [App::DocumentObjectGroupPython] Cm_element001  label="Cm_element : 1"  # scripted group (container) (typed FeaturePython)
  n = 1
  ref = Cm_element
FEATURE [App::DocumentObjectGroupPython] G4_Cm  # scripted group (container) (typed FeaturePython)
  Dunit = g/cm3
  Dvalue = 13.51
  Group = -> [Cm_element001]
  conduct = 2
  density = 1
  expand = 3
  formula = Cm
  name = G4_Cm
  specific = 4
FEATURE [App::DocumentObjectGroupPython] Bk_element001  label="Bk_element : 1"  # scripted group (container) (typed FeaturePython)
  n = 1
  ref = Bk_element
FEATURE [App::DocumentObjectGroupPython] G4_Bk  # scripted group (container) (typed FeaturePython)
  Dunit = g/cm3
  Dvalue = 14
  Group = -> [Bk_element001]
  conduct = 2
  density = 1
  expand = 3
  formula = Bk
  name = G4_Bk
  specific = 4
FEATURE [App::DocumentObjectGroupPython] Cf_element001  label="Cf_element : 1"  # scripted group (container) (typed FeaturePython)
  n = 1
  ref = Cf_element
FEATURE [App::DocumentObjectGroupPython] G4_Cf  # scripted group (container) (typed FeaturePython)
  Dunit = g/cm3
  Dvalue = 10
  Group = -> [Cf_element001]
  conduct = 2
  density = 1
  expand = 3
  formula = Cf
  name = G4_Cf
  specific = 4
FEATURE [App::DocumentObjectGroupPython] Element  # scripted group (container) (typed FeaturePython)
  Group = -> [G4_H,G4_He,G4_Li,G4_Be,G4_B,G4_C,G4_N,G4_O,G4_F,G4_Ne,G4_Na,G4_Mg,G4_Al,G4_Si,G4_P,G4_S,G4_Cl,G4_Ar,G4_K,G4_Ca,G4_Sc,G4_Ti,G4_V,G4_Cr,G4_Mn,G4_Fe,G4_Co,G4_Ni,G4_Cu,G4_Zn,G4_Ga,G4_Ge,G4_As,G4_Se,G4_Br,G4_Kr,G4_Rb,G4_Sr,G4_Y,G4_Zr,G4_Nb,G4_Mo,G4_Tc,G4_Ru,G4_Rh,G4_Pd,G4_Ag,G4_Cd,G4_In,G4_Sn,G4_Sb,G4_Te,G4_I,G4_Xe,G4_Cs,G4_Ba,G4_La,G4_Ce,G4_Pr,G4_Nd,G4_Pm,G4_Sm,G4_Eu,G4_Gd,G4_Tb,G4_Dy,G4_Ho,G4_Er,+30 more]
FEATURE [App::DocumentObjectGroupPython] H_element114  label="H_element : 063"  # scripted group (container) (typed FeaturePython)
  n = 2
  ref = H_element
FEATURE [App::DocumentObjectGroupPython] G4_lH2  # scripted group (container) (typed FeaturePython)
  Dunit = g/cm3
  Dvalue = 0.0708
  Group = -> [H_element114]
  conduct = 2
  density = 1
  expand = 3
  formula = G4_lH2
  name = G4_lH2
  specific = 4
FEATURE [App::DocumentObjectGroupPython] N_element049  label="N_element : 022"  # scripted group (container) (typed FeaturePython)
  n = 2
  ref = N_element
FEATURE [App::DocumentObjectGroupPython] G4_lN2  # scripted group (container) (typed FeaturePython)
  Dunit = g/cm3
  Dvalue = 0.807
  Group = -> [N_element049]
  conduct = 2
  density = 1
  expand = 3
  formula = G4_lN2
  name = G4_lN2
  specific = 4
FEATURE [App::DocumentObjectGroupPython] O_element106  label="O_element : 060"  # scripted group (container) (typed FeaturePython)
  n = 2
  ref = O_element
FEATURE [App::DocumentObjectGroupPython] G4_lO2  # scripted group (container) (typed FeaturePython)
  Dunit = g/cm3
  Dvalue = 1.141
  Group = -> [O_element106]
  conduct = 2
  density = 1
  expand = 3
  formula = G4_lO2
  name = G4_lO2
  specific = 4
FEATURE [App::DocumentObjectGroupPython] Ar_element003  label="Ar_element : 002"  # scripted group (container) (typed FeaturePython)
  n = 1
  ref = Ar_element
FEATURE [App::DocumentObjectGroupPython] G4_lAr  # scripted group (container) (typed FeaturePython)
  Dunit = g/cm3
  Dvalue = 1.396
  Group = -> [Ar_element003]
  conduct = 2
  density = 1
  expand = 3
  formula = G4_lAr
  name = G4_lAr
  specific = 4
FEATURE [App::DocumentObjectGroupPython] Br_element008  label="Br_element : 005"  # scripted group (container) (typed FeaturePython)
  n = 1
  ref = Br_element
FEATURE [App::DocumentObjectGroupPython] G4_lBr  # scripted group (container) (typed FeaturePython)
  Dunit = g/cm3
  Dvalue = 3.1028
  Group = -> [Br_element008]
  conduct = 2
  density = 1
  expand = 3
  formula = G4_lBr
  name = G4_lBr
  specific = 4
FEATURE [App::DocumentObjectGroupPython] Kr_element002  label="Kr_element : 002"  # scripted group (container) (typed FeaturePython)
  n = 1
  ref = Kr_element
FEATURE [App::DocumentObjectGroupPython] G4_lKr  # scripted group (container) (typed FeaturePython)
  Dunit = g/cm3
  Dvalue = 2.418
  Group = -> [Kr_element002]
  conduct = 2
  density = 1
  expand = 3
  formula = G4_lKr
  name = G4_lKr
  specific = 4
FEATURE [App::DocumentObjectGroupPython] Xe_element002  label="Xe_element : 002"  # scripted group (container) (typed FeaturePython)
  n = 1
  ref = Xe_element
FEATURE [App::DocumentObjectGroupPython] G4_lXe  # scripted group (container) (typed FeaturePython)
  Dunit = g/cm3
  Dvalue = 2.953
  Group = -> [Xe_element002]
  conduct = 2
  density = 1
  expand = 3
  formula = G4_lXe
  name = G4_lXe
  specific = 4
FEATURE [App::DocumentObjectGroupPython] O_element107  label="O_element : 061"  # scripted group (container) (typed FeaturePython)
  n = 4
  ref = O_element
FEATURE [App::DocumentObjectGroupPython] Pb_element004  label="Pb_element : 002"  # scripted group (container) (typed FeaturePython)
  n = 1
  ref = Pb_element
FEATURE [App::DocumentObjectGroupPython] W_element005  label="W_element : 005"  # scripted group (container) (typed FeaturePython)
  n = 1
  ref = W_element
FEATURE [App::DocumentObjectGroupPython] G4_PbWO4  # scripted group (container) (typed FeaturePython)
  Dunit = g/cm3
  Dvalue = 8.28
  Group = -> [O_element107,Pb_element004,W_element005]
  conduct = 2
  density = 1
  expand = 3
  formula = G4_PbWO4
  name = G4_PbWO4
  specific = 4
FEATURE [App::DocumentObjectGroupPython] H_element115  label="H_element : 064"  # scripted group (container) (typed FeaturePython)
  n = 1
  ref = H_element
FEATURE [App::DocumentObjectGroupPython] G4_Galactic  # scripted group (container) (typed FeaturePython)
  Dunit = g/cm3
  Dvalue = 0
  Group = -> [H_element115]
  conduct = 2
  density = 1
  expand = 3
  formula = G4_Galactic
  name = G4_Galactic
  specific = 4
FEATURE [App::DocumentObjectGroupPython] C_element125  label="C_element : 071"  # scripted group (container) (typed FeaturePython)
  n = 1
  ref = C_element
FEATURE [App::DocumentObjectGroupPython] G4_GRAPHITE_POROUS  # scripted group (container) (typed FeaturePython)
  Dunit = g/cm3
  Dvalue = 1.7
  Group = -> [C_element125]
  conduct = 2
  density = 1
  expand = 3
  formula = G4_GRAPHITE_POROUS
  name = G4_GRAPHITE_POROUS
  specific = 4
FEATURE [App::DocumentObjectGroupPython] H_element116  label="H_element : 0.150"  # scripted group (container) (typed FeaturePython)
  n = 0.080538
FEATURE [App::DocumentObjectGroupPython] C_element126  label="C_element : 0.600"  # scripted group (container) (typed FeaturePython)
  n = 0.599848
FEATURE [App::DocumentObjectGroupPython] O_element108  label="O_element : 0.320"  # scripted group (container) (typed FeaturePython)
  n = 0.319614
FEATURE [App::DocumentObjectGroupPython] G4_LUCITE  # scripted group (container) (typed FeaturePython)
  Dunit = g/cm3
  Dvalue = 1.19
  Group = -> [H_element116,C_element126,O_element108]
  conduct = 2
  density = 1
  expand = 3
  formula = G4_LUCITE
  name = G4_LUCITE
  specific = 4
FEATURE [App::DocumentObjectGroupPython] Cu_element002  label="Cu_element : 62"  # scripted group (container) (typed FeaturePython)
  n = 62
  ref = Cu_element
FEATURE [App::DocumentObjectGroupPython] Zn_element002  label="Zn_element : 35"  # scripted group (container) (typed FeaturePython)
  n = 35
  ref = Zn_element
FEATURE [App::DocumentObjectGroupPython] Pb_element005  label="Pb_element : 3"  # scripted group (container) (typed FeaturePython)
  n = 3
  ref = Pb_element
FEATURE [App::DocumentObjectGroupPython] G4_BRASS  # scripted group (container) (typed FeaturePython)
  Dunit = g/cm3
  Dvalue = 8.52
  Group = -> [Cu_element002,Zn_element002,Pb_element005]
  conduct = 2
  density = 1
  expand = 3
  formula = G4_BRASS
  name = G4_BRASS
  specific = 4
FEATURE [App::DocumentObjectGroupPython] Cu_element003  label="Cu_element : 89"  # scripted group (container) (typed FeaturePython)
  n = 89
  ref = Cu_element
FEATURE [App::DocumentObjectGroupPython] Zn_element003  label="Zn_element : 9"  # scripted group (container) (typed FeaturePython)
  n = 9
  ref = Zn_element
FEATURE [App::DocumentObjectGroupPython] Pb_element006  label="Pb_element : 2"  # scripted group (container) (typed FeaturePython)
  n = 2
  ref = Pb_element
FEATURE [App::DocumentObjectGroupPython] G4_BRONZE  # scripted group (container) (typed FeaturePython)
  Dunit = g/cm3
  Dvalue = 8.82
  Group = -> [Cu_element003,Zn_element003,Pb_element006]
  conduct = 2
  density = 1
  expand = 3
  formula = G4_BRONZE
  name = G4_BRONZE
  specific = 4
FEATURE [App::DocumentObjectGroupPython] Fe_element008  label="Fe_element : 74"  # scripted group (container) (typed FeaturePython)
  n = 74
  ref = Fe_element
FEATURE [App::DocumentObjectGroupPython] Cr_element002  label="Cr_element : 18"  # scripted group (container) (typed FeaturePython)
  n = 18
  ref = Cr_element
FEATURE [App::DocumentObjectGroupPython] Ni_element002  label="Ni_element : 8"  # scripted group (container) (typed FeaturePython)
  n = 8
  ref = Ni_element
FEATURE [App::DocumentObjectGroupPython] G4_STAINLESS_STEEL  label="G4_STAINLESS-STEEL"  # scripted group (container) (typed FeaturePython)
  Dunit = g/cm3
  Dvalue = 8
  Group = -> [Fe_element008,Cr_element002,Ni_element002]
  conduct = 2
  density = 1
  expand = 3
  formula = G4_STAINLESS-STEEL
  name = G4_STAINLESS-STEEL
  specific = 4
FEATURE [App::DocumentObjectGroupPython] H_element117  label="H_element : 065"  # scripted group (container) (typed FeaturePython)
  n = 18
  ref = H_element
FEATURE [App::DocumentObjectGroupPython] C_element127  label="C_element : 072"  # scripted group (container) (typed FeaturePython)
  n = 12
  ref = C_element
FEATURE [App::DocumentObjectGroupPython] O_element109  label="O_element : 062"  # scripted group (container) (typed FeaturePython)
  n = 7
  ref = O_element
FEATURE [App::DocumentObjectGroupPython] G4_CR39  # scripted group (container) (typed FeaturePython)
  Dunit = g/cm3
  Dvalue = 1.32
  Group = -> [H_element117,C_element127,O_element109]
  conduct = 2
  density = 1
  expand = 3
  formula = G4_CR39
  name = G4_CR39
  specific = 4
FEATURE [App::DocumentObjectGroupPython] H_element118  label="H_element : 38"  # scripted group (container) (typed FeaturePython)
  n = 38
  ref = H_element
FEATURE [App::DocumentObjectGroupPython] C_element128  label="C_element : 073"  # scripted group (container) (typed FeaturePython)
  n = 18
  ref = C_element
FEATURE [App::DocumentObjectGroupPython] O_element110  label="O_element : 063"  # scripted group (container) (typed FeaturePython)
  n = 1
  ref = O_element
FEATURE [App::DocumentObjectGroupPython] G4_OCTADECANOL  # scripted group (container) (typed FeaturePython)
  Dunit = g/cm3
  Dvalue = 0.812
  Group = -> [H_element118,C_element128,O_element110]
  conduct = 2
  density = 1
  expand = 3
  formula = G4_OCTADECANOL
  name = G4_OCTADECANOL
  specific = 4
FEATURE [App::DocumentObjectGroupPython] HEP  # scripted group (container) (typed FeaturePython)
  Group = -> [G4_lH2,G4_lN2,G4_lO2,G4_lAr,G4_lBr,G4_lKr,G4_lXe,G4_PbWO4,G4_Galactic,G4_GRAPHITE_POROUS,G4_LUCITE,G4_BRASS,G4_BRONZE,G4_STAINLESS_STEEL,G4_CR39,G4_OCTADECANOL]
FEATURE [App::DocumentObjectGroupPython] C_element129  label="C_element : 074"  # scripted group (container) (typed FeaturePython)
  n = 14
  ref = C_element
FEATURE [App::DocumentObjectGroupPython] H_element119  label="H_element : 066"  # scripted group (container) (typed FeaturePython)
  n = 10
  ref = H_element
FEATURE [App::DocumentObjectGroupPython] O_element111  label="O_element : 064"  # scripted group (container) (typed FeaturePython)
  n = 2
  ref = O_element
FEATURE [App::DocumentObjectGroupPython] N_element050  label="N_element : 023"  # scripted group (container) (typed FeaturePython)
  n = 2
  ref = N_element
FEATURE [App::DocumentObjectGroupPython] G4_KEVLAR  # scripted group (container) (typed FeaturePython)
  Dunit = g/cm3
  Dvalue = 1.44
  Group = -> [C_element129,H_element119,O_element111,N_element050]
  conduct = 2
  density = 1
  expand = 3
  formula = G4_KEVLAR
  name = G4_KEVLAR
  specific = 4
FEATURE [App::DocumentObjectGroupPython] C_element130  label="C_element : 075"  # scripted group (container) (typed FeaturePython)
  n = 10
  ref = C_element
FEATURE [App::DocumentObjectGroupPython] H_element120  label="H_element : 067"  # scripted group (container) (typed FeaturePython)
  n = 8
  ref = H_element
FEATURE [App::DocumentObjectGroupPython] O_element112  label="O_element : 065"  # scripted group (container) (typed FeaturePython)
  n = 4
  ref = O_element
FEATURE [App::DocumentObjectGroupPython] G4_DACRON  # scripted group (container) (typed FeaturePython)
  Dunit = g/cm3
  Dvalue = 1.4
  Group = -> [C_element130,H_element120,O_element112]
  conduct = 2
  density = 1
  expand = 3
  formula = G4_DACRON
  name = G4_DACRON
  specific = 4
FEATURE [App::DocumentObjectGroupPython] C_element131  label="C_element : 076"  # scripted group (container) (typed FeaturePython)
  n = 4
  ref = C_element
FEATURE [App::DocumentObjectGroupPython] H_element121  label="H_element : 068"  # scripted group (container) (typed FeaturePython)
  n = 5
  ref = H_element
FEATURE [App::DocumentObjectGroupPython] Cl_element030  label="Cl_element : 016"  # scripted group (container) (typed FeaturePython)
  n = 1
  ref = Cl_element
FEATURE [App::DocumentObjectGroupPython] G4_NEOPRENE  # scripted group (container) (typed FeaturePython)
  Dunit = g/cm3
  Dvalue = 1.23
  Group = -> [C_element131,H_element121,Cl_element030]
  conduct = 2
  density = 1
  expand = 3
  formula = G4_NEOPRENE
  name = G4_NEOPRENE
  specific = 4
FEATURE [App::DocumentObjectGroupPython] Space  # scripted group (container) (typed FeaturePython)
  Group = -> [G4_KEVLAR,G4_DACRON,G4_NEOPRENE]
FEATURE [App::DocumentObjectGroupPython] H_element122  label="H_element : 069"  # scripted group (container) (typed FeaturePython)
  n = 5
  ref = H_element
FEATURE [App::DocumentObjectGroupPython] C_element132  label="C_element : 077"  # scripted group (container) (typed FeaturePython)
  n = 4
  ref = C_element
FEATURE [App::DocumentObjectGroupPython] N_element051  label="N_element : 3"  # scripted group (container) (typed FeaturePython)
  n = 3
  ref = N_element
FEATURE [App::DocumentObjectGroupPython] O_element113  label="O_element : 066"  # scripted group (container) (typed FeaturePython)
  n = 1
  ref = O_element
FEATURE [App::DocumentObjectGroupPython] G4_CYTOSINE  # scripted group (container) (typed FeaturePython)
  Dunit = g/cm3
  Dvalue = 1.55
  Group = -> [H_element122,C_element132,N_element051,O_element113]
  conduct = 2
  density = 1
  expand = 3
  formula = G4_CYTOSINE
  name = G4_CYTOSINE
  specific = 4
FEATURE [App::DocumentObjectGroupPython] H_element123  label="H_element : 070"  # scripted group (container) (typed FeaturePython)
  n = 6
  ref = H_element
FEATURE [App::DocumentObjectGroupPython] C_element133  label="C_element : 078"  # scripted group (container) (typed FeaturePython)
  n = 5
  ref = C_element
FEATURE [App::DocumentObjectGroupPython] N_element052  label="N_element : 024"  # scripted group (container) (typed FeaturePython)
  n = 2
  ref = N_element
FEATURE [App::DocumentObjectGroupPython] O_element114  label="O_element : 067"  # scripted group (container) (typed FeaturePython)
  n = 2
  ref = O_element
FEATURE [App::DocumentObjectGroupPython] G4_THYMINE  # scripted group (container) (typed FeaturePython)
  Dunit = g/cm3
  Dvalue = 1.23
  Group = -> [H_element123,C_element133,N_element052,O_element114]
  conduct = 2
  density = 1
  expand = 3
  formula = G4_THYMINE
  name = G4_THYMINE
  specific = 4
FEATURE [App::DocumentObjectGroupPython] H_element124  label="H_element : 071"  # scripted group (container) (typed FeaturePython)
  n = 4
  ref = H_element
FEATURE [App::DocumentObjectGroupPython] C_element134  label="C_element : 079"  # scripted group (container) (typed FeaturePython)
  n = 4
  ref = C_element
FEATURE [App::DocumentObjectGroupPython] N_element053  label="N_element : 025"  # scripted group (container) (typed FeaturePython)
  n = 2
  ref = N_element
FEATURE [App::DocumentObjectGroupPython] O_element115  label="O_element : 068"  # scripted group (container) (typed FeaturePython)
  n = 2
  ref = O_element
FEATURE [App::DocumentObjectGroupPython] G4_URACIL  # scripted group (container) (typed FeaturePython)
  Dunit = g/cm3
  Dvalue = 1.32
  Group = -> [H_element124,C_element134,N_element053,O_element115]
  conduct = 2
  density = 1
  expand = 3
  formula = G4_URACIL
  name = G4_URACIL
  specific = 4
FEATURE [App::DocumentObjectGroupPython] H_element125  label="H_element : 072"  # scripted group (container) (typed FeaturePython)
  n = 4
  ref = H_element
FEATURE [App::DocumentObjectGroupPython] C_element135  label="C_element : 080"  # scripted group (container) (typed FeaturePython)
  n = 5
  ref = C_element
FEATURE [App::DocumentObjectGroupPython] N_element054  label="N_element : 026"  # scripted group (container) (typed FeaturePython)
  n = 5
  ref = N_element
FEATURE [App::DocumentObjectGroupPython] G4_DNA_ADENINE  # scripted group (container) (typed FeaturePython)
  Dunit = g/cm3
  Dvalue = 1
  Group = -> [H_element125,C_element135,N_element054]
  conduct = 2
  density = 1
  expand = 3
  formula = G4_DNA_ADENINE
  name = G4_DNA_ADENINE
  specific = 4
FEATURE [App::DocumentObjectGroupPython] H_element126  label="H_element : 073"  # scripted group (container) (typed FeaturePython)
  n = 4
  ref = H_element
FEATURE [App::DocumentObjectGroupPython] C_element136  label="C_element : 081"  # scripted group (container) (typed FeaturePython)
  n = 5
  ref = C_element
FEATURE [App::DocumentObjectGroupPython] N_element055  label="N_element : 027"  # scripted group (container) (typed FeaturePython)
  n = 5
  ref = N_element
FEATURE [App::DocumentObjectGroupPython] O_element116  label="O_element : 069"  # scripted group (container) (typed FeaturePython)
  n = 1
  ref = O_element
FEATURE [App::DocumentObjectGroupPython] G4_DNA_GUANINE  # scripted group (container) (typed FeaturePython)
  Dunit = g/cm3
  Dvalue = 1
  Group = -> [H_element126,C_element136,N_element055,O_element116]
  conduct = 2
  density = 1
  expand = 3
  formula = G4_DNA_GUANINE
  name = G4_DNA_GUANINE
  specific = 4
FEATURE [App::DocumentObjectGroupPython] H_element127  label="H_element : 074"  # scripted group (container) (typed FeaturePython)
  n = 4
  ref = H_element
FEATURE [App::DocumentObjectGroupPython] C_element137  label="C_element : 082"  # scripted group (container) (typed FeaturePython)
  n = 4
  ref = C_element
FEATURE [App::DocumentObjectGroupPython] N_element056  label="N_element : 028"  # scripted group (container) (typed FeaturePython)
  n = 3
  ref = N_element
FEATURE [App::DocumentObjectGroupPython] O_element117  label="O_element : 070"  # scripted group (container) (typed FeaturePython)
  n = 1
  ref = O_element
FEATURE [App::DocumentObjectGroupPython] G4_DNA_CYTOSINE  # scripted group (container) (typed FeaturePython)
  Dunit = g/cm3
  Dvalue = 1
  Group = -> [H_element127,C_element137,N_element056,O_element117]
  conduct = 2
  density = 1
  expand = 3
  formula = G4_DNA_CYTOSINE
  name = G4_DNA_CYTOSINE
  specific = 4
FEATURE [App::DocumentObjectGroupPython] H_element128  label="H_element : 075"  # scripted group (container) (typed FeaturePython)
  n = 5
  ref = H_element
FEATURE [App::DocumentObjectGroupPython] C_element138  label="C_element : 083"  # scripted group (container) (typed FeaturePython)
  n = 5
  ref = C_element
FEATURE [App::DocumentObjectGroupPython] N_element057  label="N_element : 029"  # scripted group (container) (typed FeaturePython)
  n = 2
  ref = N_element
FEATURE [App::DocumentObjectGroupPython] O_element118  label="O_element : 071"  # scripted group (container) (typed FeaturePython)
  n = 2
  ref = O_element
FEATURE [App::DocumentObjectGroupPython] G4_DNA_THYMINE  # scripted group (container) (typed FeaturePython)
  Dunit = g/cm3
  Dvalue = 1
  Group = -> [H_element128,C_element138,N_element057,O_element118]
  conduct = 2
  density = 1
  expand = 3
  formula = G4_DNA_THYMINE
  name = G4_DNA_THYMINE
  specific = 4
FEATURE [App::DocumentObjectGroupPython] H_element129  label="H_element : 076"  # scripted group (container) (typed FeaturePython)
  n = 3
  ref = H_element
FEATURE [App::DocumentObjectGroupPython] C_element139  label="C_element : 084"  # scripted group (container) (typed FeaturePython)
  n = 4
  ref = C_element
FEATURE [App::DocumentObjectGroupPython] N_element058  label="N_element : 030"  # scripted group (container) (typed FeaturePython)
  n = 2
  ref = N_element
FEATURE [App::DocumentObjectGroupPython] O_element119  label="O_element : 072"  # scripted group (container) (typed FeaturePython)
  n = 2
  ref = O_element
FEATURE [App::DocumentObjectGroupPython] G4_DNA_URACIL  # scripted group (container) (typed FeaturePython)
  Dunit = g/cm3
  Dvalue = 1
  Group = -> [H_element129,C_element139,N_element058,O_element119]
  conduct = 2
  density = 1
  expand = 3
  formula = G4_DNA_URACIL
  name = G4_DNA_URACIL
  specific = 4
FEATURE [App::DocumentObjectGroupPython] H_element130  label="H_element : 077"  # scripted group (container) (typed FeaturePython)
  n = 10
  ref = H_element
FEATURE [App::DocumentObjectGroupPython] C_element140  label="C_element : 085"  # scripted group (container) (typed FeaturePython)
  n = 10
  ref = C_element
FEATURE [App::DocumentObjectGroupPython] N_element059  label="N_element : 031"  # scripted group (container) (typed FeaturePython)
  n = 5
  ref = N_element
FEATURE [App::DocumentObjectGroupPython] O_element120  label="O_element : 073"  # scripted group (container) (typed FeaturePython)
  n = 4
  ref = O_element
FEATURE [App::DocumentObjectGroupPython] G4_DNA_ADENOSINE  # scripted group (container) (typed FeaturePython)
  Dunit = g/cm3
  Dvalue = 1
  Group = -> [H_element130,C_element140,N_element059,O_element120]
  conduct = 2
  density = 1
  expand = 3
  formula = G4_DNA_ADENOSINE
  name = G4_DNA_ADENOSINE
  specific = 4
FEATURE [App::DocumentObjectGroupPython] H_element131  label="H_element : 078"  # scripted group (container) (typed FeaturePython)
  n = 10
  ref = H_element
FEATURE [App::DocumentObjectGroupPython] C_element141  label="C_element : 086"  # scripted group (container) (typed FeaturePython)
  n = 10
  ref = C_element
FEATURE [App::DocumentObjectGroupPython] N_element060  label="N_element : 032"  # scripted group (container) (typed FeaturePython)
  n = 5
  ref = N_element
FEATURE [App::DocumentObjectGroupPython] O_element121  label="O_element : 074"  # scripted group (container) (typed FeaturePython)
  n = 5
  ref = O_element
FEATURE [App::DocumentObjectGroupPython] G4_DNA_GUANOSINE  # scripted group (container) (typed FeaturePython)
  Dunit = g/cm3
  Dvalue = 1
  Group = -> [H_element131,C_element141,N_element060,O_element121]
  conduct = 2
  density = 1
  expand = 3
  formula = G4_DNA_GUANOSINE
  name = G4_DNA_GUANOSINE
  specific = 4
FEATURE [App::DocumentObjectGroupPython] H_element132  label="H_element : 079"  # scripted group (container) (typed FeaturePython)
  n = 10
  ref = H_element
FEATURE [App::DocumentObjectGroupPython] C_element142  label="C_element : 087"  # scripted group (container) (typed FeaturePython)
  n = 9
  ref = C_element
FEATURE [App::DocumentObjectGroupPython] N_element061  label="N_element : 033"  # scripted group (container) (typed FeaturePython)
  n = 3
  ref = N_element
FEATURE [App::DocumentObjectGroupPython] O_element122  label="O_element : 075"  # scripted group (container) (typed FeaturePython)
  n = 5
  ref = O_element
FEATURE [App::DocumentObjectGroupPython] G4_DNA_CYTIDINE  # scripted group (container) (typed FeaturePython)
  Dunit = g/cm3
  Dvalue = 1
  Group = -> [H_element132,C_element142,N_element061,O_element122]
  conduct = 2
  density = 1
  expand = 3
  formula = G4_DNA_CYTIDINE
  name = G4_DNA_CYTIDINE
  specific = 4
FEATURE [App::DocumentObjectGroupPython] H_element133  label="H_element : 080"  # scripted group (container) (typed FeaturePython)
  n = 9
  ref = H_element
FEATURE [App::DocumentObjectGroupPython] C_element143  label="C_element : 088"  # scripted group (container) (typed FeaturePython)
  n = 9
  ref = C_element
FEATURE [App::DocumentObjectGroupPython] N_element062  label="N_element : 034"  # scripted group (container) (typed FeaturePython)
  n = 2
  ref = N_element
FEATURE [App::DocumentObjectGroupPython] O_element123  label="O_element : 076"  # scripted group (container) (typed FeaturePython)
  n = 6
  ref = O_element
FEATURE [App::DocumentObjectGroupPython] G4_DNA_URIDINE  # scripted group (container) (typed FeaturePython)
  Dunit = g/cm3
  Dvalue = 1
  Group = -> [H_element133,C_element143,N_element062,O_element123]
  conduct = 2
  density = 1
  expand = 3
  formula = G4_DNA_URIDINE
  name = G4_DNA_URIDINE
  specific = 4
FEATURE [App::DocumentObjectGroupPython] H_element134  label="H_element : 081"  # scripted group (container) (typed FeaturePython)
  n = 11
  ref = H_element
FEATURE [App::DocumentObjectGroupPython] C_element144  label="C_element : 089"  # scripted group (container) (typed FeaturePython)
  n = 10
  ref = C_element
FEATURE [App::DocumentObjectGroupPython] N_element063  label="N_element : 035"  # scripted group (container) (typed FeaturePython)
  n = 2
  ref = N_element
FEATURE [App::DocumentObjectGroupPython] O_element124  label="O_element : 077"  # scripted group (container) (typed FeaturePython)
  n = 6
  ref = O_element
FEATURE [App::DocumentObjectGroupPython] G4_DNA_METHYLURIDINE  # scripted group (container) (typed FeaturePython)
  Dunit = g/cm3
  Dvalue = 1
  Group = -> [H_element134,C_element144,N_element063,O_element124]
  conduct = 2
  density = 1
  expand = 3
  formula = G4_DNA_METHYLURIDINE
  name = G4_DNA_METHYLURIDINE
  specific = 4
FEATURE [App::DocumentObjectGroupPython] P_element014  label="P_element : 003"  # scripted group (container) (typed FeaturePython)
  n = 1
  ref = P_element
FEATURE [App::DocumentObjectGroupPython] O_element125  label="O_element : 078"  # scripted group (container) (typed FeaturePython)
  n = 3
  ref = O_element
FEATURE [App::DocumentObjectGroupPython] G4_DNA_MONOPHOSPHATE  # scripted group (container) (typed FeaturePython)
  Dunit = g/cm3
  Dvalue = 1
  Group = -> [P_element014,O_element125]
  conduct = 2
  density = 1
  expand = 3
  formula = G4_DNA_MONOPHOSPHATE
  name = G4_DNA_MONOPHOSPHATE
  specific = 4
FEATURE [App::DocumentObjectGroupPython] H_element135  label="H_element : 082"  # scripted group (container) (typed FeaturePython)
  n = 10
  ref = H_element
FEATURE [App::DocumentObjectGroupPython] C_element145  label="C_element : 090"  # scripted group (container) (typed FeaturePython)
  n = 10
  ref = C_element
FEATURE [App::DocumentObjectGroupPython] N_element064  label="N_element : 036"  # scripted group (container) (typed FeaturePython)
  n = 5
  ref = N_element
FEATURE [App::DocumentObjectGroupPython] O_element126  label="O_element : 079"  # scripted group (container) (typed FeaturePython)
  n = 7
  ref = O_element
FEATURE [App::DocumentObjectGroupPython] P_element015  label="P_element : 004"  # scripted group (container) (typed FeaturePython)
  n = 1
  ref = P_element
FEATURE [App::DocumentObjectGroupPython] G4_DNA_A  # scripted group (container) (typed FeaturePython)
  Dunit = g/cm3
  Dvalue = 1
  Group = -> [H_element135,C_element145,N_element064,O_element126,P_element015]
  conduct = 2
  density = 1
  expand = 3
  formula = G4_DNA_A
  name = G4_DNA_A
  specific = 4
FEATURE [App::DocumentObjectGroupPython] H_element136  label="H_element : 083"  # scripted group (container) (typed FeaturePython)
  n = 10
  ref = H_element
FEATURE [App::DocumentObjectGroupPython] C_element146  label="C_element : 091"  # scripted group (container) (typed FeaturePython)
  n = 10
  ref = C_element
FEATURE [App::DocumentObjectGroupPython] N_element065  label="N_element : 037"  # scripted group (container) (typed FeaturePython)
  n = 5
  ref = N_element
FEATURE [App::DocumentObjectGroupPython] O_element127  label="O_element : 8"  # scripted group (container) (typed FeaturePython)
  n = 8
  ref = O_element
FEATURE [App::DocumentObjectGroupPython] P_element016  label="P_element : 005"  # scripted group (container) (typed FeaturePython)
  n = 1
  ref = P_element
FEATURE [App::DocumentObjectGroupPython] G4_DNA_G  # scripted group (container) (typed FeaturePython)
  Dunit = g/cm3
  Dvalue = 1
  Group = -> [H_element136,C_element146,N_element065,O_element127,P_element016]
  conduct = 2
  density = 1
  expand = 3
  formula = G4_DNA_G
  name = G4_DNA_G
  specific = 4
FEATURE [App::DocumentObjectGroupPython] H_element137  label="H_element : 084"  # scripted group (container) (typed FeaturePython)
  n = 10
  ref = H_element
FEATURE [App::DocumentObjectGroupPython] C_element147  label="C_element : 092"  # scripted group (container) (typed FeaturePython)
  n = 9
  ref = C_element
FEATURE [App::DocumentObjectGroupPython] N_element066  label="N_element : 038"  # scripted group (container) (typed FeaturePython)
  n = 3
  ref = N_element
FEATURE [App::DocumentObjectGroupPython] O_element128  label="O_element : 080"  # scripted group (container) (typed FeaturePython)
  n = 8
  ref = O_element
FEATURE [App::DocumentObjectGroupPython] P_element017  label="P_element : 006"  # scripted group (container) (typed FeaturePython)
  n = 1
  ref = P_element
FEATURE [App::DocumentObjectGroupPython] G4_DNA_C  # scripted group (container) (typed FeaturePython)
  Dunit = g/cm3
  Dvalue = 1
  Group = -> [H_element137,C_element147,N_element066,O_element128,P_element017]
  conduct = 2
  density = 1
  expand = 3
  formula = G4_DNA_C
  name = G4_DNA_C
  specific = 4
FEATURE [App::DocumentObjectGroupPython] H_element138  label="H_element : 085"  # scripted group (container) (typed FeaturePython)
  n = 9
  ref = H_element
FEATURE [App::DocumentObjectGroupPython] C_element148  label="C_element : 093"  # scripted group (container) (typed FeaturePython)
  n = 9
  ref = C_element
FEATURE [App::DocumentObjectGroupPython] N_element067  label="N_element : 039"  # scripted group (container) (typed FeaturePython)
  n = 2
  ref = N_element
FEATURE [App::DocumentObjectGroupPython] O_element129  label="O_element : 9"  # scripted group (container) (typed FeaturePython)
  n = 9
  ref = O_element
FEATURE [App::DocumentObjectGroupPython] P_element018  label="P_element : 007"  # scripted group (container) (typed FeaturePython)
  n = 1
  ref = P_element
FEATURE [App::DocumentObjectGroupPython] G4_DNA_U  # scripted group (container) (typed FeaturePython)
  Dunit = g/cm3
  Dvalue = 1
  Group = -> [H_element138,C_element148,N_element067,O_element129,P_element018]
  conduct = 2
  density = 1
  expand = 3
  formula = G4_DNA_U
  name = G4_DNA_U
  specific = 4
FEATURE [App::DocumentObjectGroupPython] H_element139  label="H_element : 086"  # scripted group (container) (typed FeaturePython)
  n = 11
  ref = H_element
FEATURE [App::DocumentObjectGroupPython] C_element149  label="C_element : 094"  # scripted group (container) (typed FeaturePython)
  n = 10
  ref = C_element
FEATURE [App::DocumentObjectGroupPython] N_element068  label="N_element : 040"  # scripted group (container) (typed FeaturePython)
  n = 2
  ref = N_element
FEATURE [App::DocumentObjectGroupPython] O_element130  label="O_element : 081"  # scripted group (container) (typed FeaturePython)
  n = 9
  ref = O_element
FEATURE [App::DocumentObjectGroupPython] P_element019  label="P_element : 008"  # scripted group (container) (typed FeaturePython)
  n = 1
  ref = P_element
FEATURE [App::DocumentObjectGroupPython] G4_DNA_MU  # scripted group (container) (typed FeaturePython)
  Dunit = g/cm3
  Dvalue = 1
  Group = -> [H_element139,C_element149,N_element068,O_element130,P_element019]
  conduct = 2
  density = 1
  expand = 3
  formula = G4_DNA_MU
  name = G4_DNA_MU
  specific = 4
FEATURE [App::DocumentObjectGroupPython] BioChemical  # scripted group (container) (typed FeaturePython)
  Group = -> [G4_CYTOSINE,G4_THYMINE,G4_URACIL,G4_DNA_ADENINE,G4_DNA_GUANINE,G4_DNA_CYTOSINE,G4_DNA_THYMINE,G4_DNA_URACIL,G4_DNA_ADENOSINE,G4_DNA_GUANOSINE,G4_DNA_CYTIDINE,G4_DNA_URIDINE,G4_DNA_METHYLURIDINE,G4_DNA_MONOPHOSPHATE,G4_DNA_A,G4_DNA_G,G4_DNA_C,G4_DNA_U,G4_DNA_MU]
FEATURE [App::DocumentObjectGroupPython] G4Materials  # scripted group (container) (typed FeaturePython)
  Group = -> [NIST,Element,HEP,Space,BioChemical]
  version = 1
FEATURE [App::DocumentObjectGroupPython] Geant4  # scripted group (container) (typed FeaturePython)
  Group = -> [G4Isotopes,G4Elements,G4Materials]
FEATURE [App::DocumentObjectGroupPython] Materials  # scripted group (container) (typed FeaturePython)
  Group = -> [Geant4]
FEATURE [Part::FeaturePython] GDMLBox_WorldBox  # WARN: FeaturePython — macro-defined, semantics opaque (R4)
  lunit = 2
  material = 5
  x = 100
  y = 100
  z = 100
FEATURE [Part::FeaturePython] GDMLBox_Box  # WARN: FeaturePython — macro-defined, semantics opaque (R4)
  Placement = pos=(10,0,0) rot=(0,0,1;0rad)
  lunit = 2
  material = 0
  x = 10
  y = 10
  z = 10
FEATURE [App::Part] LV_Box
  Group = -> [GDMLBox_Box]
  Origin = -> Origin001
  Placement = pos=(0,10,0) rot=(0,0,1;0rad)
FEATURE [Part::FeaturePython] Array  # Draft array (typed FeaturePython)
  AlwaysSyncPlacement = false
  Angle = 360
  ArrayType = 0
  Axis = (0,0,1)
  Base = -> LV_Box
  Center = (0,0,0)
  Count = 4
  ExpandArray = false
  Fuse = false
  IntervalAxis = (0,0,0)
  IntervalX = (25,0,0)
  IntervalY = (0,25,0)
  IntervalZ = (0,0,100)
  NumberCircles = 3
  NumberPolar = 5
  NumberX = 2
  NumberY = 2
  NumberZ = 1
  PlacementList = 4 placements: [(0,10,0),(0,35,0),(25,10,0),(25,35,0)]
  RadialDistance = 50
  ScaleList = (4) [(1,1,1),(1,1,1),(1,1,1),(1,1,1)]
  Symmetry = 1
  TangentialDistance = 25
FEATURE [App::Part] Part
  Group = -> [LV_Box,Array]
  Origin = -> Origin002
FEATURE [App::Part] worldVOL
  Group = -> [GDMLBox_WorldBox,Part]
  Origin = -> Origin
